FCSTD DOCUMENT  (FreeCAD 0.18R16093 (Git))
Label: Push2
License: All rights reserved
LicenseURL: http://en.wikipedia.org/wiki/All_rights_reserved
objects: App::DocumentObjectGroupPython×302, Part::Box×285, App::Part×154, Part::Extrusion×106, Part::Part2DObjectPython×97, Part::Cut×85, Part::Fillet×64, Part::Cylinder×35, Part::MultiFuse×32, Sketcher::SketchObject×22, PartDesign::Pad×11, App::DocumentObjectGroup×8, Image::ImagePlane×2
note: 748 computed .brp shape members not serialized (recipe doc carries the construction recipe); baked Part::Feature solids carry a one-line shape summary decoded from their .brp

FEATURE [Image::ImagePlane] ImagePlane  label="ImageTop"
  XSize = 378
  YSize = 304
FEATURE [Part::Box] Box  label="Cube"
  AttacherType = Attacher::AttachEngine3D
  Height = 23
  Length = 378
  Placement = pos=(-189,-152,-23) rot=(0,0,1;0rad)
  Width = 304
FEATURE [Sketcher::SketchObject] Sketch
  MapMode = 5
  sketch-geometry (1):
    g0: Circle CenterX=0 CenterY=0 CenterZ=0 NormalX=0 NormalY=0 NormalZ=1 AngleXU=0 Radius=6.32501
  constraints (1):
    c: Coincident(g0,g-1)
FEATURE [PartDesign::Pad] Pad
  Length = 15
  Length2 = 100
  Profile = -> Sketch
  Type = 0
FEATURE [Sketcher::SketchObject] Sketch001
  MapMode = 5
  sketch-geometry (1):
    g0: Circle CenterX=0 CenterY=0 CenterZ=0 NormalX=0 NormalY=0 NormalZ=1 AngleXU=0 Radius=6.32501
  constraints (1):
    c: Coincident(g0,g-1)
FEATURE [PartDesign::Pad] Pad001
  Length = 15
  Length2 = 100
  Profile = -> Sketch001
  Type = 0
FEATURE [Sketcher::SketchObject] Sketch002
  MapMode = 5
  sketch-geometry (1):
    g0: Circle CenterX=0 CenterY=0 CenterZ=0 NormalX=0 NormalY=0 NormalZ=1 AngleXU=0 Radius=6.32501
  constraints (1):
    c: Coincident(g0,g-1)
FEATURE [PartDesign::Pad] Pad002
  Length = 15
  Length2 = 100
  Profile = -> Sketch002
  Type = 0
FEATURE [Sketcher::SketchObject] Sketch003
  MapMode = 5
  sketch-geometry (1):
    g0: Circle CenterX=0 CenterY=0 CenterZ=0 NormalX=0 NormalY=0 NormalZ=1 AngleXU=0 Radius=6.32501
  constraints (1):
    c: Coincident(g0,g-1)
FEATURE [PartDesign::Pad] Pad003
  Length = 15
  Length2 = 100
  Profile = -> Sketch003
  Type = 0
FEATURE [Sketcher::SketchObject] Sketch004
  MapMode = 5
  sketch-geometry (1):
    g0: Circle CenterX=0 CenterY=0 CenterZ=0 NormalX=0 NormalY=0 NormalZ=1 AngleXU=0 Radius=6.32501
  constraints (1):
    c: Coincident(g0,g-1)
FEATURE [PartDesign::Pad] Pad004
  Length = 15
  Length2 = 100
  Profile = -> Sketch004
  Type = 0
FEATURE [Sketcher::SketchObject] Sketch005
  MapMode = 5
  sketch-geometry (1):
    g0: Circle CenterX=0 CenterY=0 CenterZ=0 NormalX=0 NormalY=0 NormalZ=1 AngleXU=0 Radius=6.32501
  constraints (1):
    c: Coincident(g0,g-1)
FEATURE [PartDesign::Pad] Pad005
  Length = 15
  Length2 = 100
  Profile = -> Sketch005
  Type = 0
FEATURE [Sketcher::SketchObject] Sketch006
  MapMode = 5
  sketch-geometry (1):
    g0: Circle CenterX=0 CenterY=0 CenterZ=0 NormalX=0 NormalY=0 NormalZ=1 AngleXU=0 Radius=6.32501
  constraints (1):
    c: Coincident(g0,g-1)
FEATURE [PartDesign::Pad] Pad006
  Length = 15
  Length2 = 100
  Profile = -> Sketch006
  Type = 0
FEATURE [Sketcher::SketchObject] Sketch007
  MapMode = 5
  sketch-geometry (1):
    g0: Circle CenterX=0 CenterY=0 CenterZ=0 NormalX=0 NormalY=0 NormalZ=1 AngleXU=0 Radius=6.32501
  constraints (1):
    c: Coincident(g0,g-1)
FEATURE [PartDesign::Pad] Pad007
  Length = 15
  Length2 = 100
  Profile = -> Sketch007
  Type = 0
FEATURE [Sketcher::SketchObject] Sketch008
  MapMode = 5
  sketch-geometry (1):
    g0: Circle CenterX=0 CenterY=0 CenterZ=0 NormalX=0 NormalY=0 NormalZ=1 AngleXU=0 Radius=6.32501
  constraints (1):
    c: Coincident(g0,g-1)
FEATURE [PartDesign::Pad] Pad008
  Length = 15
  Length2 = 100
  Profile = -> Sketch008
  Type = 0
FEATURE [Sketcher::SketchObject] Sketch009
  MapMode = 5
  sketch-geometry (1):
    g0: Circle CenterX=0 CenterY=0 CenterZ=0 NormalX=0 NormalY=0 NormalZ=1 AngleXU=0 Radius=6.32501
  constraints (1):
    c: Coincident(g0,g-1)
FEATURE [PartDesign::Pad] Pad009
  Length = 15
  Length2 = 100
  Profile = -> Sketch009
  Type = 0
FEATURE [Sketcher::SketchObject] Sketch010
  MapMode = 5
  sketch-geometry (1):
    g0: Circle CenterX=0 CenterY=0 CenterZ=0 NormalX=0 NormalY=0 NormalZ=1 AngleXU=0 Radius=6.32501
  constraints (1):
    c: Coincident(g0,g-1)
FEATURE [PartDesign::Pad] Pad010
  Length = 15
  Length2 = 100
  Profile = -> Sketch010
  Type = 0
FEATURE [Part::Box] Box001  label="Cube001"
  AttacherType = Attacher::AttachEngine3D
  Height = 1
  Length = 25
  Width = 11
FEATURE [Part::Box] Box003  label="Cube003"
  AttacherType = Attacher::AttachEngine3D
  Height = 1
  Length = 25
  Width = 11
FEATURE [Image::ImagePlane] ImagePlane002  label="ImageBack"
  Placement = pos=(0,152,-4) rot=(0,0.707107,0.707107;3.14159rad)
  XSize = 378
  YSize = 40.11
FEATURE [Part::Box] Box011  label="Cube011"
  AttacherType = Attacher::AttachEngine3D
  Height = 1
  Length = 19
  Width = 11
FEATURE [Part::Box] Box012  label="Cube012"
  AttacherType = Attacher::AttachEngine3D
  Height = 1
  Length = 19
  Width = 11
FEATURE [App::DocumentObjectGroupPython] FPSimRotaryEncoder  label="EncoderTempo"  # scripted group (container) (typed FeaturePython)
  Group = -> [Pad]
  IncrementsPerRev = 64
  MouseSensitivity = 1
  NumSnapInPositions = 0
  PushButton = false
  PushButtonDepth = 1
  RotationAxis = (0,0,1)
  RotationCenter = (0,0,15)
  TouchSensitive = false
FEATURE [App::Part] Part001  label="FrEncoderTempo"
  Group = -> [Sketch,Pad,FPSimRotaryEncoder]
  License = CC BY 3.0
  LicenseURL = http://creativecommons.org/licenses/by/3.0/
  Origin = -> Origin002
  Placement = pos=(-172.3,137,0) rot=(0,0,1;0rad)
FEATURE [App::DocumentObjectGroupPython] FPSimRotaryEncoder011  label="EncoderMetronome"  # scripted group (container) (typed FeaturePython)
  Group = -> [Pad001]
  IncrementsPerRev = 64
  MouseSensitivity = 1
  NumSnapInPositions = 0
  PushButton = false
  PushButtonDepth = 1
  RotationAxis = (0,0,1)
  RotationCenter = (0,0,15)
  TouchSensitive = false
FEATURE [App::Part] Part002  label="FrEncoderMetronome"
  Group = -> [Pad001,Sketch001,FPSimRotaryEncoder011]
  License = CC BY 3.0
  LicenseURL = http://creativecommons.org/licenses/by/3.0/
  Origin = -> Origin003
  Placement = pos=(-142.3,137,0) rot=(0,0,1;0rad)
FEATURE [App::DocumentObjectGroupPython] FPSimRotaryEncoder012  label="Encoder[0]"  # scripted group (container) (typed FeaturePython)
  Group = -> [Pad002]
  IncrementsPerRev = 64
  MouseSensitivity = 1
  NumSnapInPositions = 0
  PushButton = false
  PushButtonDepth = 1
  RotationAxis = (0,0,1)
  RotationCenter = (0,0,15)
  TouchSensitive = false
FEATURE [App::Part] Part003  label="FrEncoder[0]"
  Group = -> [Pad002,Sketch002,FPSimRotaryEncoder012]
  License = CC BY 3.0
  LicenseURL = http://creativecommons.org/licenses/by/3.0/
  Origin = -> Origin004
  Placement = pos=(-107,137,0) rot=(0,0,1;0rad)
FEATURE [App::DocumentObjectGroupPython] FPSimRotaryEncoder013  label="Encoder[1]"  # scripted group (container) (typed FeaturePython)
  Group = -> [Pad003]
  IncrementsPerRev = 64
  MouseSensitivity = 1
  NumSnapInPositions = 0
  PushButton = false
  PushButtonDepth = 1
  RotationAxis = (0,0,1)
  RotationCenter = (0,0,15)
  TouchSensitive = false
FEATURE [App::Part] Part004  label="FrEncoder[1]"
  Group = -> [Sketch003,Pad003,FPSimRotaryEncoder013]
  License = CC BY 3.0
  LicenseURL = http://creativecommons.org/licenses/by/3.0/
  Origin = -> Origin005
  Placement = pos=(-78,137,0) rot=(0,0,1;0rad)
FEATURE [App::DocumentObjectGroupPython] FPSimRotaryEncoder014  label="Encoder[2]"  # scripted group (container) (typed FeaturePython)
  Group = -> [Pad004]
  IncrementsPerRev = 64
  MouseSensitivity = 1
  NumSnapInPositions = 0
  PushButton = false
  PushButtonDepth = 1
  RotationAxis = (0,0,1)
  RotationCenter = (0,0,15)
  TouchSensitive = false
FEATURE [App::Part] Part005  label="FrEncoder[2]"
  Group = -> [Sketch004,Pad004,FPSimRotaryEncoder014]
  License = CC BY 3.0
  LicenseURL = http://creativecommons.org/licenses/by/3.0/
  Origin = -> Origin006
  Placement = pos=(-49,137,0) rot=(0,0,1;0rad)
FEATURE [App::DocumentObjectGroupPython] FPSimRotaryEncoder015  label="Encoder[3]"  # scripted group (container) (typed FeaturePython)
  Group = -> [Pad005]
  IncrementsPerRev = 64
  MouseSensitivity = 1
  NumSnapInPositions = 0
  PushButton = false
  PushButtonDepth = 1
  RotationAxis = (0,0,1)
  RotationCenter = (0,0,15)
  TouchSensitive = false
FEATURE [App::Part] Part006  label="FrEncoder[3]"
  Group = -> [Sketch005,Pad005,FPSimRotaryEncoder015]
  License = CC BY 3.0
  LicenseURL = http://creativecommons.org/licenses/by/3.0/
  Origin = -> Origin007
  Placement = pos=(-20,137,0) rot=(0,0,1;0rad)
FEATURE [App::DocumentObjectGroupPython] FPSimRotaryEncoder016  label="Encoder[4]"  # scripted group (container) (typed FeaturePython)
  Group = -> [Pad006]
  IncrementsPerRev = 64
  MouseSensitivity = 1
  NumSnapInPositions = 0
  PushButton = false
  PushButtonDepth = 1
  RotationAxis = (0,0,1)
  RotationCenter = (0,0,15)
  TouchSensitive = false
FEATURE [App::Part] Part007  label="FrEncoder[4]"
  Group = -> [Sketch006,Pad006,FPSimRotaryEncoder016]
  License = CC BY 3.0
  LicenseURL = http://creativecommons.org/licenses/by/3.0/
  Origin = -> Origin008
  Placement = pos=(8.8,137,0) rot=(0,0,1;0rad)
FEATURE [App::DocumentObjectGroupPython] FPSimRotaryEncoder017  label="Encoder[5]"  # scripted group (container) (typed FeaturePython)
  Group = -> [Pad007]
  IncrementsPerRev = 64
  MouseSensitivity = 1
  NumSnapInPositions = 0
  PushButton = false
  PushButtonDepth = 1
  RotationAxis = (0,0,1)
  RotationCenter = (0,0,15)
  TouchSensitive = false
FEATURE [App::Part] Part008  label="FrEncoder[5]"
  Group = -> [Sketch007,Pad007,FPSimRotaryEncoder017]
  License = CC BY 3.0
  LicenseURL = http://creativecommons.org/licenses/by/3.0/
  Origin = -> Origin009
  Placement = pos=(37.8,137,0) rot=(0,0,1;0rad)
FEATURE [App::DocumentObjectGroupPython] FPSimRotaryEncoder018  label="Encoder[6]"  # scripted group (container) (typed FeaturePython)
  Group = -> [Pad008]
  IncrementsPerRev = 64
  MouseSensitivity = 1
  NumSnapInPositions = 0
  PushButton = false
  PushButtonDepth = 1
  RotationAxis = (0,0,1)
  RotationCenter = (0,0,15)
  TouchSensitive = false
FEATURE [App::Part] Part009  label="FrEncoder[6]"
  Group = -> [Sketch008,Pad008,FPSimRotaryEncoder018]
  License = CC BY 3.0
  LicenseURL = http://creativecommons.org/licenses/by/3.0/
  Origin = -> Origin010
  Placement = pos=(66.8,137,0) rot=(0,0,1;0rad)
FEATURE [App::DocumentObjectGroupPython] FPSimRotaryEncoder019  label="Encoder[7]"  # scripted group (container) (typed FeaturePython)
  Group = -> [Pad009]
  IncrementsPerRev = 64
  MouseSensitivity = 1
  NumSnapInPositions = 0
  PushButton = false
  PushButtonDepth = 1
  RotationAxis = (0,0,1)
  RotationCenter = (0,0,15)
  TouchSensitive = false
FEATURE [App::Part] Part010  label="FrEncoder[7]"
  Group = -> [Sketch009,Pad009,FPSimRotaryEncoder019]
  License = CC BY 3.0
  LicenseURL = http://creativecommons.org/licenses/by/3.0/
  Origin = -> Origin011
  Placement = pos=(95.8,137,0) rot=(0,0,1;0rad)
FEATURE [App::DocumentObjectGroupPython] FPSimRotaryEncoder020  label="EncoderMain"  # scripted group (container) (typed FeaturePython)
  Group = -> [Pad010]
  IncrementsPerRev = 64
  MouseSensitivity = 1
  NumSnapInPositions = 0
  PushButton = false
  PushButtonDepth = 1
  RotationAxis = (0,0,1)
  RotationCenter = (0,0,15)
  TouchSensitive = false
FEATURE [App::Part] Part011  label="FrEncoderMain"
  Group = -> [Pad010,Sketch010,FPSimRotaryEncoder020]
  License = CC BY 3.0
  LicenseURL = http://creativecommons.org/licenses/by/3.0/
  Origin = -> Origin012
  Placement = pos=(163.9,137,0) rot=(0,0,1;0rad)
FEATURE [App::DocumentObjectGroup] Group  label="Encoders"
  Group = -> [Part001,Part002,Part003,Part004,Part005,Part006,Part007,Part008,Part009,Part010,Part011]
FEATURE [Part::Box] Box013  label="Cube013"
  AttacherType = Attacher::AttachEngine3D
  Height = 1
  Length = 18.5
  Width = 18.5
FEATURE [Part::Box] Box015  label="Cube015"
  AttacherType = Attacher::AttachEngine3D
  Height = 1
  Length = 18.5
  Width = 18.5
FEATURE [Part::Box] Box016  label="Cube016"
  AttacherType = Attacher::AttachEngine3D
  Height = 1
  Length = 18.5
  Width = 18.5
FEATURE [Part::Box] Box018  label="Cube018"
  AttacherType = Attacher::AttachEngine3D
  Height = 1
  Length = 18.5
  Width = 18.5
FEATURE [Part::Box] Box021  label="Cube021"
  AttacherType = Attacher::AttachEngine3D
  Height = 0.001
  Length = 232
  Width = 40
FEATURE [App::DocumentObjectGroupPython] FPSimDisplay  label="Display"  # scripted group (container) (typed FeaturePython)
  Group = -> [Box021]
  ResolutionX = 960
  ResolutionY = 160
FEATURE [App::Part] Part032  label="FrDisplay"
  Group = -> [Box021,FPSimDisplay]
  License = CC BY 3.0
  LicenseURL = http://creativecommons.org/licenses/by/3.0/
  Origin = -> Origin032
  Placement = pos=(-121,61.5,0) rot=(0,0,1;0rad)
FEATURE [Part::Box] Box022  label="Cube022"
  AttacherType = Attacher::AttachEngine3D
  Height = 1
  Length = 17
  Width = 10
FEATURE [Part::Box] Box025  label="Cube025"
  AttacherType = Attacher::AttachEngine3D
  Height = 1
  Length = 18.5
  Width = 18.5
FEATURE [Part::Box] Box028  label="Cube028"
  AttacherType = Attacher::AttachEngine3D
  Height = 1
  Length = 18.5
  Width = 18.5
FEATURE [Part::Box] Box030  label="Cube030"
  AttacherType = Attacher::AttachEngine3D
  Height = 1
  Length = 18.5
  Width = 17.5
FEATURE [Part::Box] Box031  label="Cube031"
  AttacherType = Attacher::AttachEngine3D
  Height = 1
  Length = 18.5
  Width = 17.5
FEATURE [Part::Box] Box033  label="Cube033"
  AttacherType = Attacher::AttachEngine3D
  Height = 1
  Length = 18.5
  Width = 18.5
FEATURE [Part::Box] Box034  label="Cube034"
  AttacherType = Attacher::AttachEngine3D
  Height = 1.01
  Length = 21.5
  Placement = pos=(0,0,-1) rot=(0,0,1;0rad)
  Width = 172
FEATURE [Part::Box] Box035  label="Cube035"
  AttacherType = Attacher::AttachEngine3D
  Height = 1
  Length = 21.5
  Placement = pos=(-152,-140.5,-0.5) rot=(0,0,1;0rad)
  Width = 172
FEATURE [Part::Cut] Cut  label="TheBox"
  Base = -> Box
  Placement = pos=(0,0,-0.2) rot=(0,0,1;0rad)
  Tool = -> Box035
FEATURE [Part::Cylinder] Cylinder
  Angle = 360
  AttacherType = Attacher::AttachEngine3D
  Height = 0.1
  Placement = pos=(3,2,0) rot=(0,0,1;0rad)
  Radius = 2
FEATURE [App::DocumentObjectGroupPython] FPSimTouchSurface  label="TouchStrip"  # scripted group (container) (typed FeaturePython)
  Group = -> [Box034]
  PressureResolution = 0
  ResolutionX = 16384
  ResolutionY = 0
FEATURE [Part::Cylinder] Cylinder001 .. Cylinder030  x30 (patterned run collapsed; names and placements below)
  Angle = 360
  AttacherType = Attacher::AttachEngine3D
  Height = 0.1
  Radius = 2
  placements: 30 in arithmetic series — first pos=(3,7.6,0) rot=(0,0,1;0rad), step (0,5.6,0), last pos=(3,170,0) rot=(0,0,1;0rad)
FEATURE [App::DocumentObjectGroupPython] FPSimLED  label="TouchSurfaceLed[0]"  # scripted group (container) (typed FeaturePython)
  Group = -> [Cylinder]
FEATURE [App::DocumentObjectGroupPython] FPSimLED001  label="TouchSurfaceLed[1]"  # scripted group (container) (typed FeaturePython)
  Group = -> [Cylinder001]
FEATURE [App::DocumentObjectGroupPython] FPSimLED002  label="TouchSurfaceLed[2]"  # scripted group (container) (typed FeaturePython)
  Group = -> [Cylinder002]
FEATURE [App::DocumentObjectGroupPython] FPSimLED003  label="TouchSurfaceLed[3]"  # scripted group (container) (typed FeaturePython)
  Group = -> [Cylinder003]
FEATURE [App::DocumentObjectGroupPython] FPSimLED004  label="TouchSurfaceLed[4]"  # scripted group (container) (typed FeaturePython)
  Group = -> [Cylinder004]
FEATURE [App::DocumentObjectGroupPython] FPSimLED005  label="TouchSurfaceLed[5]"  # scripted group (container) (typed FeaturePython)
  Group = -> [Cylinder005]
FEATURE [App::DocumentObjectGroupPython] FPSimLED006  label="TouchSurfaceLed[6]"  # scripted group (container) (typed FeaturePython)
  Group = -> [Cylinder006]
FEATURE [App::DocumentObjectGroupPython] FPSimLED007  label="TouchSurfaceLed[7]"  # scripted group (container) (typed FeaturePython)
  Group = -> [Cylinder007]
FEATURE [App::DocumentObjectGroupPython] FPSimLED008  label="TouchSurfaceLed[8]"  # scripted group (container) (typed FeaturePython)
  Group = -> [Cylinder008]
FEATURE [App::DocumentObjectGroupPython] FPSimLED009  label="TouchSurfaceLed[9]"  # scripted group (container) (typed FeaturePython)
  Group = -> [Cylinder009]
FEATURE [App::DocumentObjectGroupPython] FPSimLED010  label="TouchSurfaceLed[10]"  # scripted group (container) (typed FeaturePython)
  Group = -> [Cylinder010]
FEATURE [App::DocumentObjectGroupPython] FPSimLED011  label="TouchSurfaceLed[11]"  # scripted group (container) (typed FeaturePython)
  Group = -> [Cylinder011]
FEATURE [App::DocumentObjectGroupPython] FPSimLED012  label="TouchSurfaceLed[12]"  # scripted group (container) (typed FeaturePython)
  Group = -> [Cylinder012]
FEATURE [App::DocumentObjectGroupPython] FPSimLED013  label="TouchSurfaceLed[13]"  # scripted group (container) (typed FeaturePython)
  Group = -> [Cylinder013]
FEATURE [App::DocumentObjectGroupPython] FPSimLED014  label="TouchSurfaceLed[14]"  # scripted group (container) (typed FeaturePython)
  Group = -> [Cylinder014]
FEATURE [App::DocumentObjectGroupPython] FPSimLED015  label="TouchSurfaceLed[15]"  # scripted group (container) (typed FeaturePython)
  Group = -> [Cylinder015]
FEATURE [App::DocumentObjectGroupPython] FPSimLED016  label="TouchSurfaceLed[16]"  # scripted group (container) (typed FeaturePython)
  Group = -> [Cylinder016]
FEATURE [App::DocumentObjectGroupPython] FPSimLED017  label="TouchSurfaceLed[17]"  # scripted group (container) (typed FeaturePython)
  Group = -> [Cylinder017]
FEATURE [App::DocumentObjectGroupPython] FPSimLED018  label="TouchSurfaceLed[18]"  # scripted group (container) (typed FeaturePython)
  Group = -> [Cylinder018]
FEATURE [App::DocumentObjectGroupPython] FPSimLED019  label="TouchSurfaceLed[19]"  # scripted group (container) (typed FeaturePython)
  Group = -> [Cylinder019]
FEATURE [App::DocumentObjectGroupPython] FPSimLED020  label="TouchSurfaceLed[20]"  # scripted group (container) (typed FeaturePython)
  Group = -> [Cylinder020]
FEATURE [App::DocumentObjectGroupPython] FPSimLED021  label="TouchSurfaceLed[21]"  # scripted group (container) (typed FeaturePython)
  Group = -> [Cylinder021]
FEATURE [App::DocumentObjectGroupPython] FPSimLED022  label="TouchSurfaceLed[22]"  # scripted group (container) (typed FeaturePython)
  Group = -> [Cylinder022]
FEATURE [App::DocumentObjectGroupPython] FPSimLED023  label="TouchSurfaceLed[23]"  # scripted group (container) (typed FeaturePython)
  Group = -> [Cylinder023]
FEATURE [App::DocumentObjectGroupPython] FPSimLED024  label="TouchSurfaceLed[24]"  # scripted group (container) (typed FeaturePython)
  Group = -> [Cylinder024]
FEATURE [App::DocumentObjectGroupPython] FPSimLED025  label="TouchSurfaceLed[25]"  # scripted group (container) (typed FeaturePython)
  Group = -> [Cylinder025]
FEATURE [App::DocumentObjectGroupPython] FPSimLED026  label="TouchSurfaceLed[26]"  # scripted group (container) (typed FeaturePython)
  Group = -> [Cylinder026]
FEATURE [App::DocumentObjectGroupPython] FPSimLED027  label="TouchSurfaceLed[27]"  # scripted group (container) (typed FeaturePython)
  Group = -> [Cylinder027]
FEATURE [App::DocumentObjectGroupPython] FPSimLED028  label="TouchSurfaceLed[28]"  # scripted group (container) (typed FeaturePython)
  Group = -> [Cylinder028]
FEATURE [App::DocumentObjectGroupPython] FPSimLED029  label="TouchSurfaceLed[29]"  # scripted group (container) (typed FeaturePython)
  Group = -> [Cylinder029]
FEATURE [App::DocumentObjectGroupPython] FPSimLED030  label="TouchSurfaceLed[30]"  # scripted group (container) (typed FeaturePython)
  Group = -> [Cylinder030]
FEATURE [App::Part] Part045  label="FrTouchSurface"
  Group = -> [Box034,FPSimTouchSurface,Cylinder,FPSimLED,Cylinder001,FPSimLED001,Cylinder002,FPSimLED002,Cylinder003,FPSimLED003,Cylinder004,FPSimLED004,Cylinder005,FPSimLED005,Cylinder006,FPSimLED006,Cylinder007,FPSimLED007,Cylinder008,FPSimLED008,Cylinder009,FPSimLED009,Cylinder010,FPSimLED010,Cylinder011,FPSimLED011,Cylinder012,FPSimLED012,Cylinder013,FPSimLED013,Cylinder014,FPSimLED014,Cylinder015,+31 more]
  License = CC BY 3.0
  LicenseURL = http://creativecommons.org/licenses/by/3.0/
  Origin = -> Origin045
  Placement = pos=(-152,-140.5,-0.5) rot=(0,0,1;0rad)
FEATURE [Part::Box] Box044  label="Cube044"
  AttacherType = Attacher::AttachEngine3D
  Height = 1
  Length = 17
  Width = 10
FEATURE [Part::Box] Box045  label="Cube045"
  AttacherType = Attacher::AttachEngine3D
  Height = 1
  Length = 18.5
  Width = 18.5
FEATURE [Part::Box] Box046  label="Cube046"
  AttacherType = Attacher::AttachEngine3D
  Height = 2
  Length = 1
  Placement = pos=(0,0,0) rot=(0,0,1;0.785398rad)
  Width = 5
FEATURE [Part::Box] Box047  label="Cube047"
  AttacherType = Attacher::AttachEngine3D
  Height = 2
  Length = 1
  Placement = pos=(0,0,0) rot=(0,0,1;2.35619rad)
  Width = 4
FEATURE [Part::MultiFuse] Fusion  label="LilArrowHole"
  Placement = pos=(16,5,0) rot=(0,0,1;0rad)
  Shapes = -> [Box046,Box047]
FEATURE [Part::Box] Box048  label="Cube048"
  AttacherType = Attacher::AttachEngine3D
  Height = 1
  Length = 1
  Placement = pos=(0,0,0) rot=(0,0,1;2.35619rad)
  Width = 4
FEATURE [Part::Box] Box049  label="Cube049"
  AttacherType = Attacher::AttachEngine3D
  Height = 1
  Length = 1
  Placement = pos=(0,0,0) rot=(0,0,1;0.785398rad)
  Width = 5
FEATURE [Part::MultiFuse] Fusion001  label="LilArrow"
  Placement = pos=(16,5,0) rot=(0,0,1;0rad)
  Shapes = -> [Box048,Box049]
FEATURE [Part::Cut] Cut001
  Base = -> Box045
  Tool = -> Fusion
FEATURE [Part::Box] Box055  label="Cube055"
  AttacherType = Attacher::AttachEngine3D
  Height = 1
  Length = 18.5
  Width = 18.5
FEATURE [Part::Box] Box056  label="Cube056"
  AttacherType = Attacher::AttachEngine3D
  Height = 1
  Length = 1
  Placement = pos=(0,0,0) rot=(0,0,1;0.785398rad)
  Width = 5
FEATURE [Part::Box] Box057  label="Cube057"
  AttacherType = Attacher::AttachEngine3D
  Height = 2
  Length = 1
  Placement = pos=(0,0,0) rot=(0,0,1;0.785398rad)
  Width = 5
FEATURE [Part::Box] Box058  label="Cube058"
  AttacherType = Attacher::AttachEngine3D
  Height = 2
  Length = 1
  Placement = pos=(0,0,0) rot=(0,0,1;2.35619rad)
  Width = 4
FEATURE [Part::MultiFuse] Fusion004  label="LilArrowHole002"
  Placement = pos=(16,5,0) rot=(0,0,1;0rad)
  Shapes = -> [Box057,Box058]
FEATURE [Part::Cut] Cut003
  Base = -> Box055
  Tool = -> Fusion004
FEATURE [Part::Box] Box059  label="Cube059"
  AttacherType = Attacher::AttachEngine3D
  Height = 1
  Length = 1
  Placement = pos=(0,0,0) rot=(0,0,1;2.35619rad)
  Width = 4
FEATURE [Part::MultiFuse] Fusion005  label="LilArrow002"
  Placement = pos=(16,5,0) rot=(0,0,1;0rad)
  Shapes = -> [Box059,Box056]
FEATURE [Part::Box] Box060  label="Cube060"
  AttacherType = Attacher::AttachEngine3D
  Height = 1
  Length = 18.5
  Width = 18.5
FEATURE [Part::Box] Box061  label="Cube061"
  AttacherType = Attacher::AttachEngine3D
  Height = 1
  Length = 1
  Placement = pos=(0,0,0) rot=(0,0,1;0.785398rad)
  Width = 5
FEATURE [Part::Box] Box062  label="Cube062"
  AttacherType = Attacher::AttachEngine3D
  Height = 2
  Length = 1
  Placement = pos=(0,0,0) rot=(0,0,1;0.785398rad)
  Width = 5
FEATURE [Part::Box] Box063  label="Cube063"
  AttacherType = Attacher::AttachEngine3D
  Height = 2
  Length = 1
  Placement = pos=(0,0,0) rot=(0,0,1;2.35619rad)
  Width = 4
FEATURE [Part::MultiFuse] Fusion006  label="LilArrowHole003"
  Placement = pos=(16,5,0) rot=(0,0,1;0rad)
  Shapes = -> [Box062,Box063]
FEATURE [Part::Cut] Cut004
  Base = -> Box060
  Tool = -> Fusion006
FEATURE [Part::Box] Box064  label="Cube064"
  AttacherType = Attacher::AttachEngine3D
  Height = 1
  Length = 1
  Placement = pos=(0,0,0) rot=(0,0,1;2.35619rad)
  Width = 4
FEATURE [Part::MultiFuse] Fusion007  label="LilArrow003"
  Placement = pos=(16,5,0) rot=(0,0,1;0rad)
  Shapes = -> [Box064,Box061]
FEATURE [Part::Box] Box065  label="Cube065"
  AttacherType = Attacher::AttachEngine3D
  Height = 1
  Length = 18.5
  Width = 18.5
FEATURE [Part::Box] Box066  label="Cube066"
  AttacherType = Attacher::AttachEngine3D
  Height = 1
  Length = 1
  Placement = pos=(0,0,0) rot=(0,0,1;0.785398rad)
  Width = 5
FEATURE [Part::Box] Box067  label="Cube067"
  AttacherType = Attacher::AttachEngine3D
  Height = 2
  Length = 1
  Placement = pos=(0,0,0) rot=(0,0,1;0.785398rad)
  Width = 5
FEATURE [Part::Box] Box068  label="Cube068"
  AttacherType = Attacher::AttachEngine3D
  Height = 2
  Length = 1
  Placement = pos=(0,0,0) rot=(0,0,1;2.35619rad)
  Width = 4
FEATURE [Part::MultiFuse] Fusion008  label="LilArrowHole004"
  Placement = pos=(16,5,0) rot=(0,0,1;0rad)
  Shapes = -> [Box067,Box068]
FEATURE [Part::Cut] Cut005
  Base = -> Box065
  Tool = -> Fusion008
FEATURE [Part::Box] Box069  label="Cube069"
  AttacherType = Attacher::AttachEngine3D
  Height = 1
  Length = 1
  Placement = pos=(0,0,0) rot=(0,0,1;2.35619rad)
  Width = 4
FEATURE [Part::MultiFuse] Fusion009  label="LilArrow004"
  Placement = pos=(16,5,0) rot=(0,0,1;0rad)
  Shapes = -> [Box069,Box066]
FEATURE [Part::Box] Box070  label="Cube070"
  AttacherType = Attacher::AttachEngine3D
  Height = 1
  Length = 18.5
  Width = 18.5
FEATURE [Part::Box] Box071  label="Cube071"
  AttacherType = Attacher::AttachEngine3D
  Height = 1
  Length = 1
  Placement = pos=(0,0,0) rot=(0,0,1;0.785398rad)
  Width = 5
FEATURE [Part::Box] Box072  label="Cube072"
  AttacherType = Attacher::AttachEngine3D
  Height = 2
  Length = 1
  Placement = pos=(0,0,0) rot=(0,0,1;0.785398rad)
  Width = 5
FEATURE [Part::Box] Box073  label="Cube073"
  AttacherType = Attacher::AttachEngine3D
  Height = 2
  Length = 1
  Placement = pos=(0,0,0) rot=(0,0,1;2.35619rad)
  Width = 4
FEATURE [Part::MultiFuse] Fusion010  label="LilArrowHole005"
  Placement = pos=(16,5,0) rot=(0,0,1;0rad)
  Shapes = -> [Box072,Box073]
FEATURE [Part::Cut] Cut006
  Base = -> Box070
  Tool = -> Fusion010
FEATURE [Part::Box] Box074  label="Cube074"
  AttacherType = Attacher::AttachEngine3D
  Height = 1
  Length = 1
  Placement = pos=(0,0,0) rot=(0,0,1;2.35619rad)
  Width = 4
FEATURE [Part::MultiFuse] Fusion011  label="LilArrow005"
  Placement = pos=(16,5,0) rot=(0,0,1;0rad)
  Shapes = -> [Box074,Box071]
FEATURE [Part::Box] Box075  label="Cube075"
  AttacherType = Attacher::AttachEngine3D
  Height = 1
  Length = 18.5
  Width = 18.5
FEATURE [Part::Box] Box076  label="Cube076"
  AttacherType = Attacher::AttachEngine3D
  Height = 1
  Length = 1
  Placement = pos=(0,0,0) rot=(0,0,1;0.785398rad)
  Width = 5
FEATURE [Part::Box] Box077  label="Cube077"
  AttacherType = Attacher::AttachEngine3D
  Height = 2
  Length = 1
  Placement = pos=(0,0,0) rot=(0,0,1;0.785398rad)
  Width = 5
FEATURE [Part::Box] Box078  label="Cube078"
  AttacherType = Attacher::AttachEngine3D
  Height = 2
  Length = 1
  Placement = pos=(0,0,0) rot=(0,0,1;2.35619rad)
  Width = 4
FEATURE [Part::MultiFuse] Fusion012  label="LilArrowHole006"
  Placement = pos=(16,5,0) rot=(0,0,1;0rad)
  Shapes = -> [Box077,Box078]
FEATURE [Part::Cut] Cut007
  Base = -> Box075
  Tool = -> Fusion012
FEATURE [Part::Box] Box079  label="Cube079"
  AttacherType = Attacher::AttachEngine3D
  Height = 1
  Length = 1
  Placement = pos=(0,0,0) rot=(0,0,1;2.35619rad)
  Width = 4
FEATURE [Part::MultiFuse] Fusion013  label="LilArrow006"
  Placement = pos=(16,5,0) rot=(0,0,1;0rad)
  Shapes = -> [Box079,Box076]
FEATURE [Part::Box] Box080  label="Cube080"
  AttacherType = Attacher::AttachEngine3D
  Height = 1
  Length = 18.5
  Width = 18.5
FEATURE [Part::Box] Box081  label="Cube081"
  AttacherType = Attacher::AttachEngine3D
  Height = 1
  Length = 1
  Placement = pos=(0,0,0) rot=(0,0,1;0.785398rad)
  Width = 5
FEATURE [Part::Box] Box082  label="Cube082"
  AttacherType = Attacher::AttachEngine3D
  Height = 2
  Length = 1
  Placement = pos=(0,0,0) rot=(0,0,1;0.785398rad)
  Width = 5
FEATURE [Part::Box] Box083  label="Cube083"
  AttacherType = Attacher::AttachEngine3D
  Height = 2
  Length = 1
  Placement = pos=(0,0,0) rot=(0,0,1;2.35619rad)
  Width = 4
FEATURE [Part::MultiFuse] Fusion014  label="LilArrowHole007"
  Placement = pos=(16,5,0) rot=(0,0,1;0rad)
  Shapes = -> [Box082,Box083]
FEATURE [Part::Cut] Cut008
  Base = -> Box080
  Tool = -> Fusion014
FEATURE [Part::Box] Box084  label="Cube084"
  AttacherType = Attacher::AttachEngine3D
  Height = 1
  Length = 1
  Placement = pos=(0,0,0) rot=(0,0,1;2.35619rad)
  Width = 4
FEATURE [Part::MultiFuse] Fusion015  label="LilArrow007"
  Placement = pos=(16,5,0) rot=(0,0,1;0rad)
  Shapes = -> [Box084,Box081]
FEATURE [Sketcher::SketchObject] Sketch011
  sketch-geometry (3):
    g0: LineSegment StartX=0 StartY=0 StartZ=0 EndX=18.5 EndY=-18.5 EndZ=0
    g1: LineSegment StartX=-18.5 StartY=-18.5 StartZ=0 EndX=0 EndY=0 EndZ=0
    g2: LineSegment StartX=-18.5 StartY=-18.5 StartZ=0 EndX=18.5 EndY=-18.5 EndZ=0
  constraints (7):
    c: Coincident(g0,g-1)
    c: Coincident(g1,g0)
    c: Coincident(g2,g0)
    c: Coincident(g2,g1)
    c: Symmetric(g0,g1,g-2)
    c: Perpendicular(g1,g0)
    c: DistanceX(g1,g0) = 37
FEATURE [Part::Extrusion] Extrude
  Base = -> Sketch011
  Dir = (0,0,1)
  DirMode = 2
  FaceMakerClass = Part::FaceMakerBullseye
  LengthFwd = 1
  LengthRev = 0
  Solid = true
  Symmetric = false
FEATURE [Part::Box] Box085  label="Cube085"
  AttacherType = Attacher::AttachEngine3D
  Height = 2
  Length = 7.5
  Width = 1
FEATURE [Part::Box] Box086  label="Cube086"
  AttacherType = Attacher::AttachEngine3D
  Height = 2
  Length = 7.5
  Placement = pos=(1,0,0) rot=(0,0,1;1.5708rad)
  Width = 1
FEATURE [Part::MultiFuse] Fusion016  label="BigArrowHole"
  Placement = pos=(0,-15,0) rot=(0,0,1;0.785398rad)
  Shapes = -> [Box086,Box085]
FEATURE [Part::Box] Box087  label="Cube087"
  AttacherType = Attacher::AttachEngine3D
  Height = 1
  Length = 7.5
  Placement = pos=(1,0,0) rot=(0,0,1;1.5708rad)
  Width = 1
FEATURE [Part::Box] Box088  label="Cube088"
  AttacherType = Attacher::AttachEngine3D
  Height = 1
  Length = 7.5
  Width = 1
FEATURE [Part::MultiFuse] Fusion017  label="BigArrowLed"
  Placement = pos=(0,-15,0) rot=(0,0,1;0.785398rad)
  Shapes = -> [Box087,Box088]
FEATURE [Part::Cut] Cut009
  Base = -> Extrude
  Tool = -> Fusion016
FEATURE [App::DocumentObjectGroupPython] FPSimLED039  label="LedDownArrow"  # scripted group (container) (typed FeaturePython)
  Group = -> [Fusion017]
FEATURE [App::DocumentObjectGroupPython] FPSimButton049  label="BtnDownArrow"  # scripted group (container) (typed FeaturePython)
  Group = -> [Cut009,FPSimLED039]
  PressureResolutionAng = (0,0,0)
  PressureResolutionLin = (0,0,0)
  RotationAngle = 0
  RotationAxis = (0,0,0)
  RotationCenter = (0,0,0)
  SwitchMode = false
  Translation = (0,0,-1)
FEATURE [App::Part] Part063  label="FrDownArrow"
  Group = -> [FPSimLED039,Box087,Box086,Fusion016,Fusion017,Box088,Sketch011,Cut009,Box085,Extrude,FPSimButton049]
  License = CC BY 3.0
  LicenseURL = http://creativecommons.org/licenses/by/3.0/
  Origin = -> Origin063
  Placement = pos=(0,-0.25,0) rot=(0,0,1;0rad)
FEATURE [Part::Box] Box089  label="Cube089"
  AttacherType = Attacher::AttachEngine3D
  Height = 1
  Length = 7.5
  Placement = pos=(1,0,0) rot=(0,0,1;1.5708rad)
  Width = 1
FEATURE [Part::Box] Box090  label="Cube090"
  AttacherType = Attacher::AttachEngine3D
  Height = 2
  Length = 7.5
  Placement = pos=(1,0,0) rot=(0,0,1;1.5708rad)
  Width = 1
FEATURE [Part::Box] Box091  label="Cube091"
  AttacherType = Attacher::AttachEngine3D
  Height = 1
  Length = 7.5
  Width = 1
FEATURE [Part::MultiFuse] Fusion019  label="BigArrowLed001"
  Placement = pos=(0,-15,0) rot=(0,0,1;0.785398rad)
  Shapes = -> [Box089,Box091]
FEATURE [App::DocumentObjectGroupPython] FPSimLED040  label="LedUpArrow"  # scripted group (container) (typed FeaturePython)
  Group = -> [Fusion019]
FEATURE [Sketcher::SketchObject] Sketch012
  sketch-geometry (3):
    g0: LineSegment StartX=0 StartY=0 StartZ=0 EndX=18.5 EndY=-18.5 EndZ=0
    g1: LineSegment StartX=-18.5 StartY=-18.5 StartZ=0 EndX=0 EndY=0 EndZ=0
    g2: LineSegment StartX=-18.5 StartY=-18.5 StartZ=0 EndX=18.5 EndY=-18.5 EndZ=0
  constraints (7):
    c: Coincident(g0,g-1)
    c: Coincident(g1,g0)
    c: Coincident(g2,g0)
    c: Coincident(g2,g1)
    c: Symmetric(g0,g1,g-2)
    c: Perpendicular(g1,g0)
    c: DistanceX(g1,g0) = 37
FEATURE [Part::Box] Box092  label="Cube092"
  AttacherType = Attacher::AttachEngine3D
  Height = 2
  Length = 7.5
  Width = 1
FEATURE [Part::MultiFuse] Fusion018  label="BigArrowHole001"
  Placement = pos=(0,-15,0) rot=(0,0,1;0.785398rad)
  Shapes = -> [Box090,Box092]
FEATURE [Part::Extrusion] Extrude001
  Base = -> Sketch012
  Dir = (0,0,1)
  DirMode = 2
  FaceMakerClass = Part::FaceMakerBullseye
  LengthFwd = 1
  LengthRev = 0
  Solid = true
  Symmetric = false
FEATURE [Part::Cut] Cut010
  Base = -> Extrude001
  Tool = -> Fusion018
FEATURE [App::DocumentObjectGroupPython] FPSimButton050  label="BtnUpArrow"  # scripted group (container) (typed FeaturePython)
  Group = -> [Cut010,FPSimLED040]
  PressureResolutionAng = (0,0,0)
  PressureResolutionLin = (0,0,0)
  RotationAngle = 0
  RotationAxis = (0,0,0)
  RotationCenter = (0,0,0)
  SwitchMode = false
  Translation = (0,0,-1)
FEATURE [App::Part] Part064  label="FrUpArrow"
  Group = -> [FPSimLED040,Box089,Box090,Fusion018,Fusion019,Box091,Sketch012,Cut010,Box092,Extrude001,FPSimButton050]
  License = CC BY 3.0
  LicenseURL = http://creativecommons.org/licenses/by/3.0/
  Origin = -> Origin064
  Placement = pos=(0,0.25,0) rot=(0,0,1;3.14159rad)
FEATURE [Part::Box] Box093  label="Cube093"
  AttacherType = Attacher::AttachEngine3D
  Height = 1
  Length = 7.5
  Placement = pos=(1,0,0) rot=(0,0,1;1.5708rad)
  Width = 1
FEATURE [Part::Box] Box094  label="Cube094"
  AttacherType = Attacher::AttachEngine3D
  Height = 2
  Length = 7.5
  Placement = pos=(1,0,0) rot=(0,0,1;1.5708rad)
  Width = 1
FEATURE [Part::Box] Box095  label="Cube095"
  AttacherType = Attacher::AttachEngine3D
  Height = 1
  Length = 7.5
  Width = 1
FEATURE [Part::MultiFuse] Fusion021  label="BigArrowLed002"
  Placement = pos=(0,-15,0) rot=(0,0,1;0.785398rad)
  Shapes = -> [Box093,Box095]
FEATURE [App::DocumentObjectGroupPython] FPSimLED041  label="LedLeftArrow"  # scripted group (container) (typed FeaturePython)
  Group = -> [Fusion021]
FEATURE [Sketcher::SketchObject] Sketch013
  sketch-geometry (3):
    g0: LineSegment StartX=0 StartY=0 StartZ=0 EndX=18.5 EndY=-18.5 EndZ=0
    g1: LineSegment StartX=-18.5 StartY=-18.5 StartZ=0 EndX=0 EndY=0 EndZ=0
    g2: LineSegment StartX=-18.5 StartY=-18.5 StartZ=0 EndX=18.5 EndY=-18.5 EndZ=0
  constraints (7):
    c: Coincident(g0,g-1)
    c: Coincident(g1,g0)
    c: Coincident(g2,g0)
    c: Coincident(g2,g1)
    c: Symmetric(g0,g1,g-2)
    c: Perpendicular(g1,g0)
    c: DistanceX(g1,g0) = 37
FEATURE [Part::Box] Box096  label="Cube096"
  AttacherType = Attacher::AttachEngine3D
  Height = 2
  Length = 7.5
  Width = 1
FEATURE [Part::MultiFuse] Fusion020  label="BigArrowHole002"
  Placement = pos=(0,-15,0) rot=(0,0,1;0.785398rad)
  Shapes = -> [Box094,Box096]
FEATURE [Part::Extrusion] Extrude002
  Base = -> Sketch013
  Dir = (0,0,1)
  DirMode = 2
  FaceMakerClass = Part::FaceMakerBullseye
  LengthFwd = 1
  LengthRev = 0
  Solid = true
  Symmetric = false
FEATURE [Part::Cut] Cut011
  Base = -> Extrude002
  Tool = -> Fusion020
FEATURE [App::DocumentObjectGroupPython] FPSimButton051  label="BtnLeftArrow"  # scripted group (container) (typed FeaturePython)
  Group = -> [Cut011,FPSimLED041]
  PressureResolutionAng = (0,0,0)
  PressureResolutionLin = (0,0,0)
  RotationAngle = 0
  RotationAxis = (0,0,0)
  RotationCenter = (0,0,0)
  SwitchMode = false
  Translation = (0,0,-1)
FEATURE [App::Part] Part065  label="FrLeftArrow"
  Group = -> [FPSimLED041,Box093,Box094,Fusion020,Fusion021,Box095,Sketch013,Cut011,Box096,Extrude002,FPSimButton051]
  License = CC BY 3.0
  LicenseURL = http://creativecommons.org/licenses/by/3.0/
  Origin = -> Origin065
  Placement = pos=(-0.25,0,0) rot=(0,0,1;4.71239rad)
FEATURE [Part::Box] Box097  label="Cube097"
  AttacherType = Attacher::AttachEngine3D
  Height = 1
  Length = 7.5
  Placement = pos=(1,0,0) rot=(0,0,1;1.5708rad)
  Width = 1
FEATURE [Part::Box] Box098  label="Cube098"
  AttacherType = Attacher::AttachEngine3D
  Height = 2
  Length = 7.5
  Placement = pos=(1,0,0) rot=(0,0,1;1.5708rad)
  Width = 1
FEATURE [Part::Box] Box099  label="Cube099"
  AttacherType = Attacher::AttachEngine3D
  Height = 1
  Length = 7.5
  Width = 1
FEATURE [Part::MultiFuse] Fusion023  label="BigArrowLed003"
  Placement = pos=(0,-15,0) rot=(0,0,1;0.785398rad)
  Shapes = -> [Box097,Box099]
FEATURE [App::DocumentObjectGroupPython] FPSimLED042  label="LedRightArrow"  # scripted group (container) (typed FeaturePython)
  Group = -> [Fusion023]
FEATURE [Sketcher::SketchObject] Sketch014
  sketch-geometry (3):
    g0: LineSegment StartX=0 StartY=0 StartZ=0 EndX=18.5 EndY=-18.5 EndZ=0
    g1: LineSegment StartX=-18.5 StartY=-18.5 StartZ=0 EndX=0 EndY=0 EndZ=0
    g2: LineSegment StartX=-18.5 StartY=-18.5 StartZ=0 EndX=18.5 EndY=-18.5 EndZ=0
  constraints (7):
    c: Coincident(g0,g-1)
    c: Coincident(g1,g0)
    c: Coincident(g2,g0)
    c: Coincident(g2,g1)
    c: Symmetric(g0,g1,g-2)
    c: Perpendicular(g1,g0)
    c: DistanceX(g1,g0) = 37
FEATURE [Part::Box] Box100  label="Cube100"
  AttacherType = Attacher::AttachEngine3D
  Height = 2
  Length = 7.5
  Width = 1
FEATURE [Part::MultiFuse] Fusion022  label="BigArrowHole003"
  Placement = pos=(0,-15,0) rot=(0,0,1;0.785398rad)
  Shapes = -> [Box098,Box100]
FEATURE [Part::Extrusion] Extrude003
  Base = -> Sketch014
  Dir = (0,0,1)
  DirMode = 2
  FaceMakerClass = Part::FaceMakerBullseye
  LengthFwd = 1
  LengthRev = 0
  Solid = true
  Symmetric = false
FEATURE [Part::Cut] Cut012
  Base = -> Extrude003
  Tool = -> Fusion022
FEATURE [App::DocumentObjectGroupPython] FPSimButton052  label="BtnRightArrow"  # scripted group (container) (typed FeaturePython)
  Group = -> [Cut012,FPSimLED042]
  PressureResolutionAng = (0,0,0)
  PressureResolutionLin = (0,0,0)
  RotationAngle = 0
  RotationAxis = (0,0,0)
  RotationCenter = (0,0,0)
  SwitchMode = false
  Translation = (0,0,-1)
FEATURE [App::Part] Part066  label="FrRightArrow"
  Group = -> [FPSimLED042,Box097,Box098,Fusion022,Fusion023,Box099,Sketch014,Cut012,Box100,Extrude003,FPSimButton052]
  License = CC BY 3.0
  LicenseURL = http://creativecommons.org/licenses/by/3.0/
  Origin = -> Origin066
  Placement = pos=(0.25,0,0) rot=(0,0,1;1.5708rad)
FEATURE [App::Part] Part067  label="FrNavigArrows"
  Group = -> [Part063,Part064,Part065,Part066]
  License = CC BY 3.0
  LicenseURL = http://creativecommons.org/licenses/by/3.0/
  Origin = -> Origin067
  Placement = pos=(164,31.5,0) rot=(0,0,1;0rad)
FEATURE [Part::Box] Box102  label="Cube102"
  AttacherType = Attacher::AttachEngine3D
  Height = 2
  Length = 3.5
  Width = 1
FEATURE [Part::Box] Box103  label="Cube103"
  AttacherType = Attacher::AttachEngine3D
  Height = 1
  Length = 3.5
  Placement = pos=(1,0,0) rot=(0,0,1;1.5708rad)
  Width = 1
FEATURE [Part::Box] Box104  label="Cube104"
  AttacherType = Attacher::AttachEngine3D
  Height = 2
  Length = 3.5
  Placement = pos=(1,0,0) rot=(0,0,1;1.5708rad)
  Width = 1
FEATURE [Part::Box] Box105  label="Cube105"
  AttacherType = Attacher::AttachEngine3D
  Height = 2
  Length = 3.5
  Width = 1
FEATURE [Part::Box] Box106  label="Cube106"
  AttacherType = Attacher::AttachEngine3D
  Height = 1
  Length = 3.5
  Width = 1
FEATURE [Part::MultiFuse] Fusion025  label="SmallArrowLed004"
  Placement = pos=(0,-8,0) rot=(0,0,1;0.785398rad)
  Shapes = -> [Box103,Box106]
FEATURE [Sketcher::SketchObject] Sketch015
  sketch-geometry (3):
    g0: LineSegment StartX=0 StartY=0 StartZ=0 EndX=18.5 EndY=-18.5 EndZ=0
    g1: LineSegment StartX=-18.5 StartY=-18.5 StartZ=0 EndX=0 EndY=0 EndZ=0
    g2: LineSegment StartX=-18.5 StartY=-18.5 StartZ=0 EndX=18.5 EndY=-18.5 EndZ=0
  constraints (7):
    c: Coincident(g0,g-1)
    c: Coincident(g1,g0)
    c: Coincident(g2,g0)
    c: Coincident(g2,g1)
    c: Symmetric(g0,g1,g-2)
    c: Perpendicular(g1,g0)
    c: DistanceX(g1,g0) = 37
FEATURE [Sketcher::SketchObject] Sketch016
  sketch-geometry (3):
    g0: LineSegment StartX=0 StartY=0 StartZ=0 EndX=18.5 EndY=-18.5 EndZ=0
    g1: LineSegment StartX=-18.5 StartY=-18.5 StartZ=0 EndX=0 EndY=0 EndZ=0
    g2: LineSegment StartX=-18.5 StartY=-18.5 StartZ=0 EndX=18.5 EndY=-18.5 EndZ=0
  constraints (7):
    c: Coincident(g0,g-1)
    c: Coincident(g1,g0)
    c: Coincident(g2,g0)
    c: Coincident(g2,g1)
    c: Symmetric(g0,g1,g-2)
    c: Perpendicular(g1,g0)
    c: DistanceX(g1,g0) = 37
FEATURE [Part::Extrusion] Extrude004
  Base = -> Sketch016
  Dir = (0,0,1)
  DirMode = 2
  FaceMakerClass = Part::FaceMakerBullseye
  LengthFwd = 1
  LengthRev = 0
  Solid = true
  Symmetric = false
FEATURE [Sketcher::SketchObject] Sketch017
  sketch-geometry (3):
    g0: LineSegment StartX=0 StartY=0 StartZ=0 EndX=18.5 EndY=-18.5 EndZ=0
    g1: LineSegment StartX=-18.5 StartY=-18.5 StartZ=0 EndX=0 EndY=0 EndZ=0
    g2: LineSegment StartX=-18.5 StartY=-18.5 StartZ=0 EndX=18.5 EndY=-18.5 EndZ=0
  constraints (7):
    c: Coincident(g0,g-1)
    c: Coincident(g1,g0)
    c: Coincident(g2,g0)
    c: Coincident(g2,g1)
    c: Symmetric(g0,g1,g-2)
    c: Perpendicular(g1,g0)
    c: DistanceX(g1,g0) = 37
FEATURE [Part::Extrusion] Extrude005
  Base = -> Sketch017
  Dir = (0,0,1)
  DirMode = 2
  FaceMakerClass = Part::FaceMakerBullseye
  LengthFwd = 1
  LengthRev = 0
  Solid = true
  Symmetric = false
FEATURE [Part::Box] Box108  label="Cube108"
  AttacherType = Attacher::AttachEngine3D
  Height = 2
  Length = 3.5
  Width = 1
FEATURE [Part::MultiFuse] Fusion024  label="BigArrowHole004"
  Placement = pos=(0,-8,0) rot=(0,0,1;0.785398rad)
  Shapes = -> [Box104,Box108]
FEATURE [Part::Box] Box111  label="Cube111"
  AttacherType = Attacher::AttachEngine3D
  Height = 2
  Length = 3.5
  Placement = pos=(1,0,0) rot=(0,0,1;1.5708rad)
  Width = 1
FEATURE [Part::Extrusion] Extrude006
  Base = -> Sketch015
  Dir = (0,0,1)
  DirMode = 2
  FaceMakerClass = Part::FaceMakerBullseye
  LengthFwd = 1
  LengthRev = 0
  Solid = true
  Symmetric = false
FEATURE [Part::Cut] Cut013
  Base = -> Extrude006
  Tool = -> Fusion024
FEATURE [Sketcher::SketchObject] Sketch018
  sketch-geometry (3):
    g0: LineSegment StartX=0 StartY=0 StartZ=0 EndX=18.5 EndY=-18.5 EndZ=0
    g1: LineSegment StartX=-18.5 StartY=-18.5 StartZ=0 EndX=0 EndY=0 EndZ=0
    g2: LineSegment StartX=-18.5 StartY=-18.5 StartZ=0 EndX=18.5 EndY=-18.5 EndZ=0
  constraints (7):
    c: Coincident(g0,g-1)
    c: Coincident(g1,g0)
    c: Coincident(g2,g0)
    c: Coincident(g2,g1)
    c: Symmetric(g0,g1,g-2)
    c: Perpendicular(g1,g0)
    c: DistanceX(g1,g0) = 37
FEATURE [Part::Box] Box113  label="Cube113"
  AttacherType = Attacher::AttachEngine3D
  Height = 2
  Length = 3.5
  Width = 1
FEATURE [Part::Extrusion] Extrude007
  Base = -> Sketch018
  Dir = (0,0,1)
  DirMode = 2
  FaceMakerClass = Part::FaceMakerBullseye
  LengthFwd = 1
  LengthRev = 0
  Solid = true
  Symmetric = false
FEATURE [Part::Box] Box114  label="Cube114"
  AttacherType = Attacher::AttachEngine3D
  Height = 2
  Length = 3.5
  Placement = pos=(1,0,0) rot=(0,0,1;1.5708rad)
  Width = 1
FEATURE [Part::MultiFuse] Fusion027  label="BigArrowHole005"
  Placement = pos=(0,-8,0) rot=(0,0,1;0.785398rad)
  Shapes = -> [Box114,Box105]
FEATURE [Part::Cut] Cut014
  Base = -> Extrude005
  Tool = -> Fusion027
FEATURE [Part::MultiFuse] Fusion030  label="BigArrowHole006"
  Placement = pos=(0,-8,0) rot=(0,0,1;0.785398rad)
  Shapes = -> [Box111,Box113]
FEATURE [Part::Cut] Cut016
  Base = -> Extrude007
  Tool = -> Fusion030
FEATURE [Part::Box] Box115  label="Cube115"
  AttacherType = Attacher::AttachEngine3D
  Height = 2
  Length = 3.5
  Placement = pos=(1,0,0) rot=(0,0,1;1.5708rad)
  Width = 1
FEATURE [Part::MultiFuse] Fusion031  label="BigArrowHole007"
  Placement = pos=(0,-8,0) rot=(0,0,1;0.785398rad)
  Shapes = -> [Box115,Box102]
FEATURE [Part::Box] Box117  label="LongLedHole"
  AttacherType = Attacher::AttachEngine3D
  Height = 2
  Length = 22
  Placement = pos=(1.5,1,0) rot=(0,0,1;0rad)
  Width = 1.5
FEATURE [Part::Box] Box118  label="LongLed"
  AttacherType = Attacher::AttachEngine3D
  Height = 1
  Length = 22
  Placement = pos=(1.5,1,0) rot=(0,0,1;0rad)
  Width = 1.5
FEATURE [Part::Cut] Cut017
  Base = -> Box003
  Tool = -> Box117
FEATURE [Part::Box] Box119  label="Cube117"
  AttacherType = Attacher::AttachEngine3D
  Height = 1
  Length = 25
  Width = 11
FEATURE [Part::Box] Box120  label="LongLedHole001"
  AttacherType = Attacher::AttachEngine3D
  Height = 2
  Length = 22
  Placement = pos=(1.5,1,0) rot=(0,0,1;0rad)
  Width = 1.5
FEATURE [Part::Cut] Cut018
  Base = -> Box119
  Tool = -> Box120
FEATURE [Part::Box] Box121  label="LongLed001"
  AttacherType = Attacher::AttachEngine3D
  Height = 1
  Length = 22
  Placement = pos=(1.5,1,0) rot=(0,0,1;0rad)
  Width = 1.5
FEATURE [Part::Box] Box122  label="Cube118"
  AttacherType = Attacher::AttachEngine3D
  Height = 1
  Length = 25
  Width = 11
FEATURE [Part::Box] Box123  label="LongLedHole002"
  AttacherType = Attacher::AttachEngine3D
  Height = 2
  Length = 22
  Placement = pos=(1.5,1,0) rot=(0,0,1;0rad)
  Width = 1.5
FEATURE [Part::Cut] Cut019
  Base = -> Box122
  Tool = -> Box123
FEATURE [Part::Box] Box124  label="LongLed002"
  AttacherType = Attacher::AttachEngine3D
  Height = 1
  Length = 22
  Placement = pos=(1.5,1,0) rot=(0,0,1;0rad)
  Width = 1.5
FEATURE [Part::Box] Box125  label="Cube119"
  AttacherType = Attacher::AttachEngine3D
  Height = 1
  Length = 25
  Width = 11
FEATURE [Part::Box] Box126  label="LongLedHole003"
  AttacherType = Attacher::AttachEngine3D
  Height = 2
  Length = 22
  Placement = pos=(1.5,1,0) rot=(0,0,1;0rad)
  Width = 1.5
FEATURE [Part::Cut] Cut020
  Base = -> Box125
  Tool = -> Box126
FEATURE [Part::Box] Box127  label="LongLed003"
  AttacherType = Attacher::AttachEngine3D
  Height = 1
  Length = 22
  Placement = pos=(1.5,1,0) rot=(0,0,1;0rad)
  Width = 1.5
FEATURE [Part::Box] Box128  label="Cube120"
  AttacherType = Attacher::AttachEngine3D
  Height = 1
  Length = 25
  Width = 11
FEATURE [Part::Box] Box129  label="LongLedHole004"
  AttacherType = Attacher::AttachEngine3D
  Height = 2
  Length = 22
  Placement = pos=(1.5,1,0) rot=(0,0,1;0rad)
  Width = 1.5
FEATURE [Part::Cut] Cut021
  Base = -> Box128
  Tool = -> Box129
FEATURE [Part::Box] Box130  label="LongLed004"
  AttacherType = Attacher::AttachEngine3D
  Height = 1
  Length = 22
  Placement = pos=(1.5,1,0) rot=(0,0,1;0rad)
  Width = 1.5
FEATURE [Part::Box] Box131  label="Cube121"
  AttacherType = Attacher::AttachEngine3D
  Height = 1
  Length = 25
  Width = 11
FEATURE [Part::Box] Box132  label="LongLedHole005"
  AttacherType = Attacher::AttachEngine3D
  Height = 2
  Length = 22
  Placement = pos=(1.5,1,0) rot=(0,0,1;0rad)
  Width = 1.5
FEATURE [Part::Cut] Cut022
  Base = -> Box131
  Tool = -> Box132
FEATURE [Part::Box] Box133  label="LongLed005"
  AttacherType = Attacher::AttachEngine3D
  Height = 1
  Length = 22
  Placement = pos=(1.5,1,0) rot=(0,0,1;0rad)
  Width = 1.5
FEATURE [Part::Box] Box134  label="Cube122"
  AttacherType = Attacher::AttachEngine3D
  Height = 1
  Length = 25
  Width = 11
FEATURE [Part::Box] Box135  label="LongLedHole006"
  AttacherType = Attacher::AttachEngine3D
  Height = 2
  Length = 22
  Placement = pos=(1.5,1,0) rot=(0,0,1;0rad)
  Width = 1.5
FEATURE [Part::Cut] Cut023
  Base = -> Box134
  Tool = -> Box135
FEATURE [Part::Box] Box136  label="LongLed006"
  AttacherType = Attacher::AttachEngine3D
  Height = 1
  Length = 22
  Placement = pos=(1.5,1,0) rot=(0,0,1;0rad)
  Width = 1.5
FEATURE [Part::Box] Box137  label="Cube123"
  AttacherType = Attacher::AttachEngine3D
  Height = 1
  Length = 25
  Width = 11
FEATURE [Part::Box] Box138  label="LongLedHole007"
  AttacherType = Attacher::AttachEngine3D
  Height = 2
  Length = 22
  Placement = pos=(1.5,1,0) rot=(0,0,1;0rad)
  Width = 1.5
FEATURE [Part::Cut] Cut024
  Base = -> Box137
  Tool = -> Box138
FEATURE [Part::Box] Box139  label="LongLed007"
  AttacherType = Attacher::AttachEngine3D
  Height = 1
  Length = 22
  Placement = pos=(1.5,1,0) rot=(0,0,1;0rad)
  Width = 1.5
FEATURE [Part::Box] Box140  label="Cube124"
  AttacherType = Attacher::AttachEngine3D
  Height = 1
  Length = 25
  Width = 11
FEATURE [Part::Box] Box141  label="LongLedHole008"
  AttacherType = Attacher::AttachEngine3D
  Height = 2
  Length = 22
  Placement = pos=(1.5,8.5,0) rot=(0,0,1;0rad)
  Width = 1.5
FEATURE [Part::Cut] Cut025
  Base = -> Box140
  Tool = -> Box141
FEATURE [Part::Box] Box142  label="LongLed008"
  AttacherType = Attacher::AttachEngine3D
  Height = 1
  Length = 22
  Placement = pos=(1.5,8.5,0) rot=(0,0,1;0rad)
  Width = 1.5
FEATURE [Part::Box] Box143  label="Cube125"
  AttacherType = Attacher::AttachEngine3D
  Height = 1
  Length = 25
  Width = 11
FEATURE [Part::Box] Box144  label="LongLed009"
  AttacherType = Attacher::AttachEngine3D
  Height = 1
  Length = 22
  Placement = pos=(1.5,8.5,0) rot=(0,0,1;0rad)
  Width = 1.5
FEATURE [Part::Box] Box145  label="LongLedHole009"
  AttacherType = Attacher::AttachEngine3D
  Height = 2
  Length = 22
  Placement = pos=(1.5,8.5,0) rot=(0,0,1;0rad)
  Width = 1.5
FEATURE [Part::Cut] Cut026
  Base = -> Box143
  Tool = -> Box145
FEATURE [Part::Box] Box146  label="Cube126"
  AttacherType = Attacher::AttachEngine3D
  Height = 1
  Length = 25
  Width = 11
FEATURE [Part::Box] Box147  label="LongLed010"
  AttacherType = Attacher::AttachEngine3D
  Height = 1
  Length = 22
  Placement = pos=(1.5,8.5,0) rot=(0,0,1;0rad)
  Width = 1.5
FEATURE [Part::Box] Box148  label="LongLedHole010"
  AttacherType = Attacher::AttachEngine3D
  Height = 2
  Length = 22
  Placement = pos=(1.5,8.5,0) rot=(0,0,1;0rad)
  Width = 1.5
FEATURE [Part::Cut] Cut027
  Base = -> Box146
  Tool = -> Box148
FEATURE [Part::Box] Box149  label="Cube127"
  AttacherType = Attacher::AttachEngine3D
  Height = 1
  Length = 25
  Width = 11
FEATURE [Part::Box] Box150  label="LongLed011"
  AttacherType = Attacher::AttachEngine3D
  Height = 1
  Length = 22
  Placement = pos=(1.5,8.5,0) rot=(0,0,1;0rad)
  Width = 1.5
FEATURE [Part::Box] Box151  label="LongLedHole011"
  AttacherType = Attacher::AttachEngine3D
  Height = 2
  Length = 22
  Placement = pos=(1.5,8.5,0) rot=(0,0,1;0rad)
  Width = 1.5
FEATURE [Part::Cut] Cut028
  Base = -> Box149
  Tool = -> Box151
FEATURE [Part::Box] Box152  label="Cube128"
  AttacherType = Attacher::AttachEngine3D
  Height = 1
  Length = 25
  Width = 11
FEATURE [Part::Box] Box153  label="LongLed012"
  AttacherType = Attacher::AttachEngine3D
  Height = 1
  Length = 22
  Placement = pos=(1.5,8.5,0) rot=(0,0,1;0rad)
  Width = 1.5
FEATURE [Part::Box] Box154  label="LongLedHole012"
  AttacherType = Attacher::AttachEngine3D
  Height = 2
  Length = 22
  Placement = pos=(1.5,8.5,0) rot=(0,0,1;0rad)
  Width = 1.5
FEATURE [Part::Cut] Cut029
  Base = -> Box152
  Tool = -> Box154
FEATURE [Part::Box] Box155  label="Cube129"
  AttacherType = Attacher::AttachEngine3D
  Height = 1
  Length = 25
  Width = 11
FEATURE [Part::Box] Box156  label="LongLed013"
  AttacherType = Attacher::AttachEngine3D
  Height = 1
  Length = 22
  Placement = pos=(1.5,8.5,0) rot=(0,0,1;0rad)
  Width = 1.5
FEATURE [Part::Box] Box157  label="LongLedHole013"
  AttacherType = Attacher::AttachEngine3D
  Height = 2
  Length = 22
  Placement = pos=(1.5,8.5,0) rot=(0,0,1;0rad)
  Width = 1.5
FEATURE [Part::Cut] Cut030
  Base = -> Box155
  Tool = -> Box157
FEATURE [Part::Box] Box158  label="Cube130"
  AttacherType = Attacher::AttachEngine3D
  Height = 1
  Length = 25
  Width = 11
FEATURE [Part::Box] Box159  label="LongLed014"
  AttacherType = Attacher::AttachEngine3D
  Height = 1
  Length = 22
  Placement = pos=(1.5,8.5,0) rot=(0,0,1;0rad)
  Width = 1.5
FEATURE [Part::Box] Box160  label="LongLedHole014"
  AttacherType = Attacher::AttachEngine3D
  Height = 2
  Length = 22
  Placement = pos=(1.5,8.5,0) rot=(0,0,1;0rad)
  Width = 1.5
FEATURE [Part::Cut] Cut031
  Base = -> Box158
  Tool = -> Box160
FEATURE [Part::Box] Box161  label="Cube131"
  AttacherType = Attacher::AttachEngine3D
  Height = 1
  Length = 25
  Width = 11
FEATURE [Part::Box] Box162  label="LongLed015"
  AttacherType = Attacher::AttachEngine3D
  Height = 1
  Length = 22
  Placement = pos=(1.5,8.5,0) rot=(0,0,1;0rad)
  Width = 1.5
FEATURE [Part::Box] Box163  label="LongLedHole015"
  AttacherType = Attacher::AttachEngine3D
  Height = 2
  Length = 22
  Placement = pos=(1.5,8.5,0) rot=(0,0,1;0rad)
  Width = 1.5
FEATURE [Part::Cut] Cut032
  Base = -> Box161
  Tool = -> Box163
FEATURE [Part::Box] Box164  label="Cube132"
  AttacherType = Attacher::AttachEngine3D
  Height = 1
  Length = 19
  Width = 11
FEATURE [Part::Box] Box166  label="Cube134"
  AttacherType = Attacher::AttachEngine3D
  Height = 1
  Length = 19
  Width = 18.5
FEATURE [Part::Box] Box168  label="Cube136"
  AttacherType = Attacher::AttachEngine3D
  Height = 1
  Length = 19
  Width = 11
FEATURE [Part::Box] Box170  label="Cube138"
  AttacherType = Attacher::AttachEngine3D
  Height = 1
  Length = 19
  Width = 18.5
FEATURE [Part::Box] Box172  label="Cube140"
  AttacherType = Attacher::AttachEngine3D
  Height = 1
  Length = 3.5
  Width = 1
FEATURE [Part::Box] Box173  label="Cube141"
  AttacherType = Attacher::AttachEngine3D
  Height = 1
  Length = 3.5
  Placement = pos=(1,0,0) rot=(0,0,1;1.5708rad)
  Width = 1
FEATURE [Part::MultiFuse] Fusion032  label="SmallArrowLed008"
  Placement = pos=(0,-8,0) rot=(0,0,1;0.785398rad)
  Shapes = -> [Box173,Box172]
FEATURE [Part::Box] Box174  label="Cube142"
  AttacherType = Attacher::AttachEngine3D
  Height = 1
  Length = 3.5
  Placement = pos=(1,0,0) rot=(0,0,1;1.5708rad)
  Width = 1
FEATURE [Part::Box] Box175  label="Cube143"
  AttacherType = Attacher::AttachEngine3D
  Height = 1
  Length = 3.5
  Width = 1
FEATURE [Part::MultiFuse] Fusion033  label="SmallArrowLed009"
  Placement = pos=(0,-8,0) rot=(0,0,1;0.785398rad)
  Shapes = -> [Box174,Box175]
FEATURE [Part::Box] Box176  label="Cube144"
  AttacherType = Attacher::AttachEngine3D
  Height = 1
  Length = 3.5
  Placement = pos=(1,0,0) rot=(0,0,1;1.5708rad)
  Width = 1
FEATURE [Part::Box] Box177  label="Cube145"
  AttacherType = Attacher::AttachEngine3D
  Height = 1
  Length = 3.5
  Width = 1
FEATURE [Part::MultiFuse] Fusion034  label="SmallArrowLed010"
  Placement = pos=(0,-8,0) rot=(0,0,1;0.785398rad)
  Shapes = -> [Box176,Box177]
FEATURE [Sketcher::SketchObject] Sketch019
  sketch-geometry (3):
    g0: LineSegment StartX=0 StartY=0 StartZ=0 EndX=18.5 EndY=-18.5 EndZ=0
    g1: LineSegment StartX=-18.5 StartY=-18.5 StartZ=0 EndX=0 EndY=0 EndZ=0
    g2: LineSegment StartX=-18.5 StartY=-18.5 StartZ=0 EndX=18.5 EndY=-18.5 EndZ=0
  constraints (7):
    c: Coincident(g0,g-1)
    c: Coincident(g1,g0)
    c: Coincident(g2,g0)
    c: Coincident(g2,g1)
    c: Symmetric(g0,g1,g-2)
    c: Perpendicular(g1,g0)
    c: DistanceX(g1,g0) = 37
FEATURE [Part::Cut] Cut015
  Base = -> Extrude004
  Tool = -> Fusion031
FEATURE [Part::Box] Box178  label="Cube146"
  AttacherType = Attacher::AttachEngine3D
  Height = 1
  Length = 25
  Width = 18.5
FEATURE [Part::Fillet] Fillet
  Base = -> Box178
  Edges = 8 edges r=0.2: [Edge1,Edge2,Edge3,Edge5,Edge6,Edge7,Edge10,Edge12]
FEATURE [Part::Box] Box179  label="Cube147"
  AttacherType = Attacher::AttachEngine3D
  Height = 1
  Length = 25
  Width = 18.5
FEATURE [Part::Box] Box180  label="Cube148"
  AttacherType = Attacher::AttachEngine3D
  Height = 1
  Length = 25
  Width = 18.5
FEATURE [Part::Box] Box181  label="Cube149"
  AttacherType = Attacher::AttachEngine3D
  Height = 1
  Length = 25
  Width = 18.5
FEATURE [Part::Box] Box182  label="Cube150"
  AttacherType = Attacher::AttachEngine3D
  Height = 1
  Length = 25
  Width = 18.5
FEATURE [Part::Box] Box183  label="Cube151"
  AttacherType = Attacher::AttachEngine3D
  Height = 1
  Length = 25
  Width = 18.5
FEATURE [Part::Box] Box184  label="Cube152"
  AttacherType = Attacher::AttachEngine3D
  Height = 1
  Length = 25
  Width = 18.5
FEATURE [Part::Box] Box185  label="Cube153"
  AttacherType = Attacher::AttachEngine3D
  Height = 1
  Length = 25
  Width = 18.5
FEATURE [Part::Box] Box186  label="Cube154"
  AttacherType = Attacher::AttachEngine3D
  Height = 1
  Length = 25
  Width = 18.5
FEATURE [Part::Box] Box187  label="Cube155"
  AttacherType = Attacher::AttachEngine3D
  Height = 1
  Length = 25
  Width = 18.5
FEATURE [Part::Box] Box188  label="Cube156"
  AttacherType = Attacher::AttachEngine3D
  Height = 1
  Length = 25
  Width = 18.5
FEATURE [Part::Box] Box189  label="Cube157"
  AttacherType = Attacher::AttachEngine3D
  Height = 1
  Length = 25
  Width = 18.5
FEATURE [Part::Box] Box190  label="Cube158"
  AttacherType = Attacher::AttachEngine3D
  Height = 1
  Length = 25
  Width = 18.5
FEATURE [Part::Box] Box191  label="Cube159"
  AttacherType = Attacher::AttachEngine3D
  Height = 1
  Length = 25
  Width = 18.5
FEATURE [Part::Box] Box192  label="Cube160"
  AttacherType = Attacher::AttachEngine3D
  Height = 1
  Length = 25
  Width = 18.5
FEATURE [Part::Box] Box193  label="Cube161"
  AttacherType = Attacher::AttachEngine3D
  Height = 1
  Length = 25
  Width = 18.5
FEATURE [Part::Box] Box194  label="Cube162"
  AttacherType = Attacher::AttachEngine3D
  Height = 1
  Length = 25
  Width = 18.5
FEATURE [Part::Box] Box195  label="Cube163"
  AttacherType = Attacher::AttachEngine3D
  Height = 1
  Length = 25
  Width = 18.5
FEATURE [Part::Box] Box196  label="Cube164"
  AttacherType = Attacher::AttachEngine3D
  Height = 1
  Length = 25
  Width = 18.5
FEATURE [Part::Box] Box197  label="Cube165"
  AttacherType = Attacher::AttachEngine3D
  Height = 1
  Length = 25
  Width = 18.5
FEATURE [Part::Box] Box198  label="Cube166"
  AttacherType = Attacher::AttachEngine3D
  Height = 1
  Length = 25
  Width = 18.5
FEATURE [Part::Box] Box199  label="Cube167"
  AttacherType = Attacher::AttachEngine3D
  Height = 1
  Length = 25
  Width = 18.5
FEATURE [Part::Box] Box200  label="Cube168"
  AttacherType = Attacher::AttachEngine3D
  Height = 1
  Length = 25
  Width = 18.5
FEATURE [Part::Box] Box201  label="Cube169"
  AttacherType = Attacher::AttachEngine3D
  Height = 1
  Length = 25
  Width = 18.5
FEATURE [Part::Box] Box202  label="Cube170"
  AttacherType = Attacher::AttachEngine3D
  Height = 1
  Length = 25
  Width = 18.5
FEATURE [Part::Box] Box203  label="Cube171"
  AttacherType = Attacher::AttachEngine3D
  Height = 1
  Length = 25
  Width = 18.5
FEATURE [Part::Box] Box204  label="Cube172"
  AttacherType = Attacher::AttachEngine3D
  Height = 1
  Length = 25
  Width = 18.5
FEATURE [Part::Box] Box205  label="Cube173"
  AttacherType = Attacher::AttachEngine3D
  Height = 1
  Length = 25
  Width = 18.5
FEATURE [Part::Box] Box206  label="Cube174"
  AttacherType = Attacher::AttachEngine3D
  Height = 1
  Length = 25
  Width = 18.5
FEATURE [Part::Box] Box207  label="Cube175"
  AttacherType = Attacher::AttachEngine3D
  Height = 1
  Length = 25
  Width = 18.5
FEATURE [Part::Box] Box208  label="Cube176"
  AttacherType = Attacher::AttachEngine3D
  Height = 1
  Length = 25
  Width = 18.5
FEATURE [Part::Box] Box209  label="Cube177"
  AttacherType = Attacher::AttachEngine3D
  Height = 1
  Length = 25
  Width = 18.5
FEATURE [Part::Box] Box210  label="Cube178"
  AttacherType = Attacher::AttachEngine3D
  Height = 1
  Length = 25
  Width = 18.5
FEATURE [Part::Box] Box211  label="Cube179"
  AttacherType = Attacher::AttachEngine3D
  Height = 1
  Length = 25
  Width = 18.5
FEATURE [Part::Box] Box212  label="Cube180"
  AttacherType = Attacher::AttachEngine3D
  Height = 1
  Length = 25
  Width = 18.5
FEATURE [Part::Box] Box213  label="Cube181"
  AttacherType = Attacher::AttachEngine3D
  Height = 1
  Length = 25
  Width = 18.5
FEATURE [Part::Box] Box214  label="Cube182"
  AttacherType = Attacher::AttachEngine3D
  Height = 1
  Length = 25
  Width = 18.5
FEATURE [Part::Box] Box215  label="Cube183"
  AttacherType = Attacher::AttachEngine3D
  Height = 1
  Length = 25
  Width = 18.5
FEATURE [Part::Box] Box216  label="Cube184"
  AttacherType = Attacher::AttachEngine3D
  Height = 1
  Length = 25
  Width = 18.5
FEATURE [Part::Box] Box217  label="Cube185"
  AttacherType = Attacher::AttachEngine3D
  Height = 1
  Length = 25
  Width = 18.5
FEATURE [Part::Box] Box218  label="Cube186"
  AttacherType = Attacher::AttachEngine3D
  Height = 1
  Length = 25
  Width = 18.5
FEATURE [Part::Box] Box219  label="Cube187"
  AttacherType = Attacher::AttachEngine3D
  Height = 1
  Length = 25
  Width = 18.5
FEATURE [Part::Box] Box220  label="Cube188"
  AttacherType = Attacher::AttachEngine3D
  Height = 1
  Length = 25
  Width = 18.5
FEATURE [Part::Box] Box221  label="Cube189"
  AttacherType = Attacher::AttachEngine3D
  Height = 1
  Length = 25
  Width = 18.5
FEATURE [Part::Box] Box222  label="Cube190"
  AttacherType = Attacher::AttachEngine3D
  Height = 1
  Length = 25
  Width = 18.5
FEATURE [Part::Box] Box223  label="Cube191"
  AttacherType = Attacher::AttachEngine3D
  Height = 1
  Length = 25
  Width = 18.5
FEATURE [Part::Box] Box224  label="Cube192"
  AttacherType = Attacher::AttachEngine3D
  Height = 1
  Length = 25
  Width = 18.5
FEATURE [Part::Box] Box225  label="Cube193"
  AttacherType = Attacher::AttachEngine3D
  Height = 1
  Length = 25
  Width = 18.5
FEATURE [Part::Box] Box226  label="Cube194"
  AttacherType = Attacher::AttachEngine3D
  Height = 1
  Length = 25
  Width = 18.5
FEATURE [Part::Box] Box227  label="Cube195"
  AttacherType = Attacher::AttachEngine3D
  Height = 1
  Length = 25
  Width = 18.5
FEATURE [Part::Box] Box228  label="Cube196"
  AttacherType = Attacher::AttachEngine3D
  Height = 1
  Length = 25
  Width = 18.5
FEATURE [Part::Box] Box229  label="Cube197"
  AttacherType = Attacher::AttachEngine3D
  Height = 1
  Length = 25
  Width = 18.5
FEATURE [Part::Box] Box230  label="Cube198"
  AttacherType = Attacher::AttachEngine3D
  Height = 1
  Length = 25
  Width = 18.5
FEATURE [Part::Box] Box231  label="Cube199"
  AttacherType = Attacher::AttachEngine3D
  Height = 1
  Length = 25
  Width = 18.5
FEATURE [Part::Box] Box232  label="Cube200"
  AttacherType = Attacher::AttachEngine3D
  Height = 1
  Length = 25
  Width = 18.5
FEATURE [Part::Box] Box233  label="Cube201"
  AttacherType = Attacher::AttachEngine3D
  Height = 1
  Length = 25
  Width = 18.5
FEATURE [Part::Box] Box234  label="Cube202"
  AttacherType = Attacher::AttachEngine3D
  Height = 1
  Length = 25
  Width = 18.5
FEATURE [Part::Box] Box235  label="Cube203"
  AttacherType = Attacher::AttachEngine3D
  Height = 1
  Length = 25
  Width = 18.5
FEATURE [Part::Box] Box236  label="Cube204"
  AttacherType = Attacher::AttachEngine3D
  Height = 1
  Length = 25
  Width = 18.5
FEATURE [Part::Box] Box237  label="Cube205"
  AttacherType = Attacher::AttachEngine3D
  Height = 1
  Length = 25
  Width = 18.5
FEATURE [Part::Box] Box238  label="Cube206"
  AttacherType = Attacher::AttachEngine3D
  Height = 1
  Length = 25
  Width = 18.5
FEATURE [Part::Box] Box239  label="Cube207"
  AttacherType = Attacher::AttachEngine3D
  Height = 1
  Length = 25
  Width = 18.5
FEATURE [Part::Box] Box240  label="Cube208"
  AttacherType = Attacher::AttachEngine3D
  Height = 1
  Length = 25
  Width = 18.5
FEATURE [Part::Box] Box241  label="Cube209"
  AttacherType = Attacher::AttachEngine3D
  Height = 1
  Length = 25
  Width = 18.5
FEATURE [Part::Part2DObjectPython] ShapeString  # Draft 2D object (typed FeaturePython)
  FontFile = <path>
  Placement = pos=(1,6,0) rot=(0,0,1;0rad)
  Size = 3
  String = Tap Tempo
  Tracking = 0
FEATURE [Part::Extrusion] Extrude008  label="TxtHole"
  Base = -> ShapeString
  Dir = (0,0,1)
  DirMode = 2
  FaceMakerClass = Part::FaceMakerBullseye
  LengthFwd = 2
  LengthRev = 1
  Solid = true
  Symmetric = false
FEATURE [Part::Part2DObjectPython] ShapeString001  # Draft 2D object (typed FeaturePython)
  FontFile = <path>
  Placement = pos=(1,6,0) rot=(0,0,1;0rad)
  Size = 3
  String = Tap Tempo
  Tracking = 0
FEATURE [Part::Extrusion] Extrude009  label="Txt"
  Base = -> ShapeString001
  Dir = (0,0,1)
  DirMode = 2
  FaceMakerClass = Part::FaceMakerBullseye
  LengthFwd = 1
  LengthRev = 0
  Solid = true
  Symmetric = false
FEATURE [Part::Cut] Cut033
  Base = -> Box001
  Tool = -> Extrude008
FEATURE [App::DocumentObjectGroupPython] FPSimLED111  label="LedTapTempo"  # scripted group (container) (typed FeaturePython)
  Group = -> [Extrude009]
FEATURE [App::DocumentObjectGroupPython] FPSimButton  label="BtnTapTempo"  # scripted group (container) (typed FeaturePython)
  Group = -> [ShapeString,Cut033,FPSimLED111]
  RotationAngle = 0
  RotationAxis = (0,0,0)
  RotationCenter = (0,0,0)
  SwitchMode = false
  Translation = (0,0,-0.8)
FEATURE [App::Part] Part012  label="FrBtnTapTempo"
  Group = -> [Box001,FPSimButton,ShapeString,Extrude008,Cut033,Extrude009,ShapeString001,FPSimLED111]
  License = CC BY 3.0
  LicenseURL = http://creativecommons.org/licenses/by/3.0/
  Origin = -> Origin
  Placement = pos=(-181.9,112.2,0) rot=(0,0,1;0rad)
FEATURE [Part::Part2DObjectPython] ShapeString002  # Draft 2D object (typed FeaturePython)
  FontFile = <path>
  Placement = pos=(1,6,0) rot=(0,0,1;0rad)
  Size = 3
  String = Metronome
  Tracking = 0
FEATURE [Part::Extrusion] Extrude010  label="TxtHole001"
  Base = -> ShapeString002
  Dir = (0,0,1)
  DirMode = 2
  FaceMakerClass = Part::FaceMakerBullseye
  LengthFwd = 2
  LengthRev = 1
  Solid = true
  Symmetric = false
FEATURE [Part::Box] Box242  label="Cube210"
  AttacherType = Attacher::AttachEngine3D
  Height = 1
  Length = 25
  Width = 11
FEATURE [Part::Cut] Cut034
  Base = -> Box242
  Tool = -> Extrude010
FEATURE [Part::Part2DObjectPython] ShapeString003  # Draft 2D object (typed FeaturePython)
  FontFile = <path>
  Placement = pos=(1,6,0) rot=(0,0,1;0rad)
  Size = 3
  String = Metronome
  Tracking = 0
FEATURE [Part::Extrusion] Extrude011  label="Txt001"
  Base = -> ShapeString003
  Dir = (0,0,1)
  DirMode = 2
  FaceMakerClass = Part::FaceMakerBullseye
  LengthFwd = 1
  LengthRev = 0
  Solid = true
  Symmetric = false
FEATURE [App::DocumentObjectGroupPython] FPSimLED112  label="LedMetronome"  # scripted group (container) (typed FeaturePython)
  Group = -> [Extrude011]
FEATURE [App::DocumentObjectGroupPython] FPSimButton001  label="BtnMetronome"  # scripted group (container) (typed FeaturePython)
  Group = -> [FPSimLED112,Cut034]
  RotationAngle = 0
  RotationAxis = (0,0,0)
  RotationCenter = (0,0,0)
  SwitchMode = false
  Translation = (0,0,-0.8)
FEATURE [App::Part] Part013  label="FrBtnMetronome"
  Group = -> [FPSimButton001,Extrude011,ShapeString003,FPSimLED112,Box242,ShapeString002,Extrude010,Cut034]
  License = CC BY 3.0
  LicenseURL = http://creativecommons.org/licenses/by/3.0/
  Origin = -> Origin013
  Placement = pos=(-155.9,112.2,0) rot=(0,0,1;0rad)
FEATURE [Part::Part2DObjectPython] ShapeString004  # Draft 2D object (typed FeaturePython)
  FontFile = <path>
  Placement = pos=(1,13,0) rot=(0,0,1;0rad)
  Size = 3
  String = Delete
  Tracking = 0
FEATURE [Part::Extrusion] Extrude012  label="Txt002"
  Base = -> ShapeString004
  Dir = (0,0,1)
  DirMode = 2
  FaceMakerClass = Part::FaceMakerBullseye
  LengthFwd = 1
  LengthRev = 0
  Solid = true
  Symmetric = false
FEATURE [App::DocumentObjectGroupPython] FPSimLED113  label="LedDelete"  # scripted group (container) (typed FeaturePython)
  Group = -> [Extrude012]
FEATURE [Part::Part2DObjectPython] ShapeString005  # Draft 2D object (typed FeaturePython)
  FontFile = <path>
  Placement = pos=(1,13,0) rot=(0,0,1;0rad)
  Size = 3
  String = Delete
  Tracking = 0
FEATURE [Part::Extrusion] Extrude013  label="Txt003"
  Base = -> ShapeString005
  Dir = (0,0,1)
  DirMode = 2
  FaceMakerClass = Part::FaceMakerBullseye
  LengthFwd = 2
  LengthRev = 1
  Solid = true
  Symmetric = false
FEATURE [Part::Cut] Cut035
  Base = -> Box013
  Tool = -> Extrude013
FEATURE [App::DocumentObjectGroupPython] FPSimButton012  label="BtnDelete"  # scripted group (container) (typed FeaturePython)
  Group = -> [FPSimLED113,Cut035]
  PressureResolutionAng = (0,0,0)
  PressureResolutionLin = (0,0,0)
  RotationAngle = 0
  RotationAxis = (0,0,0)
  RotationCenter = (0,0,0)
  SwitchMode = false
  Translation = (0,0,-1)
FEATURE [App::Part] Part024  label="FrBtnDelete"
  Group = -> [Box013,FPSimButton012,Extrude012,ShapeString004,FPSimLED113,ShapeString005,Extrude013,Cut035]
  License = CC BY 3.0
  LicenseURL = http://creativecommons.org/licenses/by/3.0/
  Origin = -> Origin024
  Placement = pos=(-182,82,0) rot=(0,0,1;0rad)
FEATURE [Part::Part2DObjectPython] ShapeString006  # Draft 2D object (typed FeaturePython)
  FontFile = <path>
  Placement = pos=(1,13,0) rot=(0,0,1;0rad)
  Size = 3
  String = Undo
  Tracking = 0
FEATURE [Part::Box] Box243  label="Cube211"
  AttacherType = Attacher::AttachEngine3D
  Height = 1
  Length = 18.5
  Width = 18.5
FEATURE [Part::Extrusion] Extrude015  label="Txt005"
  Base = -> ShapeString006
  Dir = (0,0,1)
  DirMode = 2
  FaceMakerClass = Part::FaceMakerBullseye
  LengthFwd = 2
  LengthRev = 1
  Solid = true
  Symmetric = false
FEATURE [Part::Part2DObjectPython] ShapeString007  # Draft 2D object (typed FeaturePython)
  FontFile = <path>
  Placement = pos=(1,13,0) rot=(0,0,1;0rad)
  Size = 3
  String = Undo
  Tracking = 0
FEATURE [Part::Extrusion] Extrude014  label="Txt004"
  Base = -> ShapeString007
  Dir = (0,0,1)
  DirMode = 2
  FaceMakerClass = Part::FaceMakerBullseye
  LengthFwd = 1
  LengthRev = 0
  Solid = true
  Symmetric = false
FEATURE [App::DocumentObjectGroupPython] FPSimLED114  label="LedUndo"  # scripted group (container) (typed FeaturePython)
  Group = -> [Extrude014]
FEATURE [Part::Cut] Cut036
  Base = -> Box243
  Tool = -> Extrude015
FEATURE [App::DocumentObjectGroupPython] FPSimButton013  label="BtnUndo"  # scripted group (container) (typed FeaturePython)
  Group = -> [Cut036,FPSimLED114]
  PressureResolutionAng = (0,0,0)
  PressureResolutionLin = (0,0,0)
  RotationAngle = 0
  RotationAxis = (0,0,0)
  RotationCenter = (0,0,0)
  SwitchMode = false
  Translation = (0,0,-1)
FEATURE [App::Part] Part025  label="FrBtnUndo"
  Group = -> [FPSimButton013,ShapeString006,Box243,Extrude015,Cut036,ShapeString007,Extrude014,FPSimLED114]
  License = CC BY 3.0
  LicenseURL = http://creativecommons.org/licenses/by/3.0/
  Origin = -> Origin025
  Placement = pos=(-182,63,0) rot=(0,0,1;0rad)
FEATURE [Part::Part2DObjectPython] ShapeString008  # Draft 2D object (typed FeaturePython)
  FontFile = <path>
  Placement = pos=(1,6,0) rot=(0,0,1;0rad)
  Size = 3
  String = Mute
  Tracking = 0
FEATURE [Part::Extrusion] Extrude016  label="Txt006"
  Base = -> ShapeString008
  Dir = (0,0,1)
  DirMode = 2
  FaceMakerClass = Part::FaceMakerBullseye
  LengthFwd = 1
  LengthRev = 0
  Solid = true
  Symmetric = false
FEATURE [App::DocumentObjectGroupPython] FPSimLED115  label="LedMute"  # scripted group (container) (typed FeaturePython)
  Group = -> [Extrude016]
FEATURE [Part::Part2DObjectPython] ShapeString009  # Draft 2D object (typed FeaturePython)
  FontFile = <path>
  Placement = pos=(1,6,0) rot=(0,0,1;0rad)
  Size = 3
  String = Mute
  Tracking = 0
FEATURE [Part::Extrusion] Extrude017  label="Txt007"
  Base = -> ShapeString009
  Dir = (0,0,1)
  DirMode = 2
  FaceMakerClass = Part::FaceMakerBullseye
  LengthFwd = 2
  LengthRev = 1
  Solid = true
  Symmetric = false
FEATURE [Part::Cut] Cut037
  Base = -> Box022
  Tool = -> Extrude017
FEATURE [App::DocumentObjectGroupPython] FPSimButton020  label="BtnMute"  # scripted group (container) (typed FeaturePython)
  Group = -> [FPSimLED115,Cut037]
  PressureResolutionAng = (0,0,0)
  PressureResolutionLin = (0,0,0)
  RotationAngle = 0
  RotationAxis = (0,0,0)
  RotationCenter = (0,0,0)
  SwitchMode = false
  Translation = (0,0,-1)
FEATURE [App::Part] Part033  label="FrBtnMute"
  Group = -> [Box022,FPSimButton020,Extrude016,ShapeString008,FPSimLED115,ShapeString009,Extrude017,Cut037]
  License = CC BY 3.0
  LicenseURL = http://creativecommons.org/licenses/by/3.0/
  Origin = -> Origin033
  Placement = pos=(-182,40,0) rot=(0,0,1;0rad)
FEATURE [Part::Box] Box244  label="Cube212"
  AttacherType = Attacher::AttachEngine3D
  Height = 1
  Length = 17
  Width = 10
FEATURE [Part::Part2DObjectPython] ShapeString010  # Draft 2D object (typed FeaturePython)
  FontFile = <path>
  Placement = pos=(1,6,0) rot=(0,0,1;0rad)
  Size = 3
  String = Solo
  Tracking = 0
FEATURE [Part::Extrusion] Extrude019  label="Txt009"
  Base = -> ShapeString010
  Dir = (0,0,1)
  DirMode = 2
  FaceMakerClass = Part::FaceMakerBullseye
  LengthFwd = 1
  LengthRev = 0
  Solid = true
  Symmetric = false
FEATURE [App::DocumentObjectGroupPython] FPSimLED116  label="LedSolo"  # scripted group (container) (typed FeaturePython)
  Group = -> [Extrude019]
FEATURE [Part::Part2DObjectPython] ShapeString011  # Draft 2D object (typed FeaturePython)
  FontFile = <path>
  Placement = pos=(1,6,0) rot=(0,0,1;0rad)
  Size = 3
  String = Solo
  Tracking = 0
FEATURE [Part::Extrusion] Extrude018  label="Txt008"
  Base = -> ShapeString011
  Dir = (0,0,1)
  DirMode = 2
  FaceMakerClass = Part::FaceMakerBullseye
  LengthFwd = 2
  LengthRev = 1
  Solid = true
  Symmetric = false
FEATURE [Part::Cut] Cut038
  Base = -> Box244
  Tool = -> Extrude018
FEATURE [App::DocumentObjectGroupPython] FPSimButton021  label="BtnSolo"  # scripted group (container) (typed FeaturePython)
  Group = -> [FPSimLED116,Cut038]
  PressureResolutionAng = (0,0,0)
  PressureResolutionLin = (0,0,0)
  RotationAngle = 0
  RotationAxis = (0,0,0)
  RotationCenter = (0,0,0)
  SwitchMode = false
  Translation = (0,0,-1)
FEATURE [App::Part] Part034  label="FrBtnSolo"
  Group = -> [FPSimButton021,ShapeString010,Extrude019,FPSimLED116,Extrude018,Box244,ShapeString011,Cut038]
  License = CC BY 3.0
  LicenseURL = http://creativecommons.org/licenses/by/3.0/
  Origin = -> Origin034
  Placement = pos=(-165,40,0) rot=(0,0,1;0rad)
FEATURE [Part::Box] Box245  label="Cube213"
  AttacherType = Attacher::AttachEngine3D
  Height = 1
  Length = 17
  Width = 10
FEATURE [Part::Part2DObjectPython] ShapeString012  # Draft 2D object (typed FeaturePython)
  FontFile = <path>
  Placement = pos=(1,6,0) rot=(0,0,1;0rad)
  Size = 3
  String = Stop
  Tracking = 0
FEATURE [Part::Part2DObjectPython] ShapeString013  # Draft 2D object (typed FeaturePython)
  FontFile = <path>
  Placement = pos=(1,6,0) rot=(0,0,1;0rad)
  Size = 3
  String = Stop
  Tracking = 0
FEATURE [Part::Extrusion] Extrude020  label="Txt010"
  Base = -> ShapeString013
  Dir = (0,0,1)
  DirMode = 2
  FaceMakerClass = Part::FaceMakerBullseye
  LengthFwd = 2
  LengthRev = 1
  Solid = true
  Symmetric = false
FEATURE [Part::Cut] Cut039
  Base = -> Box245
  Tool = -> Extrude020
FEATURE [Part::Extrusion] Extrude021  label="Txt011"
  Base = -> ShapeString012
  Dir = (0,0,1)
  DirMode = 2
  FaceMakerClass = Part::FaceMakerBullseye
  LengthFwd = 1
  LengthRev = 0
  Solid = true
  Symmetric = false
FEATURE [Part::Part2DObjectPython] ShapeString014  # Draft 2D object (typed FeaturePython)
  FontFile = <path>
  Placement = pos=(1,3,0) rot=(0,0,1;0rad)
  Size = 3
  String = Clip
  Tracking = 0
FEATURE [Part::Extrusion] Extrude022  label="Txt012"
  Base = -> ShapeString014
  Dir = (0,0,1)
  DirMode = 2
  FaceMakerClass = Part::FaceMakerBullseye
  LengthFwd = 1
  LengthRev = 0
  Solid = true
  Symmetric = false
FEATURE [App::DocumentObjectGroupPython] FPSimLED117  label="LedStopClip"  # scripted group (container) (typed FeaturePython)
  Group = -> [Extrude021,Extrude022]
FEATURE [Part::Part2DObjectPython] ShapeString015  # Draft 2D object (typed FeaturePython)
  FontFile = <path>
  Placement = pos=(1,3,0) rot=(0,0,1;0rad)
  Size = 3
  String = Clip
  Tracking = 0
FEATURE [Part::Extrusion] Extrude023  label="Txt013"
  Base = -> ShapeString015
  Dir = (0,0,1)
  DirMode = 2
  FaceMakerClass = Part::FaceMakerBullseye
  LengthFwd = 2
  LengthRev = 1
  Solid = true
  Symmetric = false
FEATURE [Part::Cut] Cut040
  Base = -> Cut039
  Tool = -> Extrude023
FEATURE [App::DocumentObjectGroupPython] FPSimButton022  label="BtnStopClip"  # scripted group (container) (typed FeaturePython)
  Group = -> [FPSimLED117,Cut040]
  PressureResolutionAng = (0,0,0)
  PressureResolutionLin = (0,0,0)
  RotationAngle = 0
  RotationAxis = (0,0,0)
  RotationCenter = (0,0,0)
  SwitchMode = false
  Translation = (0,0,-1)
FEATURE [App::Part] Part035  label="FrBtnStopClip"
  Group = -> [FPSimButton022,Box245,ShapeString013,Extrude020,Cut039,ShapeString012,Extrude021,FPSimLED117,ShapeString014,Extrude022,ShapeString015,Extrude023,Cut040]
  License = CC BY 3.0
  LicenseURL = http://creativecommons.org/licenses/by/3.0/
  Origin = -> Origin035
  Placement = pos=(-148,40,0) rot=(0,0,1;0rad)
FEATURE [Part::Part2DObjectPython] ShapeString016  # Draft 2D object (typed FeaturePython)
  FontFile = <path>
  Placement = pos=(1,13,0) rot=(0,0,1;0rad)
  Size = 3
  String = Convert
  Tracking = 0
FEATURE [Part::Extrusion] Extrude024  label="Txt014"
  Base = -> ShapeString016
  Dir = (0,0,1)
  DirMode = 2
  FaceMakerClass = Part::FaceMakerBullseye
  LengthFwd = 1
  LengthRev = 0
  Solid = true
  Symmetric = false
FEATURE [App::DocumentObjectGroupPython] FPSimLED118  label="LedConvert"  # scripted group (container) (typed FeaturePython)
  Group = -> [Extrude024]
FEATURE [Part::Part2DObjectPython] ShapeString017  # Draft 2D object (typed FeaturePython)
  FontFile = <path>
  Placement = pos=(1,13,0) rot=(0,0,1;0rad)
  Size = 3
  String = Convert
  Tracking = 0
FEATURE [Part::Extrusion] Extrude025  label="Txt015"
  Base = -> ShapeString017
  Dir = (0,0,1)
  DirMode = 2
  FaceMakerClass = Part::FaceMakerBullseye
  LengthFwd = 2
  LengthRev = 1
  Solid = true
  Symmetric = false
FEATURE [Part::Cut] Cut041
  Base = -> Box025
  Tool = -> Extrude025
FEATURE [App::DocumentObjectGroupPython] FPSimButton023  label="BtnConvert"  # scripted group (container) (typed FeaturePython)
  Group = -> [FPSimLED118,Cut041]
  PressureResolutionAng = (0,0,0)
  PressureResolutionLin = (0,0,0)
  RotationAngle = 0
  RotationAxis = (0,0,0)
  RotationCenter = (0,0,0)
  SwitchMode = false
  Translation = (0,0,-1)
FEATURE [App::Part] Part036  label="FrBtnConvert"
  Group = -> [Box025,FPSimButton023,Extrude024,ShapeString016,FPSimLED118,ShapeString017,Extrude025,Cut041]
  License = CC BY 3.0
  LicenseURL = http://creativecommons.org/licenses/by/3.0/
  Origin = -> Origin036
  Placement = pos=(-182,13,0) rot=(0,0,1;0rad)
FEATURE [Part::Box] Box246  label="Cube214"
  AttacherType = Attacher::AttachEngine3D
  Height = 1
  Length = 18.5
  Width = 18.5
FEATURE [Part::Part2DObjectPython] ShapeString018  # Draft 2D object (typed FeaturePython)
  FontFile = <path>
  Placement = pos=(1,13,0) rot=(0,0,1;0rad)
  Size = 3
  String = Double
  Tracking = 0
FEATURE [Part::Extrusion] Extrude026  label="Txt016"
  Base = -> ShapeString018
  Dir = (0,0,1)
  DirMode = 2
  FaceMakerClass = Part::FaceMakerBullseye
  LengthFwd = 1
  LengthRev = 0
  Solid = true
  Symmetric = false
FEATURE [Part::Part2DObjectPython] ShapeString019  # Draft 2D object (typed FeaturePython)
  FontFile = <path>
  Placement = pos=(1,13,0) rot=(0,0,1;0rad)
  Size = 3
  String = Double
  Tracking = 0
FEATURE [Part::Extrusion] Extrude027  label="Txt017"
  Base = -> ShapeString019
  Dir = (0,0,1)
  DirMode = 2
  FaceMakerClass = Part::FaceMakerBullseye
  LengthFwd = 2
  LengthRev = 1
  Solid = true
  Symmetric = false
FEATURE [Part::Cut] Cut042
  Base = -> Box246
  Tool = -> Extrude027
FEATURE [Part::Part2DObjectPython] ShapeString020  # Draft 2D object (typed FeaturePython)
  FontFile = <path>
  Placement = pos=(1,10,0) rot=(0,0,1;0rad)
  Size = 3
  String = Loop
  Tracking = 0
FEATURE [Part::Extrusion] Extrude028  label="Txt018"
  Base = -> ShapeString020
  Dir = (0,0,1)
  DirMode = 2
  FaceMakerClass = Part::FaceMakerBullseye
  LengthFwd = 1
  LengthRev = 0
  Solid = true
  Symmetric = false
FEATURE [App::DocumentObjectGroupPython] FPSimLED119  label="LedDoubleLoop"  # scripted group (container) (typed FeaturePython)
  Group = -> [Extrude026,Extrude028]
FEATURE [Part::Part2DObjectPython] ShapeString021  # Draft 2D object (typed FeaturePython)
  FontFile = <path>
  Placement = pos=(1,10,0) rot=(0,0,1;0rad)
  Size = 3
  String = Loop
  Tracking = 0
FEATURE [Part::Extrusion] Extrude029  label="Txt019"
  Base = -> ShapeString021
  Dir = (0,0,1)
  DirMode = 2
  FaceMakerClass = Part::FaceMakerBullseye
  LengthFwd = 2
  LengthRev = 1
  Solid = true
  Symmetric = false
FEATURE [Part::Cut] Cut043
  Base = -> Cut042
  Tool = -> Extrude029
FEATURE [App::DocumentObjectGroupPython] FPSimButton024  label="BtnDoubleLoop"  # scripted group (container) (typed FeaturePython)
  Group = -> [FPSimLED119,Cut043]
  PressureResolutionAng = (0,0,0)
  PressureResolutionLin = (0,0,0)
  RotationAngle = 0
  RotationAxis = (0,0,0)
  RotationCenter = (0,0,0)
  SwitchMode = false
  Translation = (0,0,-1)
FEATURE [App::Part] Part037  label="FrBtnDoubleLoop"
  Group = -> [FPSimButton024,Extrude027,Box246,ShapeString019,Cut042,ShapeString018,Extrude026,FPSimLED119,ShapeString020,Extrude028,ShapeString021,Extrude029,Cut043]
  License = CC BY 3.0
  LicenseURL = http://creativecommons.org/licenses/by/3.0/
  Origin = -> Origin037
  Placement = pos=(-182,-5.5,0) rot=(0,0,1;0rad)
FEATURE [Part::Box] Box247  label="Cube215"
  AttacherType = Attacher::AttachEngine3D
  Height = 1
  Length = 18.5
  Width = 18.5
FEATURE [Part::Part2DObjectPython] ShapeString022  # Draft 2D object (typed FeaturePython)
  FontFile = <path>
  Placement = pos=(1,13,0) rot=(0,0,1;0rad)
  Size = 3
  String = Quantize
  Tracking = 0
FEATURE [Part::Extrusion] Extrude030  label="Txt020"
  Base = -> ShapeString022
  Dir = (0,0,1)
  DirMode = 2
  FaceMakerClass = Part::FaceMakerBullseye
  LengthFwd = 1
  LengthRev = 0
  Solid = true
  Symmetric = false
FEATURE [App::DocumentObjectGroupPython] FPSimLED120  label="LedQuantize"  # scripted group (container) (typed FeaturePython)
  Group = -> [Extrude030]
FEATURE [Part::Part2DObjectPython] ShapeString023  # Draft 2D object (typed FeaturePython)
  FontFile = <path>
  Placement = pos=(1,13,0) rot=(0,0,1;0rad)
  Size = 3
  String = Quantize
  Tracking = 0
FEATURE [Part::Extrusion] Extrude031  label="Txt021"
  Base = -> ShapeString023
  Dir = (0,0,1)
  DirMode = 2
  FaceMakerClass = Part::FaceMakerBullseye
  LengthFwd = 2
  LengthRev = 1
  Solid = true
  Symmetric = false
FEATURE [Part::Cut] Cut044
  Base = -> Box247
  Tool = -> Extrude031
FEATURE [App::DocumentObjectGroupPython] FPSimButton025  label="BtnQuantize"  # scripted group (container) (typed FeaturePython)
  Group = -> [FPSimLED120,Cut044]
  PressureResolutionAng = (0,0,0)
  PressureResolutionLin = (0,0,0)
  RotationAngle = 0
  RotationAxis = (0,0,0)
  RotationCenter = (0,0,0)
  SwitchMode = false
  Translation = (0,0,-1)
FEATURE [App::Part] Part038  label="FrBtnQuantize"
  Group = -> [FPSimButton025,ShapeString022,Extrude030,FPSimLED120,Extrude031,Box247,ShapeString023,Cut044]
  License = CC BY 3.0
  LicenseURL = http://creativecommons.org/licenses/by/3.0/
  Origin = -> Origin038
  Placement = pos=(-182,-24,0) rot=(0,0,1;0rad)
FEATURE [Part::Part2DObjectPython] ShapeString024  # Draft 2D object (typed FeaturePython)
  FontFile = <path>
  Placement = pos=(1,13,0) rot=(0,0,1;0rad)
  Size = 3
  String = Duplicate
  Tracking = 0
FEATURE [Part::Extrusion] Extrude032  label="Txt022"
  Base = -> ShapeString024
  Dir = (0,0,1)
  DirMode = 2
  FaceMakerClass = Part::FaceMakerBullseye
  LengthFwd = 1
  LengthRev = 0
  Solid = true
  Symmetric = false
FEATURE [App::DocumentObjectGroupPython] FPSimLED121  label="LedDuplicate"  # scripted group (container) (typed FeaturePython)
  Group = -> [Extrude032]
FEATURE [Part::Part2DObjectPython] ShapeString025  # Draft 2D object (typed FeaturePython)
  FontFile = <path>
  Placement = pos=(1,13,0) rot=(0,0,1;0rad)
  Size = 3
  String = Duplicate
  Tracking = 0
FEATURE [Part::Extrusion] Extrude033  label="Txt023"
  Base = -> ShapeString025
  Dir = (0,0,1)
  DirMode = 2
  FaceMakerClass = Part::FaceMakerBullseye
  LengthFwd = 2
  LengthRev = 1
  Solid = true
  Symmetric = false
FEATURE [Part::Cut] Cut045
  Base = -> Box028
  Tool = -> Extrude033
FEATURE [App::DocumentObjectGroupPython] FPSimButton026  label="BtnDuplicate"  # scripted group (container) (typed FeaturePython)
  Group = -> [FPSimLED121,Cut045]
  PressureResolutionAng = (0,0,0)
  PressureResolutionLin = (0,0,0)
  RotationAngle = 0
  RotationAxis = (0,0,0)
  RotationCenter = (0,0,0)
  SwitchMode = false
  Translation = (0,0,-1)
FEATURE [App::Part] Part039  label="FrBtnDuplicate"
  Group = -> [Box028,FPSimButton026,ShapeString024,Extrude032,FPSimLED121,ShapeString025,Extrude033,Cut045]
  License = CC BY 3.0
  LicenseURL = http://creativecommons.org/licenses/by/3.0/
  Origin = -> Origin039
  Placement = pos=(-182,-45,0) rot=(0,0,1;0rad)
FEATURE [Part::Box] Box248  label="Cube216"
  AttacherType = Attacher::AttachEngine3D
  Height = 1
  Length = 18.5
  Width = 18.5
FEATURE [Part::Part2DObjectPython] ShapeString026  # Draft 2D object (typed FeaturePython)
  FontFile = <path>
  Placement = pos=(1,13,0) rot=(0,0,1;0rad)
  Size = 3
  String = New
  Tracking = 0
FEATURE [Part::Extrusion] Extrude035  label="Txt025"
  Base = -> ShapeString026
  Dir = (0,0,1)
  DirMode = 2
  FaceMakerClass = Part::FaceMakerBullseye
  LengthFwd = 1
  LengthRev = 0
  Solid = true
  Symmetric = false
FEATURE [App::DocumentObjectGroupPython] FPSimLED122  label="LedNew"  # scripted group (container) (typed FeaturePython)
  Group = -> [Extrude035]
FEATURE [Part::Part2DObjectPython] ShapeString027  # Draft 2D object (typed FeaturePython)
  FontFile = <path>
  Placement = pos=(1,13,0) rot=(0,0,1;0rad)
  Size = 3
  String = New
  Tracking = 0
FEATURE [Part::Extrusion] Extrude034  label="Txt024"
  Base = -> ShapeString027
  Dir = (0,0,1)
  DirMode = 2
  FaceMakerClass = Part::FaceMakerBullseye
  LengthFwd = 2
  LengthRev = 1
  Solid = true
  Symmetric = false
FEATURE [Part::Cut] Cut046
  Base = -> Box248
  Tool = -> Extrude034
FEATURE [App::DocumentObjectGroupPython] FPSimButton027  label="BtnNew"  # scripted group (container) (typed FeaturePython)
  Group = -> [Cut046,FPSimLED122]
  PressureResolutionAng = (0,0,0)
  PressureResolutionLin = (0,0,0)
  RotationAngle = 0
  RotationAxis = (0,0,0)
  RotationCenter = (0,0,0)
  SwitchMode = false
  Translation = (0,0,-1)
FEATURE [App::Part] Part040  label="FrBtnNew"
  Group = -> [FPSimButton027,ShapeString027,Extrude034,Box248,Cut046,ShapeString026,Extrude035,FPSimLED122]
  License = CC BY 3.0
  LicenseURL = http://creativecommons.org/licenses/by/3.0/
  Origin = -> Origin040
  Placement = pos=(-182,-63.5,0) rot=(0,0,1;0rad)
FEATURE [Part::Part2DObjectPython] ShapeString028  # Draft 2D object (typed FeaturePython)
  FontFile = <path>
  Placement = pos=(1,13,0) rot=(0,0,1;0rad)
  Size = 3
  String = Fixed
  Tracking = 0
FEATURE [Part::Extrusion] Extrude036  label="Txt026"
  Base = -> ShapeString028
  Dir = (0,0,1)
  DirMode = 2
  FaceMakerClass = Part::FaceMakerBullseye
  LengthFwd = 2
  LengthRev = 1
  Solid = true
  Symmetric = false
FEATURE [Part::Part2DObjectPython] ShapeString029  # Draft 2D object (typed FeaturePython)
  FontFile = <path>
  Placement = pos=(1,10,0) rot=(0,0,1;0rad)
  Size = 3
  String = Length
  Tracking = 0
FEATURE [Part::Extrusion] Extrude037  label="Txt027"
  Base = -> ShapeString029
  Dir = (0,0,1)
  DirMode = 2
  FaceMakerClass = Part::FaceMakerBullseye
  LengthFwd = 2
  LengthRev = 1
  Solid = true
  Symmetric = false
FEATURE [Part::Part2DObjectPython] ShapeString030  # Draft 2D object (typed FeaturePython)
  FontFile = <path>
  Placement = pos=(1,10,0) rot=(0,0,1;0rad)
  Size = 3
  String = Length
  Tracking = 0
FEATURE [Part::Extrusion] Extrude038  label="Txt028"
  Base = -> ShapeString030
  Dir = (0,0,1)
  DirMode = 2
  FaceMakerClass = Part::FaceMakerBullseye
  LengthFwd = 1
  LengthRev = 0
  Solid = true
  Symmetric = false
FEATURE [Part::Part2DObjectPython] ShapeString031  # Draft 2D object (typed FeaturePython)
  FontFile = <path>
  Placement = pos=(1,13,0) rot=(0,0,1;0rad)
  Size = 3
  String = Fixed
  Tracking = 0
FEATURE [Part::Extrusion] Extrude039  label="Txt029"
  Base = -> ShapeString031
  Dir = (0,0,1)
  DirMode = 2
  FaceMakerClass = Part::FaceMakerBullseye
  LengthFwd = 1
  LengthRev = 0
  Solid = true
  Symmetric = false
FEATURE [App::DocumentObjectGroupPython] FPSimLED123  label="LedFixedLength"  # scripted group (container) (typed FeaturePython)
  Group = -> [Extrude038,Extrude039]
FEATURE [Part::Cut] Cut047
  Base = -> Box030
  Tool = -> Extrude036
FEATURE [Part::Cut] Cut048
  Base = -> Cut047
  Tool = -> Extrude037
FEATURE [App::DocumentObjectGroupPython] FPSimButton028  label="BtnFixedLength"  # scripted group (container) (typed FeaturePython)
  Group = -> [FPSimLED123,Cut048]
  PressureResolutionAng = (0,0,0)
  PressureResolutionLin = (0,0,0)
  RotationAngle = 0
  RotationAxis = (0,0,0)
  RotationCenter = (0,0,0)
  SwitchMode = false
  Translation = (0,0,-1)
FEATURE [App::Part] Part041  label="FrBtnFixedLength"
  Group = -> [Box030,FPSimButton028,Extrude036,ShapeString028,FPSimLED123,ShapeString029,Extrude037,ShapeString030,Extrude038,ShapeString031,Extrude039,Cut047,Cut048]
  License = CC BY 3.0
  LicenseURL = http://creativecommons.org/licenses/by/3.0/
  Origin = -> Origin041
  Placement = pos=(-182,-84.5,0) rot=(0,0,1;0rad)
FEATURE [Part::Part2DObjectPython] ShapeString032  # Draft 2D object (typed FeaturePython)
  FontFile = <path>
  Placement = pos=(1,13,0) rot=(0,0,1;0rad)
  Size = 3
  String = Automate
  Tracking = 0
FEATURE [Part::Extrusion] Extrude040  label="Txt030"
  Base = -> ShapeString032
  Dir = (0,0,1)
  DirMode = 2
  FaceMakerClass = Part::FaceMakerBullseye
  LengthFwd = 1
  LengthRev = 0
  Solid = true
  Symmetric = false
FEATURE [App::DocumentObjectGroupPython] FPSimLED124  label="LedAutomate"  # scripted group (container) (typed FeaturePython)
  Group = -> [Extrude040]
FEATURE [Part::Part2DObjectPython] ShapeString033  # Draft 2D object (typed FeaturePython)
  FontFile = <path>
  Placement = pos=(1,13,0) rot=(0,0,1;0rad)
  Size = 3
  String = Automate
  Tracking = 0
FEATURE [Part::Extrusion] Extrude041  label="Txt031"
  Base = -> ShapeString033
  Dir = (0,0,1)
  DirMode = 2
  FaceMakerClass = Part::FaceMakerBullseye
  LengthFwd = 1
  LengthRev = 0
  Solid = true
  Symmetric = false
FEATURE [Part::Cut] Cut049
  Base = -> Box031
  Tool = -> Extrude041
FEATURE [App::DocumentObjectGroupPython] FPSimButton029  label="BtnAutomate"  # scripted group (container) (typed FeaturePython)
  Group = -> [FPSimLED124,Cut049]
  PressureResolutionAng = (0,0,0)
  PressureResolutionLin = (0,0,0)
  RotationAngle = 0
  RotationAxis = (0,0,0)
  RotationCenter = (0,0,0)
  SwitchMode = false
  Translation = (0,0,-1)
FEATURE [App::Part] Part042  label="FrBtnAutomate"
  Group = -> [Box031,FPSimButton029,Extrude040,ShapeString032,FPSimLED124,ShapeString033,Extrude041,Cut049]
  License = CC BY 3.0
  LicenseURL = http://creativecommons.org/licenses/by/3.0/
  Origin = -> Origin042
  Placement = pos=(-182,-102,0) rot=(0,0,1;0rad)
FEATURE [Part::Box] Box249  label="Cube217"
  AttacherType = Attacher::AttachEngine3D
  Height = 1
  Length = 18.5
  Width = 17.5
FEATURE [Part::Cylinder] Cylinder031
  Angle = 360
  AttacherType = Attacher::AttachEngine3D
  Height = 10
  Placement = pos=(9.25,8.75,-1) rot=(0,0,1;0rad)
  Radius = 6
FEATURE [Part::Cylinder] Cylinder032
  Angle = 360
  AttacherType = Attacher::AttachEngine3D
  Height = 10
  Placement = pos=(9.25,8.75,-1) rot=(0,0,1;0rad)
  Radius = 5
FEATURE [Part::Cut] Cut050  label="CylHole"
  Base = -> Cylinder031
  Tool = -> Cylinder032
FEATURE [Part::Cylinder] Cylinder033
  Angle = 360
  AttacherType = Attacher::AttachEngine3D
  Height = 1
  Placement = pos=(9.25,8.75,0) rot=(0,0,1;0rad)
  Radius = 6
FEATURE [Part::Cylinder] Cylinder034
  Angle = 360
  AttacherType = Attacher::AttachEngine3D
  Height = 1
  Placement = pos=(9.25,8.75,0) rot=(0,0,1;0rad)
  Radius = 5
FEATURE [Part::Cut] Cut051  label="CylHole001"
  Base = -> Cylinder033
  Tool = -> Cylinder034
FEATURE [App::DocumentObjectGroupPython] FPSimLED125  label="LedRecord"  # scripted group (container) (typed FeaturePython)
  Group = -> [Cut051]
FEATURE [Part::Cut] Cut052
  Base = -> Box249
  Tool = -> Cut050
FEATURE [App::DocumentObjectGroupPython] FPSimButton030  label="BtnRecord"  # scripted group (container) (typed FeaturePython)
  Group = -> [FPSimLED125,Cut052]
  PressureResolutionAng = (0,0,0)
  PressureResolutionLin = (0,0,0)
  RotationAngle = 0
  RotationAxis = (0,0,0)
  RotationCenter = (0,0,0)
  SwitchMode = false
  Translation = (0,0,-1)
FEATURE [App::Part] Part043  label="FrBtnRecord"
  Group = -> [FPSimButton030,Box249,FPSimLED125,Cylinder031,Cylinder032,Cut050,Cylinder033,Cylinder034,Cut051,Cut052]
  License = CC BY 3.0
  LicenseURL = http://creativecommons.org/licenses/by/3.0/
  Origin = -> Origin043
  Placement = pos=(-182,-119.5,0) rot=(0,0,1;0rad)
FEATURE [Sketcher::SketchObject] Sketch020
  MapMode = 5
  Placement = pos=(0,0,1) rot=(0,0,1;0rad)
  sketch-geometry (6):
    g0: LineSegment StartX=0 StartY=0 StartZ=0 EndX=-10.3923 EndY=6 EndZ=0
    g1: LineSegment StartX=-10.3923 StartY=6 StartZ=0 EndX=-10.3923 EndY=-6 EndZ=0
    g2: LineSegment StartX=-10.3923 StartY=-6 StartZ=0 EndX=0 EndY=0 EndZ=0
    g3: LineSegment StartX=-9.3923 StartY=4.34249 StartZ=0 EndX=-9.3923 EndY=-4.34249 EndZ=0
    g4: LineSegment StartX=-9.3923 StartY=-4.34249 StartZ=0 EndX=-1.87089 EndY=0 EndZ=0
    g5: LineSegment StartX=-1.87089 StartY=0 StartZ=0 EndX=-9.3923 EndY=4.34249 EndZ=0
  constraints (14):
    c: Coincident(g0,g-1)
    c: Coincident(g1,g0)
    c: Coincident(g2,g1)
    c: Coincident(g2,g0)
    c: Symmetric(g1,g0,g-1)
    c: Coincident(g4,g3)
    c: PointOnObject(g4,g-1)
    c: Coincident(g5,g4)
    c: Coincident(g5,g3)
    c: Symmetric(g3,g3,g-1)
    c: DistanceX(g1,g3) = 1
    c: DistanceY(g1,g0) = 12
    c: Equal(g0,g1)
    c: Parallel(g5,g0)
FEATURE [Part::Extrusion] Extrude042  label="TriangleHole"
  Base = -> Sketch020
  Dir = (0,0,1)
  DirMode = 2
  FaceMakerClass = Part::FaceMakerBullseye
  LengthFwd = 2
  LengthRev = 1
  Placement = pos=(15,9,0) rot=(0,0,1;0rad)
  Solid = true
  Symmetric = false
FEATURE [Sketcher::SketchObject] Sketch021
  MapMode = 5
  sketch-geometry (6):
    g0: LineSegment StartX=0 StartY=0 StartZ=0 EndX=-10.3923 EndY=6 EndZ=0
    g1: LineSegment StartX=-10.3923 StartY=6 StartZ=0 EndX=-10.3923 EndY=-6 EndZ=0
    g2: LineSegment StartX=-10.3923 StartY=-6 StartZ=0 EndX=0 EndY=0 EndZ=0
    g3: LineSegment StartX=-9.3923 StartY=4.34249 StartZ=0 EndX=-9.3923 EndY=-4.34249 EndZ=0
    g4: LineSegment StartX=-9.3923 StartY=-4.34249 StartZ=0 EndX=-1.87089 EndY=0 EndZ=0
    g5: LineSegment StartX=-1.87089 StartY=0 StartZ=0 EndX=-9.3923 EndY=4.34249 EndZ=0
  constraints (14):
    c: Coincident(g0,g-1)
    c: Coincident(g1,g0)
    c: Coincident(g2,g1)
    c: Coincident(g2,g0)
    c: Symmetric(g1,g0,g-1)
    c: Coincident(g4,g3)
    c: PointOnObject(g4,g-1)
    c: Coincident(g5,g4)
    c: Coincident(g5,g3)
    c: Symmetric(g3,g3,g-1)
    c: DistanceX(g1,g3) = 1
    c: DistanceY(g1,g0) = 12
    c: Equal(g0,g1)
    c: Parallel(g5,g0)
FEATURE [Part::Extrusion] Extrude043  label="Triangle"
  Base = -> Sketch021
  Dir = (0,0,1)
  DirMode = 2
  FaceMakerClass = Part::FaceMakerBullseye
  LengthFwd = 1
  LengthRev = 0
  Placement = pos=(15,9,0) rot=(0,0,1;0rad)
  Solid = true
  Symmetric = false
FEATURE [Part::Cut] Cut053
  Base = -> Box033
  Tool = -> Extrude042
FEATURE [App::DocumentObjectGroupPython] FPSimLED126  label="LedPlay"  # scripted group (container) (typed FeaturePython)
  Group = -> [Extrude043]
FEATURE [App::DocumentObjectGroupPython] FPSimButton031  label="BtnPlay"  # scripted group (container) (typed FeaturePython)
  Group = -> [Sketch020,Cut053,FPSimLED126]
  PressureResolutionAng = (0,0,0)
  PressureResolutionLin = (0,0,0)
  RotationAngle = 0
  RotationAxis = (0,0,0)
  RotationCenter = (0,0,0)
  SwitchMode = false
  Translation = (0,0,-1)
FEATURE [App::Part] Part044  label="FrBtnPlay"
  Group = -> [Box033,FPSimButton031,Sketch020,Extrude042,Cut053,Sketch021,Extrude043,FPSimLED126]
  License = CC BY 3.0
  LicenseURL = http://creativecommons.org/licenses/by/3.0/
  Origin = -> Origin044
  Placement = pos=(-182,-140.5,0) rot=(0,0,1;0rad)
FEATURE [App::DocumentObjectGroup] Group005  label="Left"
  Group = -> [Part033,Part034,Part035,Part036,Part037,Part038,Part039,Part040,Part041,Part042,Part043,Part044,Part045]
FEATURE [App::DocumentObjectGroupPython] FPSimLED127  label="LedT[0]"  # scripted group (container) (typed FeaturePython)
  Group = -> [Box118]
FEATURE [App::DocumentObjectGroupPython] FPSimButton002  label="BtnT[0]"  # scripted group (container) (typed FeaturePython)
  Group = -> [Cut017,FPSimLED127]
  RotationAngle = 0
  RotationAxis = (0,0,0)
  RotationCenter = (0,0,0)
  SwitchMode = false
  Translation = (0,0,-0.8)
FEATURE [App::Part] Part014  label="FrBtnT[0]"
  Group = -> [Box003,FPSimButton002,Box117,Cut017,Box118,FPSimLED127]
  License = CC BY 3.0
  LicenseURL = http://creativecommons.org/licenses/by/3.0/
  Origin = -> Origin014
  Placement = pos=(-119.1,112.2,0) rot=(0,0,1;0rad)
FEATURE [App::DocumentObjectGroupPython] FPSimLED128  label="LedT[1]"  # scripted group (container) (typed FeaturePython)
  Group = -> [Box121]
FEATURE [App::DocumentObjectGroupPython] FPSimButton003  label="BtnT[1]"  # scripted group (container) (typed FeaturePython)
  Group = -> [Cut018,FPSimLED128]
  RotationAngle = 0
  RotationAxis = (0,0,0)
  RotationCenter = (0,0,0)
  SwitchMode = false
  Translation = (0,0,-0.8)
FEATURE [App::Part] Part015  label="FrBtnT[1]"
  Group = -> [FPSimButton003,Box120,Box119,Cut018,Box121,FPSimLED128]
  License = CC BY 3.0
  LicenseURL = http://creativecommons.org/licenses/by/3.0/
  Origin = -> Origin015
  Placement = pos=(-90.1,112.2,0) rot=(0,0,1;0rad)
FEATURE [App::DocumentObjectGroupPython] FPSimLED129  label="LedT[2]"  # scripted group (container) (typed FeaturePython)
  Group = -> [Box124]
FEATURE [App::DocumentObjectGroupPython] FPSimButton004  label="BtnT[2]"  # scripted group (container) (typed FeaturePython)
  Group = -> [Cut019,FPSimLED129]
  RotationAngle = 0
  RotationAxis = (0,0,0)
  RotationCenter = (0,0,0)
  SwitchMode = false
  Translation = (0,0,-0.8)
FEATURE [App::Part] Part016  label="FrBtnT[2]"
  Group = -> [FPSimButton004,Box123,Box122,Cut019,Box124,FPSimLED129]
  License = CC BY 3.0
  LicenseURL = http://creativecommons.org/licenses/by/3.0/
  Origin = -> Origin016
  Placement = pos=(-61.1,112.2,0) rot=(0,0,1;0rad)
FEATURE [App::DocumentObjectGroupPython] FPSimLED130  label="LedT[3]"  # scripted group (container) (typed FeaturePython)
  Group = -> [Box127]
FEATURE [App::DocumentObjectGroupPython] FPSimButton005  label="BtnT[3]"  # scripted group (container) (typed FeaturePython)
  Group = -> [Cut020,FPSimLED130]
  RotationAngle = 0
  RotationAxis = (0,0,0)
  RotationCenter = (0,0,0)
  SwitchMode = false
  Translation = (0,0,-0.8)
FEATURE [App::Part] Part017  label="FrBtnT[3]"
  Group = -> [FPSimButton005,Box125,Box126,Cut020,Box127,FPSimLED130]
  License = CC BY 3.0
  LicenseURL = http://creativecommons.org/licenses/by/3.0/
  Origin = -> Origin017
  Placement = pos=(-32.1,112.2,0) rot=(0,0,1;0rad)
FEATURE [App::DocumentObjectGroupPython] FPSimLED131  label="LedT[4]"  # scripted group (container) (typed FeaturePython)
  Group = -> [Box130]
FEATURE [App::DocumentObjectGroupPython] FPSimButton006  label="BtnT[4]"  # scripted group (container) (typed FeaturePython)
  Group = -> [Cut021,FPSimLED131]
  RotationAngle = 0
  RotationAxis = (0,0,0)
  RotationCenter = (0,0,0)
  SwitchMode = false
  Translation = (0,0,-0.8)
FEATURE [App::Part] Part018  label="FrBtnT[4]"
  Group = -> [FPSimButton006,Box128,Box129,Cut021,Box130,FPSimLED131]
  License = CC BY 3.0
  LicenseURL = http://creativecommons.org/licenses/by/3.0/
  Origin = -> Origin018
  Placement = pos=(-3.1,112.2,0) rot=(0,0,1;0rad)
FEATURE [App::DocumentObjectGroupPython] FPSimLED132  label="LedT[5]"  # scripted group (container) (typed FeaturePython)
  Group = -> [Box133]
FEATURE [App::DocumentObjectGroupPython] FPSimButton007  label="BtnT[5]"  # scripted group (container) (typed FeaturePython)
  Group = -> [Cut022,FPSimLED132]
  RotationAngle = 0
  RotationAxis = (0,0,0)
  RotationCenter = (0,0,0)
  SwitchMode = false
  Translation = (0,0,-0.8)
FEATURE [App::Part] Part019  label="FrBtnT[5]"
  Group = -> [FPSimButton007,Box131,Box132,Cut022,Box133,FPSimLED132]
  License = CC BY 3.0
  LicenseURL = http://creativecommons.org/licenses/by/3.0/
  Origin = -> Origin019
  Placement = pos=(25.9,112.2,0) rot=(0,0,1;0rad)
FEATURE [App::DocumentObjectGroupPython] FPSimLED133  label="LedT[6]"  # scripted group (container) (typed FeaturePython)
  Group = -> [Box136]
FEATURE [App::DocumentObjectGroupPython] FPSimButton008  label="BtnT[6]"  # scripted group (container) (typed FeaturePython)
  Group = -> [Cut023,FPSimLED133]
  RotationAngle = 0
  RotationAxis = (0,0,0)
  RotationCenter = (0,0,0)
  SwitchMode = false
  Translation = (0,0,-0.8)
FEATURE [App::Part] Part020  label="FrBtnT[6]"
  Group = -> [FPSimButton008,Box134,Box135,Cut023,Box136,FPSimLED133]
  License = CC BY 3.0
  LicenseURL = http://creativecommons.org/licenses/by/3.0/
  Origin = -> Origin020
  Placement = pos=(54.9,112.2,0) rot=(0,0,1;0rad)
FEATURE [App::DocumentObjectGroupPython] FPSimLED134  label="LedT[7]"  # scripted group (container) (typed FeaturePython)
  Group = -> [Box139]
FEATURE [App::DocumentObjectGroupPython] FPSimButton009  label="BtnT[7]"  # scripted group (container) (typed FeaturePython)
  Group = -> [Cut024,FPSimLED134]
  RotationAngle = 0
  RotationAxis = (0,0,0)
  RotationCenter = (0,0,0)
  SwitchMode = false
  Translation = (0,0,-0.8)
FEATURE [App::Part] Part021  label="FrBtnT[7]"
  Group = -> [FPSimButton009,Box137,Box138,Cut024,Box139,FPSimLED134]
  License = CC BY 3.0
  LicenseURL = http://creativecommons.org/licenses/by/3.0/
  Origin = -> Origin021
  Placement = pos=(83.9,112.2,0) rot=(0,0,1;0rad)
FEATURE [App::DocumentObjectGroupPython] FPSimLED135  label="LedB[0]"  # scripted group (container) (typed FeaturePython)
  Group = -> [Box142]
FEATURE [App::DocumentObjectGroupPython] FPSimButton033  label="BtnB[0]"  # scripted group (container) (typed FeaturePython)
  Group = -> [Cut025,FPSimLED135]
  RotationAngle = 0
  RotationAxis = (0,0,0)
  RotationCenter = (0,0,0)
  SwitchMode = false
  Translation = (0,0,-0.8)
FEATURE [App::Part] Part046  label="FrBtnB[0]"
  Group = -> [FPSimButton033,Box140,Box141,Cut025,Box142,FPSimLED135]
  License = CC BY 3.0
  LicenseURL = http://creativecommons.org/licenses/by/3.0/
  Origin = -> Origin046
  Placement = pos=(-119.1,39.2,0) rot=(0,0,1;0rad)
FEATURE [App::DocumentObjectGroupPython] FPSimLED136  label="LedB[1]"  # scripted group (container) (typed FeaturePython)
  Group = -> [Box144]
FEATURE [App::DocumentObjectGroupPython] FPSimButton034  label="BtnB[1]"  # scripted group (container) (typed FeaturePython)
  Group = -> [Cut026,FPSimLED136]
  RotationAngle = 0
  RotationAxis = (0,0,0)
  RotationCenter = (0,0,0)
  SwitchMode = false
  Translation = (0,0,-0.8)
FEATURE [App::Part] Part047  label="FrBtnB[1]"
  Group = -> [FPSimButton034,Box143,Box145,Cut026,Box144,FPSimLED136]
  License = CC BY 3.0
  LicenseURL = http://creativecommons.org/licenses/by/3.0/
  Origin = -> Origin047
  Placement = pos=(-90.1,39.2,0) rot=(0,0,1;0rad)
FEATURE [App::DocumentObjectGroupPython] FPSimLED137  label="LedB[2]"  # scripted group (container) (typed FeaturePython)
  Group = -> [Box147]
FEATURE [App::DocumentObjectGroupPython] FPSimButton032  label="BtnB[2]"  # scripted group (container) (typed FeaturePython)
  Group = -> [Cut027,FPSimLED137]
  RotationAngle = 0
  RotationAxis = (0,0,0)
  RotationCenter = (0,0,0)
  SwitchMode = false
  Translation = (0,0,-0.8)
FEATURE [App::Part] Part048  label="FrBtnB[2]"
  Group = -> [FPSimButton032,Box146,Box148,Cut027,Box147,FPSimLED137]
  License = CC BY 3.0
  LicenseURL = http://creativecommons.org/licenses/by/3.0/
  Origin = -> Origin048
  Placement = pos=(-61.1,39.2,0) rot=(0,0,1;0rad)
FEATURE [App::DocumentObjectGroupPython] FPSimLED138  label="LedB[3]"  # scripted group (container) (typed FeaturePython)
  Group = -> [Box150]
FEATURE [App::DocumentObjectGroupPython] FPSimButton035  label="BtnB[3]"  # scripted group (container) (typed FeaturePython)
  Group = -> [Cut028,FPSimLED138]
  RotationAngle = 0
  RotationAxis = (0,0,0)
  RotationCenter = (0,0,0)
  SwitchMode = false
  Translation = (0,0,-0.8)
FEATURE [App::Part] Part049  label="FrBtnB[3]"
  Group = -> [FPSimButton035,Box151,Box149,Cut028,Box150,FPSimLED138]
  License = CC BY 3.0
  LicenseURL = http://creativecommons.org/licenses/by/3.0/
  Origin = -> Origin049
  Placement = pos=(-32.1,39.2,0) rot=(0,0,1;0rad)
FEATURE [App::DocumentObjectGroupPython] FPSimLED139  label="LedB[4]"  # scripted group (container) (typed FeaturePython)
  Group = -> [Box153]
FEATURE [App::DocumentObjectGroupPython] FPSimButton036  label="BtnB[4]"  # scripted group (container) (typed FeaturePython)
  Group = -> [Cut029,FPSimLED139]
  RotationAngle = 0
  RotationAxis = (0,0,0)
  RotationCenter = (0,0,0)
  SwitchMode = false
  Translation = (0,0,-0.8)
FEATURE [App::Part] Part050  label="FrBtnB[4]"
  Group = -> [FPSimButton036,Box152,Box154,Cut029,Box153,FPSimLED139]
  License = CC BY 3.0
  LicenseURL = http://creativecommons.org/licenses/by/3.0/
  Origin = -> Origin050
  Placement = pos=(-3.1,39.2,0) rot=(0,0,1;0rad)
FEATURE [App::DocumentObjectGroupPython] FPSimLED140  label="LedB[5]"  # scripted group (container) (typed FeaturePython)
  Group = -> [Box156]
FEATURE [App::DocumentObjectGroupPython] FPSimButton037  label="BtnB[5]"  # scripted group (container) (typed FeaturePython)
  Group = -> [Cut030,FPSimLED140]
  RotationAngle = 0
  RotationAxis = (0,0,0)
  RotationCenter = (0,0,0)
  SwitchMode = false
  Translation = (0,0,-0.8)
FEATURE [App::Part] Part051  label="FrBtnB[5]"
  Group = -> [FPSimButton037,Box155,Box157,Cut030,Box156,FPSimLED140]
  License = CC BY 3.0
  LicenseURL = http://creativecommons.org/licenses/by/3.0/
  Origin = -> Origin051
  Placement = pos=(25.9,39.2,0) rot=(0,0,1;0rad)
FEATURE [App::DocumentObjectGroupPython] FPSimLED141  label="LedB[6]"  # scripted group (container) (typed FeaturePython)
  Group = -> [Box159]
FEATURE [App::DocumentObjectGroupPython] FPSimButton038  label="BtnB[6]"  # scripted group (container) (typed FeaturePython)
  Group = -> [Cut031,FPSimLED141]
  RotationAngle = 0
  RotationAxis = (0,0,0)
  RotationCenter = (0,0,0)
  SwitchMode = false
  Translation = (0,0,-0.8)
FEATURE [App::Part] Part052  label="FrBtnB[6]"
  Group = -> [FPSimButton038,Box160,Box158,Cut031,Box159,FPSimLED141]
  License = CC BY 3.0
  LicenseURL = http://creativecommons.org/licenses/by/3.0/
  Origin = -> Origin052
  Placement = pos=(54.9,39.2,0) rot=(0,0,1;0rad)
FEATURE [App::DocumentObjectGroupPython] FPSimLED142  label="LedB[7]"  # scripted group (container) (typed FeaturePython)
  Group = -> [Box162]
FEATURE [App::DocumentObjectGroupPython] FPSimButton039  label="BtnB[7]"  # scripted group (container) (typed FeaturePython)
  Group = -> [Cut032,FPSimLED142]
  RotationAngle = 0
  RotationAxis = (0,0,0)
  RotationCenter = (0,0,0)
  SwitchMode = false
  Translation = (0,0,-0.8)
FEATURE [App::Part] Part053  label="FrBtnB[7]"
  Group = -> [FPSimButton039,Box161,Box163,Cut032,Box162,FPSimLED142]
  License = CC BY 3.0
  LicenseURL = http://creativecommons.org/licenses/by/3.0/
  Origin = -> Origin053
  Placement = pos=(83.9,39.2,0) rot=(0,0,1;0rad)
FEATURE [Part::Part2DObjectPython] ShapeString034  # Draft 2D object (typed FeaturePython)
  FontFile = <path>
  Placement = pos=(1,6,0) rot=(0,0,1;0rad)
  Size = 3
  String = Setup
  Tracking = 0
FEATURE [Part::Extrusion] Extrude044  label="Txt032"
  Base = -> ShapeString034
  Dir = (0,0,1)
  DirMode = 2
  FaceMakerClass = Part::FaceMakerBullseye
  LengthFwd = 1
  LengthRev = 0
  Solid = true
  Symmetric = false
FEATURE [App::DocumentObjectGroupPython] FPSimLED143  label="LedSetup"  # scripted group (container) (typed FeaturePython)
  Group = -> [Extrude044]
FEATURE [Part::Part2DObjectPython] ShapeString035  # Draft 2D object (typed FeaturePython)
  FontFile = <path>
  Placement = pos=(1,6,0) rot=(0,0,1;0rad)
  Size = 3
  String = User
  Tracking = 0
FEATURE [Part::Extrusion] Extrude045  label="Txt033"
  Base = -> ShapeString035
  Dir = (0,0,1)
  DirMode = 2
  FaceMakerClass = Part::FaceMakerBullseye
  LengthFwd = 1
  LengthRev = 0
  Solid = true
  Symmetric = false
FEATURE [App::DocumentObjectGroupPython] FPSimLED144  label="LedUser"  # scripted group (container) (typed FeaturePython)
  Group = -> [Extrude045]
FEATURE [Part::Part2DObjectPython] ShapeString036  # Draft 2D object (typed FeaturePython)
  FontFile = <path>
  Placement = pos=(1,6,0) rot=(0,0,1;0rad)
  Size = 3
  String = Setup
  Tracking = 0
FEATURE [Part::Extrusion] Extrude046  label="Txt034"
  Base = -> ShapeString036
  Dir = (0,0,1)
  DirMode = 2
  FaceMakerClass = Part::FaceMakerBullseye
  LengthFwd = 2
  LengthRev = 1
  Solid = true
  Symmetric = false
FEATURE [Part::Part2DObjectPython] ShapeString037  # Draft 2D object (typed FeaturePython)
  FontFile = <path>
  Placement = pos=(1,6,0) rot=(0,0,1;0rad)
  Size = 3
  String = User
  Tracking = 0
FEATURE [Part::Extrusion] Extrude047  label="Txt035"
  Base = -> ShapeString037
  Dir = (0,0,1)
  DirMode = 2
  FaceMakerClass = Part::FaceMakerBullseye
  LengthFwd = 2
  LengthRev = 1
  Solid = true
  Symmetric = false
FEATURE [Part::Cut] Cut054
  Base = -> Box011
  Tool = -> Extrude046
FEATURE [App::DocumentObjectGroupPython] FPSimButton010  label="BtnSetup"  # scripted group (container) (typed FeaturePython)
  Group = -> [FPSimLED143,Cut054]
  RotationAngle = 0
  RotationAxis = (0,0,0)
  RotationCenter = (0,0,0)
  SwitchMode = false
  Translation = (0,0,-0.8)
FEATURE [App::Part] Part022  label="FrBtnSetup"
  Group = -> [Box011,FPSimButton010,Extrude044,ShapeString034,FPSimLED143,ShapeString036,Extrude046,Cut054]
  License = CC BY 3.0
  LicenseURL = http://creativecommons.org/licenses/by/3.0/
  Origin = -> Origin022
  Placement = pos=(144.9,112.2,0) rot=(0,0,1;0rad)
FEATURE [Part::Cut] Cut055
  Base = -> Box012
  Tool = -> Extrude047
FEATURE [App::DocumentObjectGroupPython] FPSimButton011  label="BtnUser"  # scripted group (container) (typed FeaturePython)
  Group = -> [FPSimLED144,Cut055]
  RotationAngle = 0
  RotationAxis = (0,0,0)
  RotationCenter = (0,0,0)
  SwitchMode = false
  Translation = (0,0,-0.8)
FEATURE [App::Part] Part023  label="FrBtnUser"
  Group = -> [Box012,FPSimButton011,Extrude045,ShapeString035,FPSimLED144,ShapeString037,Extrude047,Cut055]
  License = CC BY 3.0
  LicenseURL = http://creativecommons.org/licenses/by/3.0/
  Origin = -> Origin023
  Placement = pos=(163.9,112.2,0) rot=(0,0,1;0rad)
FEATURE [App::DocumentObjectGroup] Group001  label="Top"
  Group = -> [Group,Part012,Part013,Part014,Part015,Part016,Part017,Part018,Part019,Part020,Part021,Part022,Part023]
FEATURE [Part::Part2DObjectPython] ShapeString038  # Draft 2D object (typed FeaturePython)
  FontFile = <path>
  Placement = pos=(1,13,0) rot=(0,0,1;0rad)
  Size = 3
  String = Add
  Tracking = 0
FEATURE [Part::Extrusion] Extrude048  label="TxtAdd"
  Base = -> ShapeString038
  Dir = (0,0,1)
  DirMode = 2
  FaceMakerClass = Part::FaceMakerBullseye
  LengthFwd = 1
  LengthRev = 0
  Solid = true
  Symmetric = false
FEATURE [Part::Part2DObjectPython] ShapeString039  # Draft 2D object (typed FeaturePython)
  FontFile = <path>
  Placement = pos=(1,13,0) rot=(0,0,1;0rad)
  Size = 3
  String = Add
  Tracking = 0
FEATURE [Part::Extrusion] Extrude049  label="TxtAdd001"
  Base = -> ShapeString039
  Dir = (0,0,1)
  DirMode = 2
  FaceMakerClass = Part::FaceMakerBullseye
  LengthFwd = 1
  LengthRev = 0
  Solid = true
  Symmetric = false
FEATURE [Part::Part2DObjectPython] ShapeString040  # Draft 2D object (typed FeaturePython)
  FontFile = <path>
  Placement = pos=(1,10,0) rot=(0,0,1;0rad)
  Size = 3
  String = Device
  Tracking = 0
FEATURE [Part::Extrusion] Extrude050  label="TxtDevice"
  Base = -> ShapeString040
  Dir = (0,0,1)
  DirMode = 2
  FaceMakerClass = Part::FaceMakerBullseye
  LengthFwd = 1
  LengthRev = 0
  Solid = true
  Symmetric = false
FEATURE [App::DocumentObjectGroupPython] FPSimLED145  label="LedAddDevice"  # scripted group (container) (typed FeaturePython)
  Group = -> [Extrude048,Extrude050]
FEATURE [Part::Part2DObjectPython] ShapeString041  # Draft 2D object (typed FeaturePython)
  FontFile = <path>
  Placement = pos=(1,10,0) rot=(0,0,1;0rad)
  Size = 3
  String = Track
  Tracking = 0
FEATURE [Part::Extrusion] Extrude051  label="TxtTrack"
  Base = -> ShapeString041
  Dir = (0,0,1)
  DirMode = 2
  FaceMakerClass = Part::FaceMakerBullseye
  LengthFwd = 1
  LengthRev = 0
  Solid = true
  Symmetric = false
FEATURE [App::DocumentObjectGroupPython] FPSimLED146  label="LedAddTrack"  # scripted group (container) (typed FeaturePython)
  Group = -> [Extrude049,Extrude051]
FEATURE [Part::Part2DObjectPython] ShapeString042  # Draft 2D object (typed FeaturePython)
  FontFile = <path>
  Placement = pos=(1,13,0) rot=(0,0,1;0rad)
  Size = 3
  String = Add
  Tracking = 0
FEATURE [Part::Extrusion] Extrude052  label="TxtAdd002"
  Base = -> ShapeString042
  Dir = (0,0,1)
  DirMode = 2
  FaceMakerClass = Part::FaceMakerBullseye
  LengthFwd = 2
  LengthRev = 1
  Solid = true
  Symmetric = false
FEATURE [Part::Part2DObjectPython] ShapeString043  # Draft 2D object (typed FeaturePython)
  FontFile = <path>
  Placement = pos=(1,10,0) rot=(0,0,1;0rad)
  Size = 3
  String = Device
  Tracking = 0
FEATURE [Part::Extrusion] Extrude053  label="TxtDevice001"
  Base = -> ShapeString043
  Dir = (0,0,1)
  DirMode = 2
  FaceMakerClass = Part::FaceMakerBullseye
  LengthFwd = 2
  LengthRev = 1
  Solid = true
  Symmetric = false
FEATURE [Part::Cut] Cut056
  Base = -> Box016
  Tool = -> Extrude052
FEATURE [Part::Cut] Cut057
  Base = -> Cut056
  Tool = -> Extrude053
FEATURE [App::DocumentObjectGroupPython] FPSimButton015  label="BtnAddDevice"  # scripted group (container) (typed FeaturePython)
  Group = -> [FPSimLED145,Cut057]
  PressureResolutionAng = (0,0,0)
  PressureResolutionLin = (0,0,0)
  RotationAngle = 0
  RotationAxis = (0,0,0)
  RotationCenter = (0,0,0)
  SwitchMode = false
  Translation = (0,0,-1)
FEATURE [App::Part] Part026  label="FrBtnAddDevice"
  Group = -> [Box016,FPSimButton015,ShapeString038,Extrude048,FPSimLED145,ShapeString040,Extrude050,ShapeString042,Extrude052,ShapeString043,Extrude053,Cut056,Cut057]
  License = CC BY 3.0
  LicenseURL = http://creativecommons.org/licenses/by/3.0/
  Origin = -> Origin027
  Placement = pos=(120,82,0) rot=(0,0,1;0rad)
FEATURE [Part::Part2DObjectPython] ShapeString044  # Draft 2D object (typed FeaturePython)
  FontFile = <path>
  Placement = pos=(1,13,0) rot=(0,0,1;0rad)
  Size = 3
  String = Add
  Tracking = 0
FEATURE [Part::Part2DObjectPython] ShapeString045  # Draft 2D object (typed FeaturePython)
  FontFile = <path>
  Placement = pos=(1,10,0) rot=(0,0,1;0rad)
  Size = 3
  String = Track
  Tracking = 0
FEATURE [Part::Extrusion] Extrude054  label="TxtTrack001"
  Base = -> ShapeString045
  Dir = (0,0,1)
  DirMode = 2
  FaceMakerClass = Part::FaceMakerBullseye
  LengthFwd = 2
  LengthRev = 1
  Solid = true
  Symmetric = false
FEATURE [Part::Extrusion] Extrude055  label="TxtAdd003"
  Base = -> ShapeString044
  Dir = (0,0,1)
  DirMode = 2
  FaceMakerClass = Part::FaceMakerBullseye
  LengthFwd = 2
  LengthRev = 1
  Solid = true
  Symmetric = false
FEATURE [Part::Cut] Cut058
  Base = -> Box015
  Tool = -> Extrude054
FEATURE [Part::Cut] Cut059
  Base = -> Cut058
  Tool = -> Extrude055
FEATURE [App::DocumentObjectGroupPython] FPSimButton014  label="BtnAddTrack"  # scripted group (container) (typed FeaturePython)
  Group = -> [FPSimLED146,Cut059]
  PressureResolutionAng = (0,0,0)
  PressureResolutionLin = (0,0,0)
  RotationAngle = 0
  RotationAxis = (0,0,0)
  RotationCenter = (0,0,0)
  SwitchMode = false
  Translation = (0,0,-1)
FEATURE [App::Part] Part027  label="FrBtnAddTrack"
  Group = -> [Box015,FPSimButton014,ShapeString039,Extrude049,FPSimLED146,ShapeString041,Extrude051,ShapeString045,Extrude054,ShapeString044,Extrude055,Cut058,Cut059]
  License = CC BY 3.0
  LicenseURL = http://creativecommons.org/licenses/by/3.0/
  Origin = -> Origin026
  Placement = pos=(120,63,0) rot=(0,0,1;0rad)
FEATURE [Part::Part2DObjectPython] ShapeString046  # Draft 2D object (typed FeaturePython)
  FontFile = <path>
  Placement = pos=(1,13,0) rot=(0,0,1;0rad)
  Size = 3
  String = Device
  Tracking = 0
FEATURE [Part::Part2DObjectPython] ShapeString047  # Draft 2D object (typed FeaturePython)
  FontFile = <path>
  Placement = pos=(1,10,0) rot=(0,0,1;0rad)
  Size = 3
  String = Device
  Tracking = 0
FEATURE [Part::Extrusion] Extrude057  label="TxtAdd004"
  Base = -> ShapeString046
  Dir = (0,0,1)
  DirMode = 2
  FaceMakerClass = Part::FaceMakerBullseye
  LengthFwd = 1
  LengthRev = 0
  Solid = true
  Symmetric = false
FEATURE [App::DocumentObjectGroupPython] FPSimLED147  label="LedDevice"  # scripted group (container) (typed FeaturePython)
  Group = -> [Extrude057]
FEATURE [Part::Part2DObjectPython] ShapeString048  # Draft 2D object (typed FeaturePython)
  FontFile = <path>
  Placement = pos=(1,13,0) rot=(0,0,1;0rad)
  Size = 3
  String = Device
  Tracking = 0
FEATURE [Part::Extrusion] Extrude058  label="TxtAdd005"
  Base = -> ShapeString048
  Dir = (0,0,1)
  DirMode = 2
  FaceMakerClass = Part::FaceMakerBullseye
  LengthFwd = 2
  LengthRev = 1
  Solid = true
  Symmetric = false
FEATURE [Part::Cut] Cut060
  Base = -> Box018
  Tool = -> Extrude058
FEATURE [App::DocumentObjectGroupPython] FPSimButton017  label="BtnDevice"  # scripted group (container) (typed FeaturePython)
  Group = -> [FPSimLED147,Cut060]
  PressureResolutionAng = (0,0,0)
  PressureResolutionLin = (0,0,0)
  RotationAngle = 0
  RotationAxis = (0,0,0)
  RotationCenter = (0,0,0)
  SwitchMode = false
  Translation = (0,0,-1)
FEATURE [App::Part] Part028  label="FrBtnDevice"
  Group = -> [Box018,FPSimButton017,ShapeString047,ShapeString046,Extrude057,FPSimLED147,ShapeString048,Extrude058,Cut060]
  License = CC BY 3.0
  LicenseURL = http://creativecommons.org/licenses/by/3.0/
  Origin = -> Origin029
  Placement = pos=(145,82,0) rot=(0,0,1;0rad)
FEATURE [Part::Box] Box250  label="Cube218"
  AttacherType = Attacher::AttachEngine3D
  Height = 1
  Length = 18.5
  Width = 18.5
FEATURE [Part::Part2DObjectPython] ShapeString049  # Draft 2D object (typed FeaturePython)
  FontFile = <path>
  Placement = pos=(1,13,0) rot=(0,0,1;0rad)
  Size = 3
  String = Mix
  Tracking = 0
FEATURE [Part::Extrusion] Extrude059  label="TxtAdd006"
  Base = -> ShapeString049
  Dir = (0,0,1)
  DirMode = 2
  FaceMakerClass = Part::FaceMakerBullseye
  LengthFwd = 2
  LengthRev = 1
  Solid = true
  Symmetric = false
FEATURE [Part::Cut] Cut061
  Base = -> Box250
  Tool = -> Extrude059
FEATURE [Part::Part2DObjectPython] ShapeString050  # Draft 2D object (typed FeaturePython)
  FontFile = <path>
  Placement = pos=(1,13,0) rot=(0,0,1;0rad)
  Size = 3
  String = Mix
  Tracking = 0
FEATURE [Part::Extrusion] Extrude060  label="TxtAdd007"
  Base = -> ShapeString050
  Dir = (0,0,1)
  DirMode = 2
  FaceMakerClass = Part::FaceMakerBullseye
  LengthFwd = 1
  LengthRev = 0
  Solid = true
  Symmetric = false
FEATURE [App::DocumentObjectGroupPython] FPSimLED148  label="LedMix"  # scripted group (container) (typed FeaturePython)
  Group = -> [Extrude060]
FEATURE [App::DocumentObjectGroupPython] FPSimButton016  label="BtnMix"  # scripted group (container) (typed FeaturePython)
  Group = -> [Cut061,FPSimLED148]
  PressureResolutionAng = (0,0,0)
  PressureResolutionLin = (0,0,0)
  RotationAngle = 0
  RotationAxis = (0,0,0)
  RotationCenter = (0,0,0)
  SwitchMode = false
  Translation = (0,0,-1)
FEATURE [App::Part] Part029  label="FrBtnMix"
  Group = -> [FPSimButton016,Box250,ShapeString049,Extrude059,Cut061,Extrude060,ShapeString050,FPSimLED148]
  License = CC BY 3.0
  LicenseURL = http://creativecommons.org/licenses/by/3.0/
  Origin = -> Origin028
  Placement = pos=(164,82,0) rot=(0,0,1;0rad)
FEATURE [Part::Box] Box251  label="Cube219"
  AttacherType = Attacher::AttachEngine3D
  Height = 1
  Length = 18.5
  Width = 18.5
FEATURE [Part::Part2DObjectPython] ShapeString051  # Draft 2D object (typed FeaturePython)
  FontFile = <path>
  Placement = pos=(1,13,0) rot=(0,0,1;0rad)
  Size = 3
  String = Browse
  Tracking = 0
FEATURE [Part::Extrusion] Extrude062  label="TxtAdd009"
  Base = -> ShapeString051
  Dir = (0,0,1)
  DirMode = 2
  FaceMakerClass = Part::FaceMakerBullseye
  LengthFwd = 2
  LengthRev = 1
  Solid = true
  Symmetric = false
FEATURE [Part::Cut] Cut062
  Base = -> Box251
  Tool = -> Extrude062
FEATURE [Part::Part2DObjectPython] ShapeString052  # Draft 2D object (typed FeaturePython)
  FontFile = <path>
  Placement = pos=(1,13,0) rot=(0,0,1;0rad)
  Size = 3
  String = Browse
  Tracking = 0
FEATURE [Part::Extrusion] Extrude061  label="TxtAdd008"
  Base = -> ShapeString052
  Dir = (0,0,1)
  DirMode = 2
  FaceMakerClass = Part::FaceMakerBullseye
  LengthFwd = 1
  LengthRev = 0
  Solid = true
  Symmetric = false
FEATURE [App::DocumentObjectGroupPython] FPSimLED149  label="LedBrowse"  # scripted group (container) (typed FeaturePython)
  Group = -> [Extrude061]
FEATURE [App::DocumentObjectGroupPython] FPSimButton019  label="BtnBrowse"  # scripted group (container) (typed FeaturePython)
  Group = -> [Cut062,FPSimLED149]
  PressureResolutionAng = (0,0,0)
  PressureResolutionLin = (0,0,0)
  RotationAngle = 0
  RotationAxis = (0,0,0)
  RotationCenter = (0,0,0)
  SwitchMode = false
  Translation = (0,0,-1)
FEATURE [App::Part] Part030  label="FrBtnBrowse"
  Group = -> [FPSimButton019,Box251,Extrude062,ShapeString051,Cut062,ShapeString052,Extrude061,FPSimLED149]
  License = CC BY 3.0
  LicenseURL = http://creativecommons.org/licenses/by/3.0/
  Origin = -> Origin031
  Placement = pos=(145,63,0) rot=(0,0,1;0rad)
FEATURE [Part::Box] Box252  label="Cube220"
  AttacherType = Attacher::AttachEngine3D
  Height = 1
  Length = 18.5
  Width = 18.5
FEATURE [Part::Part2DObjectPython] ShapeString053  # Draft 2D object (typed FeaturePython)
  FontFile = <path>
  Placement = pos=(1,13,0) rot=(0,0,1;0rad)
  Size = 3
  String = Clip
  Tracking = 0
FEATURE [Part::Extrusion] Extrude064  label="TxtAdd011"
  Base = -> ShapeString053
  Dir = (0,0,1)
  DirMode = 2
  FaceMakerClass = Part::FaceMakerBullseye
  LengthFwd = 2
  LengthRev = 1
  Solid = true
  Symmetric = false
FEATURE [Part::Cut] Cut063
  Base = -> Box252
  Tool = -> Extrude064
FEATURE [Part::Part2DObjectPython] ShapeString054  # Draft 2D object (typed FeaturePython)
  FontFile = <path>
  Placement = pos=(1,13,0) rot=(0,0,1;0rad)
  Size = 3
  String = Clip
  Tracking = 0
FEATURE [Part::Extrusion] Extrude063  label="TxtAdd010"
  Base = -> ShapeString054
  Dir = (0,0,1)
  DirMode = 2
  FaceMakerClass = Part::FaceMakerBullseye
  LengthFwd = 1
  LengthRev = 0
  Solid = true
  Symmetric = false
FEATURE [App::DocumentObjectGroupPython] FPSimLED150  label="LedClip"  # scripted group (container) (typed FeaturePython)
  Group = -> [Extrude063]
FEATURE [App::DocumentObjectGroupPython] FPSimButton018  label="BtnClip"  # scripted group (container) (typed FeaturePython)
  Group = -> [Cut063,FPSimLED150]
  PressureResolutionAng = (0,0,0)
  PressureResolutionLin = (0,0,0)
  RotationAngle = 0
  RotationAxis = (0,0,0)
  RotationCenter = (0,0,0)
  SwitchMode = false
  Translation = (0,0,-1)
FEATURE [App::Part] Part031  label="FrBtnClip"
  Group = -> [FPSimButton018,Extrude064,Box252,ShapeString053,Cut063,ShapeString054,Extrude063,FPSimLED150]
  License = CC BY 3.0
  LicenseURL = http://creativecommons.org/licenses/by/3.0/
  Origin = -> Origin030
  Placement = pos=(164,63,0) rot=(0,0,1;0rad)
FEATURE [App::DocumentObjectGroup] Group002  label="Center"
  Group = -> [Part024,Part025,Part026,Part027,Part028,Part029,Part030,Part031,Part032]
FEATURE [Part::Part2DObjectPython] ShapeString055  # Draft 2D object (typed FeaturePython)
  FontFile = <path>
  Placement = pos=(1,6,0) rot=(0,0,1;0rad)
  Size = 3
  String = Master
  Tracking = 0
FEATURE [Part::Extrusion] Extrude065  label="Txt036"
  Base = -> ShapeString055
  Dir = (0,0,1)
  DirMode = 2
  FaceMakerClass = Part::FaceMakerBullseye
  LengthFwd = 1
  LengthRev = 0
  Solid = true
  Symmetric = false
FEATURE [App::DocumentObjectGroupPython] FPSimLED151  label="LedMaster"  # scripted group (container) (typed FeaturePython)
  Group = -> [Extrude065]
FEATURE [Part::Part2DObjectPython] ShapeString056  # Draft 2D object (typed FeaturePython)
  FontFile = <path>
  Placement = pos=(1,6,0) rot=(0,0,1;0rad)
  Size = 3
  String = Master
  Tracking = 0
FEATURE [Part::Extrusion] Extrude066  label="Txt037"
  Base = -> ShapeString056
  Dir = (0,0,1)
  DirMode = 2
  FaceMakerClass = Part::FaceMakerBullseye
  LengthFwd = 2
  LengthRev = 1
  Solid = true
  Symmetric = false
FEATURE [Part::Cut] Cut064
  Base = -> Box044
  Tool = -> Extrude066
FEATURE [App::DocumentObjectGroupPython] FPSimButton040  label="BtnMaster"  # scripted group (container) (typed FeaturePython)
  Group = -> [FPSimLED151,Cut064]
  PressureResolutionAng = (0,0,0)
  PressureResolutionLin = (0,0,0)
  RotationAngle = 0
  RotationAxis = (0,0,0)
  RotationCenter = (0,0,0)
  SwitchMode = false
  Translation = (0,0,-1)
FEATURE [App::Part] Part054  label="FrBtnMaster"
  Group = -> [Box044,FPSimButton040,Extrude065,ShapeString055,FPSimLED151,ShapeString056,Extrude066,Cut064]
  License = CC BY 3.0
  LicenseURL = http://creativecommons.org/licenses/by/3.0/
  Origin = -> Origin054
  Placement = pos=(121,40,0) rot=(0,0,1;0rad)
FEATURE [Part::Part2DObjectPython] ShapeString057  # Draft 2D object (typed FeaturePython)
  FontFile = <path>
  Placement = pos=(1,13,0) rot=(0,0,1;0rad)
  Size = 3
  String = Repeat
  Tracking = 0
FEATURE [Part::Extrusion] Extrude067  label="Txt038"
  Base = -> ShapeString057
  Dir = (0,0,1)
  DirMode = 2
  FaceMakerClass = Part::FaceMakerBullseye
  LengthFwd = 1
  LengthRev = 0
  Solid = true
  Symmetric = false
FEATURE [App::DocumentObjectGroupPython] FPSimLED152  label="LedRepeat"  # scripted group (container) (typed FeaturePython)
  Group = -> [Extrude067]
FEATURE [Part::Part2DObjectPython] ShapeString058  # Draft 2D object (typed FeaturePython)
  FontFile = <path>
  Placement = pos=(1,13,0) rot=(0,0,1;0rad)
  Size = 3
  String = Repeat
  Tracking = 0
FEATURE [Part::Extrusion] Extrude068  label="Txt039"
  Base = -> ShapeString058
  Dir = (0,0,1)
  DirMode = 2
  FaceMakerClass = Part::FaceMakerBullseye
  LengthFwd = 2
  LengthRev = 1
  Solid = true
  Symmetric = false
FEATURE [Part::Cut] Cut065
  Base = -> Box166
  Tool = -> Extrude068
FEATURE [App::DocumentObjectGroupPython] FPSimButton059  label="BtnRepeat"  # scripted group (container) (typed FeaturePython)
  Group = -> [FPSimLED152,Cut065]
  RotationAngle = 0
  RotationAxis = (0,0,0)
  RotationCenter = (0,0,0)
  SwitchMode = false
  Translation = (0,0,-0.8)
FEATURE [App::Part] Part075  label="FrBtnRepeat"
  Group = -> [Box166,FPSimButton059,Extrude067,ShapeString057,FPSimLED152,ShapeString058,Extrude068,Cut065]
  License = CC BY 3.0
  LicenseURL = http://creativecommons.org/licenses/by/3.0/
  Origin = -> Origin075
  Placement = pos=(144.9,-52.8,0) rot=(0,0,1;0rad)
FEATURE [Part::Box] Box253  label="Cube221"
  AttacherType = Attacher::AttachEngine3D
  Height = 1
  Length = 19
  Width = 18.5
FEATURE [Part::Part2DObjectPython] ShapeString059  # Draft 2D object (typed FeaturePython)
  FontFile = <path>
  Placement = pos=(1,13,0) rot=(0,0,1;0rad)
  Size = 3
  String = Accent
  Tracking = 0
FEATURE [Part::Extrusion] Extrude069  label="Txt040"
  Base = -> ShapeString059
  Dir = (0,0,1)
  DirMode = 2
  FaceMakerClass = Part::FaceMakerBullseye
  LengthFwd = 1
  LengthRev = 0
  Solid = true
  Symmetric = false
FEATURE [App::DocumentObjectGroupPython] FPSimLED153  label="LedAccent"  # scripted group (container) (typed FeaturePython)
  Group = -> [Extrude069]
FEATURE [Part::Part2DObjectPython] ShapeString060  # Draft 2D object (typed FeaturePython)
  FontFile = <path>
  Placement = pos=(1,13,0) rot=(0,0,1;0rad)
  Size = 3
  String = Accent
  Tracking = 0
FEATURE [Part::Extrusion] Extrude070  label="Txt041"
  Base = -> ShapeString060
  Dir = (0,0,1)
  DirMode = 2
  FaceMakerClass = Part::FaceMakerBullseye
  LengthFwd = 2
  LengthRev = 1
  Solid = true
  Symmetric = false
FEATURE [Part::Cut] Cut066
  Base = -> Box253
  Tool = -> Extrude070
FEATURE [App::DocumentObjectGroupPython] FPSimButton060  label="BtnAccent"  # scripted group (container) (typed FeaturePython)
  Group = -> [FPSimLED153,Cut066]
  RotationAngle = 0
  RotationAxis = (0,0,0)
  RotationCenter = (0,0,0)
  SwitchMode = false
  Translation = (0,0,-0.8)
FEATURE [App::Part] Part076  label="FrBtnAccent"
  Group = -> [FPSimButton060,Extrude069,ShapeString059,FPSimLED153,Box253,Extrude070,ShapeString060,Cut066]
  License = CC BY 3.0
  LicenseURL = http://creativecommons.org/licenses/by/3.0/
  Origin = -> Origin076
  Placement = pos=(163.9,-52.8,0) rot=(0,0,1;0rad)
FEATURE [Part::Part2DObjectPython] ShapeString061  # Draft 2D object (typed FeaturePython)
  FontFile = <path>
  Placement = pos=(1,6,0) rot=(0,0,1;0rad)
  Size = 3
  String = Scale
  Tracking = 0
FEATURE [Part::Extrusion] Extrude071  label="Txt042"
  Base = -> ShapeString061
  Dir = (0,0,1)
  DirMode = 2
  FaceMakerClass = Part::FaceMakerBullseye
  LengthFwd = 1
  LengthRev = 0
  Solid = true
  Symmetric = false
FEATURE [App::DocumentObjectGroupPython] FPSimLED154  label="LedScale"  # scripted group (container) (typed FeaturePython)
  Group = -> [Extrude071]
FEATURE [Part::Part2DObjectPython] ShapeString062  # Draft 2D object (typed FeaturePython)
  FontFile = <path>
  Placement = pos=(1,6,0) rot=(0,0,1;0rad)
  Size = 3
  String = Scale
  Tracking = 0
FEATURE [Part::Extrusion] Extrude072  label="Txt043"
  Base = -> ShapeString062
  Dir = (0,0,1)
  DirMode = 2
  FaceMakerClass = Part::FaceMakerBullseye
  LengthFwd = 2
  LengthRev = 1
  Solid = true
  Symmetric = false
FEATURE [Part::Cut] Cut067
  Base = -> Box168
  Tool = -> Extrude072
FEATURE [App::DocumentObjectGroupPython] FPSimButton061  label="BtnScale"  # scripted group (container) (typed FeaturePython)
  Group = -> [FPSimLED154,Cut067]
  RotationAngle = 0
  RotationAxis = (0,0,0)
  RotationCenter = (0,0,0)
  SwitchMode = false
  Translation = (0,0,-0.8)
FEATURE [App::Part] Part077  label="FrBtnScale"
  Group = -> [Box168,FPSimButton061,ShapeString061,Extrude071,FPSimLED154,ShapeString062,Extrude072,Cut067]
  License = CC BY 3.0
  LicenseURL = http://creativecommons.org/licenses/by/3.0/
  Origin = -> Origin077
  Placement = pos=(144.9,-66.8,0) rot=(0,0,1;0rad)
FEATURE [Part::Box] Box254  label="Cube222"
  AttacherType = Attacher::AttachEngine3D
  Height = 1
  Length = 19
  Width = 11
FEATURE [Part::Part2DObjectPython] ShapeString063  # Draft 2D object (typed FeaturePython)
  FontFile = <path>
  Placement = pos=(1,6,0) rot=(0,0,1;0rad)
  Size = 3
  String = Layout
  Tracking = 0
FEATURE [Part::Extrusion] Extrude073  label="Txt044"
  Base = -> ShapeString063
  Dir = (0,0,1)
  DirMode = 2
  FaceMakerClass = Part::FaceMakerBullseye
  LengthFwd = 1
  LengthRev = 0
  Solid = true
  Symmetric = false
FEATURE [Part::Part2DObjectPython] ShapeString064  # Draft 2D object (typed FeaturePython)
  FontFile = <path>
  Placement = pos=(1,6,0) rot=(0,0,1;0rad)
  Size = 3
  String = Layout
  Tracking = 0
FEATURE [Part::Extrusion] Extrude074  label="Txt045"
  Base = -> ShapeString064
  Dir = (0,0,1)
  DirMode = 2
  FaceMakerClass = Part::FaceMakerBullseye
  LengthFwd = 2
  LengthRev = 1
  Solid = true
  Symmetric = false
FEATURE [Part::Cut] Cut068
  Base = -> Box254
  Tool = -> Extrude074
FEATURE [App::DocumentObjectGroupPython] FPSimLED155  label="LedLayout"  # scripted group (container) (typed FeaturePython)
  Group = -> [Extrude073]
FEATURE [App::DocumentObjectGroupPython] FPSimButton062  label="BtnLayout"  # scripted group (container) (typed FeaturePython)
  Group = -> [Cut068,FPSimLED155]
  RotationAngle = 0
  RotationAxis = (0,0,0)
  RotationCenter = (0,0,0)
  SwitchMode = false
  Translation = (0,0,-0.8)
FEATURE [App::Part] Part078  label="FrBtnLayout"
  Group = -> [FPSimButton062,ShapeString064,Box254,Extrude074,Cut068,Extrude073,ShapeString063,FPSimLED155]
  License = CC BY 3.0
  LicenseURL = http://creativecommons.org/licenses/by/3.0/
  Origin = -> Origin078
  Placement = pos=(163.9,-66.8,0) rot=(0,0,1;0rad)
FEATURE [Part::Part2DObjectPython] ShapeString065  # Draft 2D object (typed FeaturePython)
  FontFile = <path>
  Placement = pos=(1,13,0) rot=(0,0,1;0rad)
  Size = 3
  String = Note
  Tracking = 0
FEATURE [Part::Extrusion] Extrude075  label="Txt046"
  Base = -> ShapeString065
  Dir = (0,0,1)
  DirMode = 2
  FaceMakerClass = Part::FaceMakerBullseye
  LengthFwd = 1
  LengthRev = 0
  Solid = true
  Symmetric = false
FEATURE [App::DocumentObjectGroupPython] FPSimLED156  label="LedNote"  # scripted group (container) (typed FeaturePython)
  Group = -> [Extrude075]
FEATURE [Part::Part2DObjectPython] ShapeString066  # Draft 2D object (typed FeaturePython)
  FontFile = <path>
  Placement = pos=(1,13,0) rot=(0,0,1;0rad)
  Size = 3
  String = Note
  Tracking = 0
FEATURE [Part::Extrusion] Extrude076  label="Txt047"
  Base = -> ShapeString066
  Dir = (0,0,1)
  DirMode = 2
  FaceMakerClass = Part::FaceMakerBullseye
  LengthFwd = 2
  LengthRev = 1
  Solid = true
  Symmetric = false
FEATURE [Part::Cut] Cut069
  Base = -> Box170
  Tool = -> Extrude076
FEATURE [App::DocumentObjectGroupPython] FPSimButton064  label="BtnNote"  # scripted group (container) (typed FeaturePython)
  Group = -> [FPSimLED156,Cut069]
  RotationAngle = 0
  RotationAxis = (0,0,0)
  RotationCenter = (0,0,0)
  SwitchMode = false
  Translation = (0,0,-0.8)
FEATURE [App::Part] Part079  label="FrBtnNote"
  Group = -> [Box170,FPSimButton064,Extrude075,ShapeString065,FPSimLED156,ShapeString066,Extrude076,Cut069]
  License = CC BY 3.0
  LicenseURL = http://creativecommons.org/licenses/by/3.0/
  Origin = -> Origin079
  Placement = pos=(144.9,-85.3,0) rot=(0,0,1;0rad)
FEATURE [Part::Box] Box255  label="Cube223"
  AttacherType = Attacher::AttachEngine3D
  Height = 1
  Length = 19
  Width = 18.5
FEATURE [Part::Part2DObjectPython] ShapeString067  # Draft 2D object (typed FeaturePython)
  FontFile = <path>
  Placement = pos=(1,13,0) rot=(0,0,1;0rad)
  Size = 3
  String = Session
  Tracking = 0
FEATURE [Part::Extrusion] Extrude078  label="Txt049"
  Base = -> ShapeString067
  Dir = (0,0,1)
  DirMode = 2
  FaceMakerClass = Part::FaceMakerBullseye
  LengthFwd = 2
  LengthRev = 1
  Solid = true
  Symmetric = false
FEATURE [Part::Part2DObjectPython] ShapeString068  # Draft 2D object (typed FeaturePython)
  FontFile = <path>
  Placement = pos=(1,13,0) rot=(0,0,1;0rad)
  Size = 3
  String = Session
  Tracking = 0
FEATURE [Part::Extrusion] Extrude077  label="Txt048"
  Base = -> ShapeString068
  Dir = (0,0,1)
  DirMode = 2
  FaceMakerClass = Part::FaceMakerBullseye
  LengthFwd = 1
  LengthRev = 0
  Solid = true
  Symmetric = false
FEATURE [App::DocumentObjectGroupPython] FPSimLED157  label="LedSession"  # scripted group (container) (typed FeaturePython)
  Group = -> [Extrude077]
FEATURE [Part::Cut] Cut070
  Base = -> Box255
  Tool = -> Extrude078
FEATURE [App::DocumentObjectGroupPython] FPSimButton063  label="BtnSession"  # scripted group (container) (typed FeaturePython)
  Group = -> [FPSimLED157,Cut070]
  RotationAngle = 0
  RotationAxis = (0,0,0)
  RotationCenter = (0,0,0)
  SwitchMode = false
  Translation = (0,0,-0.8)
FEATURE [App::Part] Part080  label="FrBtnSession"
  Group = -> [FPSimButton063,Extrude077,ShapeString068,FPSimLED157,Extrude078,ShapeString067,Box255,Cut070]
  License = CC BY 3.0
  LicenseURL = http://creativecommons.org/licenses/by/3.0/
  Origin = -> Origin080
  Placement = pos=(163.9,-85.3,0) rot=(0,0,1;0rad)
FEATURE [Part::Part2DObjectPython] ShapeString069  # Draft 2D object (typed FeaturePython)
  FontFile = <path>
  Placement = pos=(1,6,0) rot=(0,0,1;0rad)
  Size = 3
  String = Shift
  Tracking = 0
FEATURE [Part::Extrusion] Extrude079  label="Txt050"
  Base = -> ShapeString069
  Dir = (0,0,1)
  DirMode = 2
  FaceMakerClass = Part::FaceMakerBullseye
  LengthFwd = 1
  LengthRev = 0
  Solid = true
  Symmetric = false
FEATURE [App::DocumentObjectGroupPython] FPSimLED158  label="LedShift"  # scripted group (container) (typed FeaturePython)
  Group = -> [Extrude079]
FEATURE [Part::Part2DObjectPython] ShapeString070  # Draft 2D object (typed FeaturePython)
  FontFile = <path>
  Placement = pos=(1,6,0) rot=(0,0,1;0rad)
  Size = 3
  String = Shift
  Tracking = 0
FEATURE [Part::Extrusion] Extrude080  label="Txt051"
  Base = -> ShapeString070
  Dir = (0,0,1)
  DirMode = 2
  FaceMakerClass = Part::FaceMakerBullseye
  LengthFwd = 2
  LengthRev = 1
  Solid = true
  Symmetric = false
FEATURE [Part::Cut] Cut071
  Base = -> Box164
  Tool = -> Extrude080
FEATURE [App::DocumentObjectGroupPython] FPSimButton057  label="BtnShift"  # scripted group (container) (typed FeaturePython)
  Group = -> [FPSimLED158,Cut071]
  RotationAngle = 0
  RotationAxis = (0,0,0)
  RotationCenter = (0,0,0)
  SwitchMode = false
  Translation = (0,0,-0.8)
FEATURE [App::Part] Part073  label="FrBtnShift"
  Group = -> [Box164,FPSimButton057,Extrude079,ShapeString069,FPSimLED158,ShapeString070,Extrude080,Cut071]
  License = CC BY 3.0
  LicenseURL = http://creativecommons.org/licenses/by/3.0/
  Origin = -> Origin073
  Placement = pos=(144.9,-140.8,0) rot=(0,0,1;0rad)
FEATURE [Part::Box] Box256  label="Cube224"
  AttacherType = Attacher::AttachEngine3D
  Height = 1
  Length = 19
  Width = 11
FEATURE [Part::Part2DObjectPython] ShapeString071  # Draft 2D object (typed FeaturePython)
  FontFile = <path>
  Placement = pos=(1,6,0) rot=(0,0,1;0rad)
  Size = 3
  String = Select
  Tracking = 0
FEATURE [Part::Extrusion] Extrude081  label="Txt052"
  Base = -> ShapeString071
  Dir = (0,0,1)
  DirMode = 2
  FaceMakerClass = Part::FaceMakerBullseye
  LengthFwd = 2
  LengthRev = 1
  Solid = true
  Symmetric = false
FEATURE [Part::Cut] Cut072
  Base = -> Box256
  Tool = -> Extrude081
FEATURE [Part::Part2DObjectPython] ShapeString072  # Draft 2D object (typed FeaturePython)
  FontFile = <path>
  Placement = pos=(1,6,0) rot=(0,0,1;0rad)
  Size = 3
  String = Select
  Tracking = 0
FEATURE [Part::Extrusion] Extrude082  label="Txt053"
  Base = -> ShapeString072
  Dir = (0,0,1)
  DirMode = 2
  FaceMakerClass = Part::FaceMakerBullseye
  LengthFwd = 1
  LengthRev = 0
  Solid = true
  Symmetric = false
FEATURE [App::DocumentObjectGroupPython] FPSimLED159  label="LedSelect"  # scripted group (container) (typed FeaturePython)
  Group = -> [Extrude082]
FEATURE [App::DocumentObjectGroupPython] FPSimButton058  label="BtnSelect"  # scripted group (container) (typed FeaturePython)
  Group = -> [FPSimLED159,Cut072]
  RotationAngle = 0
  RotationAxis = (0,0,0)
  RotationCenter = (0,0,0)
  SwitchMode = false
  Translation = (0,0,-0.8)
FEATURE [App::Part] Part074  label="FrBtnSelect"
  Group = -> [FPSimButton058,Extrude082,ShapeString072,FPSimLED159,ShapeString071,Extrude081,Box256,Cut072]
  License = CC BY 3.0
  LicenseURL = http://creativecommons.org/licenses/by/3.0/
  Origin = -> Origin074
  Placement = pos=(163.9,-140.8,0) rot=(0,0,1;0rad)
FEATURE [Part::Part2DObjectPython] ShapeString073  # Draft 2D object (typed FeaturePython)
  FontFile = <path>
  Placement = pos=(6,-11,0) rot=(0,0,1;3.14159rad)
  Size = 3
  String = Octave
  Tracking = 0
FEATURE [Part::Extrusion] Extrude083  label="OctaveUp001"
  Base = -> ShapeString073
  Dir = (0,0,1)
  DirMode = 2
  FaceMakerClass = Part::FaceMakerBullseye
  LengthFwd = 1
  LengthRev = 0
  Solid = true
  Symmetric = false
FEATURE [App::DocumentObjectGroupPython] FPSimLED044  label="LedOctaveUp"  # scripted group (container) (typed FeaturePython)
  Group = -> [Fusion032,Extrude083]
FEATURE [Part::Part2DObjectPython] ShapeString074  # Draft 2D object (typed FeaturePython)
  FontFile = <path>
  Placement = pos=(6,-11,0) rot=(0,0,1;3.14159rad)
  Size = 3
  String = Octave
  Tracking = 0
FEATURE [Part::Extrusion] Extrude084  label="Octave001"
  Base = -> ShapeString074
  Dir = (0,0,1)
  DirMode = 2
  FaceMakerClass = Part::FaceMakerBullseye
  LengthFwd = 2
  LengthRev = 1
  Solid = true
  Symmetric = false
FEATURE [Part::Cut] Cut073
  Base = -> Cut015
  Tool = -> Extrude084
FEATURE [App::DocumentObjectGroupPython] FPSimButton053  label="BtnOctaveUp"  # scripted group (container) (typed FeaturePython)
  Group = -> [FPSimLED044,Cut073]
  PressureResolutionAng = (0,0,0)
  PressureResolutionLin = (0,0,0)
  RotationAngle = 0
  RotationAxis = (0,0,0)
  RotationCenter = (0,0,0)
  SwitchMode = false
  Translation = (0,0,-1)
FEATURE [App::Part] Part070  label="FrOctaveUp"
  Group = -> [FPSimLED044,Box115,Fusion031,Sketch016,Cut015,Box102,Extrude004,FPSimButton053,Box173,Box172,Fusion032,Sketch019,ShapeString073,Extrude083,ShapeString074,Extrude084,Cut073]
  License = CC BY 3.0
  LicenseURL = http://creativecommons.org/licenses/by/3.0/
  Origin = -> Origin070
  Placement = pos=(0,0.25,0) rot=(0,0,1;3.14159rad)
FEATURE [Part::Part2DObjectPython] ShapeString075  # Draft 2D object (typed FeaturePython)
  FontFile = <path>
  Placement = pos=(-6,-13,0) rot=(0,0,1;0rad)
  Size = 3
  String = Octave
  Tracking = 0
FEATURE [Part::Extrusion] Extrude085  label="OctaveDown002"
  Base = -> ShapeString075
  Dir = (0,0,1)
  DirMode = 2
  FaceMakerClass = Part::FaceMakerBullseye
  LengthFwd = 1
  LengthRev = 0
  Solid = true
  Symmetric = false
FEATURE [App::DocumentObjectGroupPython] FPSimLED043  label="LedOctaveDown"  # scripted group (container) (typed FeaturePython)
  Group = -> [Fusion025,Extrude085]
FEATURE [Part::Part2DObjectPython] ShapeString076  # Draft 2D object (typed FeaturePython)
  FontFile = <path>
  Placement = pos=(-6,-13,0) rot=(0,0,1;0rad)
  Size = 3
  String = Octave
  Tracking = 0
FEATURE [Part::Extrusion] Extrude086  label="OctaveDown003"
  Base = -> ShapeString076
  Dir = (0,0,1)
  DirMode = 2
  FaceMakerClass = Part::FaceMakerBullseye
  LengthFwd = 2
  LengthRev = 1
  Solid = true
  Symmetric = false
FEATURE [Part::Cut] Cut074
  Base = -> Cut013
  Tool = -> Extrude086
FEATURE [App::DocumentObjectGroupPython] FPSimButton054  label="BtnOctaveDown"  # scripted group (container) (typed FeaturePython)
  Group = -> [FPSimLED043,Cut074]
  PressureResolutionAng = (0,0,0)
  PressureResolutionLin = (0,0,0)
  RotationAngle = 0
  RotationAxis = (0,0,0)
  RotationCenter = (0,0,0)
  SwitchMode = false
  Translation = (0,0,-1)
FEATURE [App::Part] Part068  label="FrOctaveDown"
  Group = -> [FPSimLED043,Box103,Box104,Fusion024,Fusion025,Box106,Sketch015,Cut013,Box108,Extrude006,FPSimButton054,ShapeString075,Extrude085,ShapeString076,Extrude086,Cut074]
  License = CC BY 3.0
  LicenseURL = http://creativecommons.org/licenses/by/3.0/
  Origin = -> Origin069
  Placement = pos=(0,-0.25,0) rot=(0,0,1;0rad)
FEATURE [Part::Part2DObjectPython] ShapeString077  # Draft 2D object (typed FeaturePython)
  FontFile = <path>
  Placement = pos=(1,-17,0) rot=(0,0,1;1.5708rad)
  Size = 3
  String = Page
  Tracking = 0
FEATURE [Part::Extrusion] Extrude087  label="StrPage"
  Base = -> ShapeString077
  Dir = (0,0,1)
  DirMode = 2
  FaceMakerClass = Part::FaceMakerBullseye
  LengthFwd = 1
  LengthRev = 0
  Solid = true
  Symmetric = false
FEATURE [App::DocumentObjectGroupPython] FPSimLED046  label="LedPageLeft"  # scripted group (container) (typed FeaturePython)
  Group = -> [Fusion033,Extrude087]
FEATURE [Part::Part2DObjectPython] ShapeString078  # Draft 2D object (typed FeaturePython)
  FontFile = <path>
  Placement = pos=(1,-17,0) rot=(0,0,1;1.5708rad)
  Size = 3
  String = Page
  Tracking = 0
FEATURE [Part::Extrusion] Extrude088  label="StrPage001"
  Base = -> ShapeString078
  Dir = (0,0,1)
  DirMode = 2
  FaceMakerClass = Part::FaceMakerBullseye
  LengthFwd = 2
  LengthRev = 1
  Solid = true
  Symmetric = false
FEATURE [Part::Cut] Cut075
  Base = -> Cut014
  Tool = -> Extrude088
FEATURE [App::DocumentObjectGroupPython] FPSimButton056  label="BtnPageLeft"  # scripted group (container) (typed FeaturePython)
  Group = -> [FPSimLED046,Cut075]
  PressureResolutionAng = (0,0,0)
  PressureResolutionLin = (0,0,0)
  RotationAngle = 0
  RotationAxis = (0,0,0)
  RotationCenter = (0,0,0)
  SwitchMode = false
  Translation = (0,0,-1)
FEATURE [App::Part] Part071  label="FrPageLeft"
  Group = -> [FPSimLED046,Box114,Fusion027,Sketch017,Cut014,Box105,Extrude005,FPSimButton056,Box174,Box175,Fusion033,ShapeString077,Extrude087,ShapeString078,Extrude088,Cut075]
  License = CC BY 3.0
  LicenseURL = http://creativecommons.org/licenses/by/3.0/
  Origin = -> Origin072
  Placement = pos=(-0.25,0,0) rot=(0,0,1;4.71239rad)
FEATURE [Part::Part2DObjectPython] ShapeString079  # Draft 2D object (typed FeaturePython)
  FontFile = <path>
  Placement = pos=(-1,-9,0) rot=(0,0,-1;1.5708rad)
  Size = 3
  String = Page
  Tracking = 0
FEATURE [Part::Extrusion] Extrude089  label="StrPage002"
  Base = -> ShapeString079
  Dir = (0,0,1)
  DirMode = 2
  FaceMakerClass = Part::FaceMakerBullseye
  LengthFwd = 1
  LengthRev = 0
  Solid = true
  Symmetric = false
FEATURE [App::DocumentObjectGroupPython] FPSimLED045  label="LedPageRight"  # scripted group (container) (typed FeaturePython)
  Group = -> [Fusion034,Extrude089]
FEATURE [Part::Part2DObjectPython] ShapeString080  # Draft 2D object (typed FeaturePython)
  FontFile = <path>
  Placement = pos=(-1,-9,0) rot=(0,0,-1;1.5708rad)
  Size = 3
  String = Page
  Tracking = 0
FEATURE [Part::Extrusion] Extrude090  label="StrPage003"
  Base = -> ShapeString080
  Dir = (0,0,1)
  DirMode = 2
  FaceMakerClass = Part::FaceMakerBullseye
  LengthFwd = 2
  LengthRev = 1
  Solid = true
  Symmetric = false
FEATURE [Part::Cut] Cut076
  Base = -> Cut016
  Tool = -> Extrude090
FEATURE [App::DocumentObjectGroupPython] FPSimButton055  label="BtnPageRight"  # scripted group (container) (typed FeaturePython)
  Group = -> [FPSimLED045,Cut076]
  PressureResolutionAng = (0,0,0)
  PressureResolutionLin = (0,0,0)
  RotationAngle = 0
  RotationAxis = (0,0,0)
  RotationCenter = (0,0,0)
  SwitchMode = false
  Translation = (0,0,-1)
FEATURE [App::Part] Part072  label="FrPageRight"
  Group = -> [FPSimLED045,Box111,Fusion030,Sketch018,Cut016,Box113,Extrude007,FPSimButton055,Box176,Box177,Fusion034,ShapeString079,Extrude089,ShapeString080,Extrude090,Cut076]
  License = CC BY 3.0
  LicenseURL = http://creativecommons.org/licenses/by/3.0/
  Origin = -> Origin068
  Placement = pos=(0.25,0,0) rot=(0,0,1;1.5708rad)
FEATURE [App::Part] Part069  label="FrNavigArrows2"
  Group = -> [Part068,Part070,Part071,Part072]
  License = CC BY 3.0
  LicenseURL = http://creativecommons.org/licenses/by/3.0/
  Origin = -> Origin071
  Placement = pos=(164,-108,0) rot=(0,0,1;0rad)
FEATURE [Part::Part2DObjectPython] ShapeString081  # Draft 2D object (typed FeaturePython)
  FontFile = <path>
  Placement = pos=(1,13,0) rot=(0,0,1;0rad)
  Size = 3
  String = 1/32t
  Tracking = 0
FEATURE [Part::Extrusion] Extrude091  label="Txt054"
  Base = -> ShapeString081
  Dir = (0,0,1)
  DirMode = 2
  FaceMakerClass = Part::FaceMakerBullseye
  LengthFwd = 1
  LengthRev = 0
  Solid = true
  Symmetric = false
FEATURE [App::DocumentObjectGroupPython] FPSimLED031  label="LedSel[0]"  # scripted group (container) (typed FeaturePython)
  Group = -> [Fusion001,Extrude091]
FEATURE [Part::Part2DObjectPython] ShapeString082  # Draft 2D object (typed FeaturePython)
  FontFile = <path>
  Placement = pos=(1,13,0) rot=(0,0,1;0rad)
  Size = 3
  String = 1/32t
  Tracking = 0
FEATURE [Part::Extrusion] Extrude092  label="Txt055"
  Base = -> ShapeString082
  Dir = (0,0,1)
  DirMode = 2
  FaceMakerClass = Part::FaceMakerBullseye
  LengthFwd = 2
  LengthRev = 1
  Solid = true
  Symmetric = false
FEATURE [Part::Cut] Cut077
  Base = -> Cut001
  Tool = -> Extrude092
FEATURE [App::DocumentObjectGroupPython] FPSimButton041  label="BtnSel[0]"  # scripted group (container) (typed FeaturePython)
  Group = -> [FPSimLED031,Cut077]
  PressureResolutionAng = (0,0,0)
  PressureResolutionLin = (0,0,0)
  RotationAngle = 0
  RotationAxis = (0,0,0)
  RotationCenter = (0,0,0)
  SwitchMode = false
  Translation = (0,0,-1)
FEATURE [App::Part] Part055  label="FrBtnSel[0]"
  Group = -> [Box045,FPSimButton041,Box046,Box047,Fusion,Cut001,Box049,Fusion001,Box048,FPSimLED031,ShapeString081,Extrude091,ShapeString082,Extrude092,Cut077]
  License = CC BY 3.0
  LicenseURL = http://creativecommons.org/licenses/by/3.0/
  Origin = -> Origin055
  Placement = pos=(120,13,0) rot=(0,0,1;0rad)
FEATURE [Part::Box] Box257  label="Cube225"
  AttacherType = Attacher::AttachEngine3D
  Height = 1
  Length = 18.5
  Width = 18.5
FEATURE [Part::Box] Box258  label="Cube226"
  AttacherType = Attacher::AttachEngine3D
  Height = 2
  Length = 1
  Placement = pos=(0,0,0) rot=(0,0,1;0.785398rad)
  Width = 5
FEATURE [Part::Box] Box259  label="Cube227"
  AttacherType = Attacher::AttachEngine3D
  Height = 2
  Length = 1
  Placement = pos=(0,0,0) rot=(0,0,1;2.35619rad)
  Width = 4
FEATURE [Part::MultiFuse] Fusion036  label="LilArrowHole008"
  Placement = pos=(16,5,0) rot=(0,0,1;0rad)
  Shapes = -> [Box258,Box259]
FEATURE [Part::Cut] Cut078
  Base = -> Box257
  Tool = -> Fusion036
FEATURE [Part::Box] Box260  label="Cube228"
  AttacherType = Attacher::AttachEngine3D
  Height = 1
  Length = 1
  Placement = pos=(0,0,0) rot=(0,0,1;2.35619rad)
  Width = 4
FEATURE [Part::Box] Box261  label="Cube229"
  AttacherType = Attacher::AttachEngine3D
  Height = 1
  Length = 1
  Placement = pos=(0,0,0) rot=(0,0,1;0.785398rad)
  Width = 5
FEATURE [Part::MultiFuse] Fusion035  label="LilArrow008"
  Placement = pos=(16,5,0) rot=(0,0,1;0rad)
  Shapes = -> [Box260,Box261]
FEATURE [Part::Part2DObjectPython] ShapeString083  # Draft 2D object (typed FeaturePython)
  FontFile = <path>
  Placement = pos=(1,13,0) rot=(0,0,1;0rad)
  Size = 3
  String = 1/32
  Tracking = 0
FEATURE [Part::Extrusion] Extrude094  label="Txt057"
  Base = -> ShapeString083
  Dir = (0,0,1)
  DirMode = 2
  FaceMakerClass = Part::FaceMakerBullseye
  LengthFwd = 2
  LengthRev = 1
  Solid = true
  Symmetric = false
FEATURE [Part::Cut] Cut079
  Base = -> Cut078
  Tool = -> Extrude094
FEATURE [Part::Part2DObjectPython] ShapeString084  # Draft 2D object (typed FeaturePython)
  FontFile = <path>
  Placement = pos=(1,13,0) rot=(0,0,1;0rad)
  Size = 3
  String = 1/32
  Tracking = 0
FEATURE [Part::Extrusion] Extrude093  label="Txt056"
  Base = -> ShapeString084
  Dir = (0,0,1)
  DirMode = 2
  FaceMakerClass = Part::FaceMakerBullseye
  LengthFwd = 1
  LengthRev = 0
  Solid = true
  Symmetric = false
FEATURE [App::DocumentObjectGroupPython] FPSimLED160  label="LedSel[1]"  # scripted group (container) (typed FeaturePython)
  Group = -> [Fusion035,Extrude093]
FEATURE [App::DocumentObjectGroupPython] FPSimButton042  label="BtnSel[1]"  # scripted group (container) (typed FeaturePython)
  Group = -> [Cut079,FPSimLED160]
  PressureResolutionAng = (0,0,0)
  PressureResolutionLin = (0,0,0)
  RotationAngle = 0
  RotationAxis = (0,0,0)
  RotationCenter = (0,0,0)
  SwitchMode = false
  Translation = (0,0,-1)
FEATURE [App::Part] Part056  label="FrBtnSel[1]"
  Group = -> [FPSimButton042,Box259,Fusion036,ShapeString083,Box258,Box257,Extrude094,Cut078,Cut079,Fusion035,Extrude093,Box261,Box260,ShapeString084,FPSimLED160]
  License = CC BY 3.0
  LicenseURL = http://creativecommons.org/licenses/by/3.0/
  Origin = -> Origin056
  Placement = pos=(120,-9,0) rot=(0,0,1;0rad)
FEATURE [Part::Part2DObjectPython] ShapeString085  # Draft 2D object (typed FeaturePython)
  FontFile = <path>
  Placement = pos=(1,13,0) rot=(0,0,1;0rad)
  Size = 3
  String = 1/16t
  Tracking = 0
FEATURE [Part::Extrusion] Extrude095  label="Txt058"
  Base = -> ShapeString085
  Dir = (0,0,1)
  DirMode = 2
  FaceMakerClass = Part::FaceMakerBullseye
  LengthFwd = 1
  LengthRev = 0
  Solid = true
  Symmetric = false
FEATURE [App::DocumentObjectGroupPython] FPSimLED033  label="LedSel[2]"  # scripted group (container) (typed FeaturePython)
  Group = -> [Fusion005,Extrude095]
FEATURE [Part::Part2DObjectPython] ShapeString086  # Draft 2D object (typed FeaturePython)
  FontFile = <path>
  Placement = pos=(1,13,0) rot=(0,0,1;0rad)
  Size = 3
  String = 1/16t
  Tracking = 0
FEATURE [Part::Extrusion] Extrude096  label="Txt059"
  Base = -> ShapeString086
  Dir = (0,0,1)
  DirMode = 2
  FaceMakerClass = Part::FaceMakerBullseye
  LengthFwd = 2
  LengthRev = 1
  Solid = true
  Symmetric = false
FEATURE [Part::Cut] Cut080
  Base = -> Cut003
  Tool = -> Extrude096
FEATURE [App::DocumentObjectGroupPython] FPSimButton043  label="BtnSel[2]"  # scripted group (container) (typed FeaturePython)
  Group = -> [FPSimLED033,Cut080]
  PressureResolutionAng = (0,0,0)
  PressureResolutionLin = (0,0,0)
  RotationAngle = 0
  RotationAxis = (0,0,0)
  RotationCenter = (0,0,0)
  SwitchMode = false
  Translation = (0,0,-1)
FEATURE [App::Part] Part057  label="FrBtnSel[2]"
  Group = -> [Box055,FPSimButton043,Box057,Box058,Fusion004,Cut003,Box056,Fusion005,Box059,FPSimLED033,ShapeString085,Extrude095,ShapeString086,Extrude096,Cut080]
  License = CC BY 3.0
  LicenseURL = http://creativecommons.org/licenses/by/3.0/
  Origin = -> Origin057
  Placement = pos=(120,-31,0) rot=(0,0,1;0rad)
FEATURE [Part::Part2DObjectPython] ShapeString087  # Draft 2D object (typed FeaturePython)
  FontFile = <path>
  Placement = pos=(1,13,0) rot=(0,0,1;0rad)
  Size = 3
  String = 1/16
  Tracking = 0
FEATURE [Part::Extrusion] Extrude097  label="Txt060"
  Base = -> ShapeString087
  Dir = (0,0,1)
  DirMode = 2
  FaceMakerClass = Part::FaceMakerBullseye
  LengthFwd = 1
  LengthRev = 0
  Solid = true
  Symmetric = false
FEATURE [App::DocumentObjectGroupPython] FPSimLED034  label="LedSel[3]"  # scripted group (container) (typed FeaturePython)
  Group = -> [Fusion007,Extrude097]
FEATURE [Part::Part2DObjectPython] ShapeString088  # Draft 2D object (typed FeaturePython)
  FontFile = <path>
  Placement = pos=(1,13,0) rot=(0,0,1;0rad)
  Size = 3
  String = 1/16
  Tracking = 0
FEATURE [Part::Extrusion] Extrude098  label="Txt061"
  Base = -> ShapeString088
  Dir = (0,0,1)
  DirMode = 2
  FaceMakerClass = Part::FaceMakerBullseye
  LengthFwd = 2
  LengthRev = 1
  Solid = true
  Symmetric = false
FEATURE [Part::Cut] Cut081
  Base = -> Cut004
  Tool = -> Extrude098
FEATURE [App::DocumentObjectGroupPython] FPSimButton044  label="BtnSel[3]"  # scripted group (container) (typed FeaturePython)
  Group = -> [FPSimLED034,Cut081]
  PressureResolutionAng = (0,0,0)
  PressureResolutionLin = (0,0,0)
  RotationAngle = 0
  RotationAxis = (0,0,0)
  RotationCenter = (0,0,0)
  SwitchMode = false
  Translation = (0,0,-1)
FEATURE [App::Part] Part058  label="FrBtnSel[3]"
  Group = -> [Box060,FPSimButton044,Box062,Box063,Fusion006,Cut004,Box061,Fusion007,Box064,FPSimLED034,ShapeString087,Extrude097,ShapeString088,Extrude098,Cut081]
  License = CC BY 3.0
  LicenseURL = http://creativecommons.org/licenses/by/3.0/
  Origin = -> Origin058
  Placement = pos=(120,-53,0) rot=(0,0,1;0rad)
FEATURE [Part::Part2DObjectPython] ShapeString089  # Draft 2D object (typed FeaturePython)
  FontFile = <path>
  Placement = pos=(1,13,0) rot=(0,0,1;0rad)
  Size = 3
  String = 1/8t
  Tracking = 0
FEATURE [Part::Extrusion] Extrude099  label="Txt062"
  Base = -> ShapeString089
  Dir = (0,0,1)
  DirMode = 2
  FaceMakerClass = Part::FaceMakerBullseye
  LengthFwd = 1
  LengthRev = 0
  Solid = true
  Symmetric = false
FEATURE [App::DocumentObjectGroupPython] FPSimLED035  label="LedSel[4]"  # scripted group (container) (typed FeaturePython)
  Group = -> [Fusion009,Extrude099]
FEATURE [Part::Part2DObjectPython] ShapeString090  # Draft 2D object (typed FeaturePython)
  FontFile = <path>
  Placement = pos=(1,13,0) rot=(0,0,1;0rad)
  Size = 3
  String = 1/8t
  Tracking = 0
FEATURE [Part::Extrusion] Extrude100  label="Txt063"
  Base = -> ShapeString090
  Dir = (0,0,1)
  DirMode = 2
  FaceMakerClass = Part::FaceMakerBullseye
  LengthFwd = 2
  LengthRev = 1
  Solid = true
  Symmetric = false
FEATURE [Part::Cut] Cut082
  Base = -> Cut005
  Tool = -> Extrude100
FEATURE [App::DocumentObjectGroupPython] FPSimButton045  label="BtnSel[4]"  # scripted group (container) (typed FeaturePython)
  Group = -> [FPSimLED035,Cut082]
  PressureResolutionAng = (0,0,0)
  PressureResolutionLin = (0,0,0)
  RotationAngle = 0
  RotationAxis = (0,0,0)
  RotationCenter = (0,0,0)
  SwitchMode = false
  Translation = (0,0,-1)
FEATURE [App::Part] Part059  label="FrBtnSel[4]"
  Group = -> [Box065,FPSimButton045,Box067,Box068,Fusion008,Cut005,Box066,Fusion009,Box069,FPSimLED035,ShapeString089,Extrude099,ShapeString090,Extrude100,Cut082]
  License = CC BY 3.0
  LicenseURL = http://creativecommons.org/licenses/by/3.0/
  Origin = -> Origin059
  Placement = pos=(120,-75,0) rot=(0,0,1;0rad)
FEATURE [Part::Part2DObjectPython] ShapeString091  # Draft 2D object (typed FeaturePython)
  FontFile = <path>
  Placement = pos=(1,13,0) rot=(0,0,1;0rad)
  Size = 3
  String = 1/8
  Tracking = 0
FEATURE [Part::Extrusion] Extrude101  label="Txt064"
  Base = -> ShapeString091
  Dir = (0,0,1)
  DirMode = 2
  FaceMakerClass = Part::FaceMakerBullseye
  LengthFwd = 1
  LengthRev = 0
  Solid = true
  Symmetric = false
FEATURE [App::DocumentObjectGroupPython] FPSimLED036  label="LedSel[5]"  # scripted group (container) (typed FeaturePython)
  Group = -> [Fusion011,Extrude101]
FEATURE [Part::Part2DObjectPython] ShapeString092  # Draft 2D object (typed FeaturePython)
  FontFile = <path>
  Placement = pos=(1,13,0) rot=(0,0,1;0rad)
  Size = 3
  String = 1/8
  Tracking = 0
FEATURE [Part::Extrusion] Extrude102  label="Txt065"
  Base = -> ShapeString092
  Dir = (0,0,1)
  DirMode = 2
  FaceMakerClass = Part::FaceMakerBullseye
  LengthFwd = 2
  LengthRev = 1
  Solid = true
  Symmetric = false
FEATURE [Part::Cut] Cut083
  Base = -> Cut006
  Tool = -> Extrude102
FEATURE [App::DocumentObjectGroupPython] FPSimButton046  label="BtnSel[5]"  # scripted group (container) (typed FeaturePython)
  Group = -> [FPSimLED036,Cut083]
  PressureResolutionAng = (0,0,0)
  PressureResolutionLin = (0,0,0)
  RotationAngle = 0
  RotationAxis = (0,0,0)
  RotationCenter = (0,0,0)
  SwitchMode = false
  Translation = (0,0,-1)
FEATURE [App::Part] Part060  label="FrBtnSel[5]"
  Group = -> [Box070,FPSimButton046,Box072,Box073,Fusion010,Cut006,Box071,Fusion011,Box074,FPSimLED036,ShapeString091,Extrude101,ShapeString092,Extrude102,Cut083]
  License = CC BY 3.0
  LicenseURL = http://creativecommons.org/licenses/by/3.0/
  Origin = -> Origin060
  Placement = pos=(120,-97,0) rot=(0,0,1;0rad)
FEATURE [Part::Part2DObjectPython] ShapeString093  # Draft 2D object (typed FeaturePython)
  FontFile = <path>
  Placement = pos=(1,13,0) rot=(0,0,1;0rad)
  Size = 3
  String = 1/4t
  Tracking = 0
FEATURE [Part::Extrusion] Extrude103  label="Txt066"
  Base = -> ShapeString093
  Dir = (0,0,1)
  DirMode = 2
  FaceMakerClass = Part::FaceMakerBullseye
  LengthFwd = 1
  LengthRev = 0
  Solid = true
  Symmetric = false
FEATURE [App::DocumentObjectGroupPython] FPSimLED037  label="LedSel[6]"  # scripted group (container) (typed FeaturePython)
  Group = -> [Fusion013,Extrude103]
FEATURE [Part::Part2DObjectPython] ShapeString094  # Draft 2D object (typed FeaturePython)
  FontFile = <path>
  Placement = pos=(1,13,0) rot=(0,0,1;0rad)
  Size = 3
  String = 1/4t
  Tracking = 0
FEATURE [Part::Extrusion] Extrude104  label="Txt067"
  Base = -> ShapeString094
  Dir = (0,0,1)
  DirMode = 2
  FaceMakerClass = Part::FaceMakerBullseye
  LengthFwd = 2
  LengthRev = 1
  Solid = true
  Symmetric = false
FEATURE [Part::Cut] Cut084
  Base = -> Cut007
  Tool = -> Extrude104
FEATURE [App::DocumentObjectGroupPython] FPSimButton047  label="BtnSel[6]"  # scripted group (container) (typed FeaturePython)
  Group = -> [FPSimLED037,Cut084]
  PressureResolutionAng = (0,0,0)
  PressureResolutionLin = (0,0,0)
  RotationAngle = 0
  RotationAxis = (0,0,0)
  RotationCenter = (0,0,0)
  SwitchMode = false
  Translation = (0,0,-1)
FEATURE [App::Part] Part061  label="FrBtnSel[6]"
  Group = -> [Box075,FPSimButton047,Box077,Box078,Fusion012,Cut007,Box076,Fusion013,Box079,FPSimLED037,ShapeString093,Extrude103,ShapeString094,Extrude104,Cut084]
  License = CC BY 3.0
  LicenseURL = http://creativecommons.org/licenses/by/3.0/
  Origin = -> Origin061
  Placement = pos=(120,-119,0) rot=(0,0,1;0rad)
FEATURE [Part::Part2DObjectPython] ShapeString095  # Draft 2D object (typed FeaturePython)
  FontFile = <path>
  Placement = pos=(1,13,0) rot=(0,0,1;0rad)
  Size = 3
  String = 1/4
  Tracking = 0
FEATURE [Part::Extrusion] Extrude105  label="Txt068"
  Base = -> ShapeString095
  Dir = (0,0,1)
  DirMode = 2
  FaceMakerClass = Part::FaceMakerBullseye
  LengthFwd = 1
  LengthRev = 0
  Solid = true
  Symmetric = false
FEATURE [App::DocumentObjectGroupPython] FPSimLED038  label="LedSel[7]"  # scripted group (container) (typed FeaturePython)
  Group = -> [Fusion015,Extrude105]
FEATURE [Part::Part2DObjectPython] ShapeString096  # Draft 2D object (typed FeaturePython)
  FontFile = <path>
  Placement = pos=(1,13,0) rot=(0,0,1;0rad)
  Size = 3
  String = 1/4
  Tracking = 0
FEATURE [Part::Extrusion] Extrude106  label="Txt069"
  Base = -> ShapeString096
  Dir = (0,0,1)
  DirMode = 2
  FaceMakerClass = Part::FaceMakerBullseye
  LengthFwd = 2
  LengthRev = 1
  Solid = true
  Symmetric = false
FEATURE [Part::Cut] Cut085
  Base = -> Cut008
  Tool = -> Extrude106
FEATURE [App::DocumentObjectGroupPython] FPSimButton048  label="BtnSel[7]"  # scripted group (container) (typed FeaturePython)
  Group = -> [FPSimLED038,Cut085]
  PressureResolutionAng = (0,0,0)
  PressureResolutionLin = (0,0,0)
  RotationAngle = 0
  RotationAxis = (0,0,0)
  RotationCenter = (0,0,0)
  SwitchMode = false
  Translation = (0,0,-1)
FEATURE [App::Part] Part062  label="FrBtnSel[7]"
  Group = -> [Box080,FPSimButton048,Box082,Box083,Fusion014,Cut008,Box081,Fusion015,Box084,FPSimLED038,ShapeString095,Extrude105,ShapeString096,Extrude106,Cut085]
  License = CC BY 3.0
  LicenseURL = http://creativecommons.org/licenses/by/3.0/
  Origin = -> Origin062
  Placement = pos=(120,-141,0) rot=(0,0,1;0rad)
FEATURE [App::DocumentObjectGroup] Group007  label="Right"
  Group = -> [Part054,Part055,Part056,Part057,Part058,Part059,Part060,Part061,Part062,Part067,Part075,Part076,Part077,Part078,Part079,Part080,Part069,Part073,Part074]
FEATURE [App::DocumentObjectGroupPython] FPSimLED161  label="BtnSilLed[0][0]"  # scripted group (container) (typed FeaturePython)
  Group = -> [Fillet]
  Unenlightened_Blue = 120
  Unenlightened_Green = 120
  Unenlightened_Red = 120
FEATURE [App::DocumentObjectGroupPython] FPSimButton129  label="BtnSil[0][0]"  # scripted group (container) (typed FeaturePython)
  Group = -> [FPSimLED161]
  PressureResolutionAng = (0,0,0)
  PressureResolutionLin = (0,0,128)
  RotationAngle = 0
  RotationAxis = (0,0,0)
  RotationCenter = (0,0,0)
  SwitchMode = false
  Translation = (0,0,-1)
  VelocityResolution = 128
FEATURE [App::Part] Part081  label="FrBtnSil[0][0]"
  Group = -> [FPSimButton129,Fillet,Box178,FPSimLED161]
  License = CC BY 3.0
  LicenseURL = http://creativecommons.org/licenses/by/3.0/
  Origin = -> Origin081
  Placement = pos=(-119,13,0) rot=(0,0,1;0rad)
FEATURE [Part::Box] Box262  label="Cube230"
  AttacherType = Attacher::AttachEngine3D
  Height = 1
  Length = 25
  Width = 18.5
FEATURE [Part::Fillet] Fillet064
  Base = -> Box262
  Edges = 8 edges r=0.2: [Edge1,Edge2,Edge3,Edge5,Edge6,Edge7,Edge10,Edge12]
FEATURE [App::DocumentObjectGroupPython] FPSimLED162  label="BtnSilLed[1][0]"  # scripted group (container) (typed FeaturePython)
  Group = -> [Fillet064]
  Unenlightened_Blue = 120
  Unenlightened_Green = 120
  Unenlightened_Red = 120
FEATURE [App::DocumentObjectGroupPython] FPSimButton066  label="BtnSil[1][0]"  # scripted group (container) (typed FeaturePython)
  Group = -> [FPSimLED162]
  PressureResolutionAng = (0,0,0)
  PressureResolutionLin = (0,0,0)
  RotationAngle = 0
  RotationAxis = (0,0,0)
  RotationCenter = (0,0,0)
  SwitchMode = false
  Translation = (0,0,-1)
FEATURE [App::Part] Part082  label="FrBtnSil[1][0]"
  Group = -> [Box179,FPSimButton066,Box262,Fillet064,FPSimLED162]
  License = CC BY 3.0
  LicenseURL = http://creativecommons.org/licenses/by/3.0/
  Origin = -> Origin082
  Placement = pos=(-90,13,0) rot=(0,0,1;0rad)
FEATURE [Part::Box] Box263  label="Cube231"
  AttacherType = Attacher::AttachEngine3D
  Height = 1
  Length = 25
  Width = 18.5
FEATURE [Part::Fillet] Fillet065
  Base = -> Box263
  Edges = 8 edges r=0.2: [Edge1,Edge2,Edge3,Edge5,Edge6,Edge7,Edge10,Edge12]
FEATURE [App::DocumentObjectGroupPython] FPSimLED163  label="BtnSilLed[2][0]"  # scripted group (container) (typed FeaturePython)
  Group = -> [Fillet065]
  Unenlightened_Blue = 120
  Unenlightened_Green = 120
  Unenlightened_Red = 120
FEATURE [App::DocumentObjectGroupPython] FPSimButton067  label="BtnSil[2][0]"  # scripted group (container) (typed FeaturePython)
  Group = -> [FPSimLED163]
  PressureResolutionAng = (0,0,0)
  PressureResolutionLin = (0,0,0)
  RotationAngle = 0
  RotationAxis = (0,0,0)
  RotationCenter = (0,0,0)
  SwitchMode = false
  Translation = (0,0,-1)
FEATURE [App::Part] Part083  label="FrBtnSil[2][0]"
  Group = -> [Box180,FPSimButton067,Box263,Fillet065,FPSimLED163]
  License = CC BY 3.0
  LicenseURL = http://creativecommons.org/licenses/by/3.0/
  Origin = -> Origin083
  Placement = pos=(-61,13,0) rot=(0,0,1;0rad)
FEATURE [Part::Box] Box264  label="Cube232"
  AttacherType = Attacher::AttachEngine3D
  Height = 1
  Length = 25
  Width = 18.5
FEATURE [Part::Fillet] Fillet066
  Base = -> Box264
  Edges = 8 edges r=0.2: [Edge1,Edge2,Edge3,Edge5,Edge6,Edge7,Edge10,Edge12]
FEATURE [App::DocumentObjectGroupPython] FPSimLED164  label="BtnSilLed[3][0]"  # scripted group (container) (typed FeaturePython)
  Group = -> [Fillet066]
  Unenlightened_Blue = 120
  Unenlightened_Green = 120
  Unenlightened_Red = 120
FEATURE [App::DocumentObjectGroupPython] FPSimButton068  label="BtnSil[3][0]"  # scripted group (container) (typed FeaturePython)
  Group = -> [FPSimLED164]
  PressureResolutionAng = (0,0,0)
  PressureResolutionLin = (0,0,0)
  RotationAngle = 0
  RotationAxis = (0,0,0)
  RotationCenter = (0,0,0)
  SwitchMode = false
  Translation = (0,0,-1)
FEATURE [App::Part] Part084  label="FrBtnSil[3][0]"
  Group = -> [Box181,FPSimButton068,Box264,Fillet066,FPSimLED164]
  License = CC BY 3.0
  LicenseURL = http://creativecommons.org/licenses/by/3.0/
  Origin = -> Origin084
  Placement = pos=(-32,13,0) rot=(0,0,1;0rad)
FEATURE [Part::Box] Box265  label="Cube233"
  AttacherType = Attacher::AttachEngine3D
  Height = 1
  Length = 25
  Width = 18.5
FEATURE [Part::Fillet] Fillet067
  Base = -> Box265
  Edges = 8 edges r=0.2: [Edge1,Edge2,Edge3,Edge5,Edge6,Edge7,Edge10,Edge12]
FEATURE [App::DocumentObjectGroupPython] FPSimLED165  label="BtnSilLed[4][0]"  # scripted group (container) (typed FeaturePython)
  Group = -> [Fillet067]
  Unenlightened_Blue = 120
  Unenlightened_Green = 120
  Unenlightened_Red = 120
FEATURE [App::DocumentObjectGroupPython] FPSimButton069  label="BtnSil[4][0]"  # scripted group (container) (typed FeaturePython)
  Group = -> [FPSimLED165]
  PressureResolutionAng = (0,0,0)
  PressureResolutionLin = (0,0,0)
  RotationAngle = 0
  RotationAxis = (0,0,0)
  RotationCenter = (0,0,0)
  SwitchMode = false
  Translation = (0,0,-1)
FEATURE [App::Part] Part085  label="FrBtnSil[4][0]"
  Group = -> [Box182,FPSimButton069,Fillet067,Box265,FPSimLED165]
  License = CC BY 3.0
  LicenseURL = http://creativecommons.org/licenses/by/3.0/
  Origin = -> Origin085
  Placement = pos=(-3,13,0) rot=(0,0,1;0rad)
FEATURE [Part::Box] Box266  label="Cube234"
  AttacherType = Attacher::AttachEngine3D
  Height = 1
  Length = 25
  Width = 18.5
FEATURE [Part::Fillet] Fillet068
  Base = -> Box266
  Edges = 8 edges r=0.2: [Edge1,Edge2,Edge3,Edge5,Edge6,Edge7,Edge10,Edge12]
FEATURE [App::DocumentObjectGroupPython] FPSimLED166  label="BtnSilLed[5][0]"  # scripted group (container) (typed FeaturePython)
  Group = -> [Fillet068]
  Unenlightened_Blue = 120
  Unenlightened_Green = 120
  Unenlightened_Red = 120
FEATURE [App::DocumentObjectGroupPython] FPSimButton070  label="BtnSil[5][0]"  # scripted group (container) (typed FeaturePython)
  Group = -> [FPSimLED166]
  PressureResolutionAng = (0,0,0)
  PressureResolutionLin = (0,0,0)
  RotationAngle = 0
  RotationAxis = (0,0,0)
  RotationCenter = (0,0,0)
  SwitchMode = false
  Translation = (0,0,-1)
FEATURE [App::Part] Part086  label="FrBtnSil[5][0]"
  Group = -> [Box183,FPSimButton070,Box266,Fillet068,FPSimLED166]
  License = CC BY 3.0
  LicenseURL = http://creativecommons.org/licenses/by/3.0/
  Origin = -> Origin086
  Placement = pos=(26,13,0) rot=(0,0,1;0rad)
FEATURE [Part::Box] Box267  label="Cube235"
  AttacherType = Attacher::AttachEngine3D
  Height = 1
  Length = 25
  Width = 18.5
FEATURE [Part::Box] Box268  label="Cube236"
  AttacherType = Attacher::AttachEngine3D
  Height = 1
  Length = 25
  Width = 18.5
FEATURE [Part::Fillet] Fillet070
  Base = -> Box268
  Edges = 8 edges r=0.2: [Edge1,Edge2,Edge3,Edge5,Edge6,Edge7,Edge10,Edge12]
FEATURE [App::DocumentObjectGroupPython] FPSimLED168  label="BtnSilLed[7][0]"  # scripted group (container) (typed FeaturePython)
  Group = -> [Fillet070]
  Unenlightened_Blue = 120
  Unenlightened_Green = 120
  Unenlightened_Red = 120
FEATURE [App::DocumentObjectGroupPython] FPSimButton072  label="BtnSil[7][0]"  # scripted group (container) (typed FeaturePython)
  Group = -> [FPSimLED168]
  PressureResolutionAng = (0,0,0)
  PressureResolutionLin = (0,0,0)
  RotationAngle = 0
  RotationAxis = (0,0,0)
  RotationCenter = (0,0,0)
  SwitchMode = false
  Translation = (0,0,-1)
FEATURE [App::Part] Part088  label="FrBtnSil[7][0]"
  Group = -> [Box185,FPSimButton072,Box268,Fillet070,FPSimLED168]
  License = CC BY 3.0
  LicenseURL = http://creativecommons.org/licenses/by/3.0/
  Origin = -> Origin088
  Placement = pos=(84,13,0) rot=(0,0,1;0rad)
FEATURE [Part::Box] Box269  label="Cube237"
  AttacherType = Attacher::AttachEngine3D
  Height = 1
  Length = 25
  Width = 18.5
FEATURE [Part::Fillet] Fillet071
  Base = -> Box269
  Edges = 8 edges r=0.2: [Edge1,Edge2,Edge3,Edge5,Edge6,Edge7,Edge10,Edge12]
FEATURE [App::DocumentObjectGroupPython] FPSimLED169  label="BtnSilLed[6][0]"  # scripted group (container) (typed FeaturePython)
  Group = -> [Fillet071]
  Unenlightened_Blue = 120
  Unenlightened_Green = 120
  Unenlightened_Red = 120
FEATURE [App::DocumentObjectGroupPython] FPSimButton071  label="BtnSil[6][0]"  # scripted group (container) (typed FeaturePython)
  Group = -> [FPSimLED169]
  PressureResolutionAng = (0,0,0)
  PressureResolutionLin = (0,0,0)
  RotationAngle = 0
  RotationAxis = (0,0,0)
  RotationCenter = (0,0,0)
  SwitchMode = false
  Translation = (0,0,-1)
FEATURE [App::Part] Part087  label="FrBtnSil[6][0]"
  Group = -> [Box184,FPSimButton071,Box267,Fillet071,Box269,FPSimLED169]
  License = CC BY 3.0
  LicenseURL = http://creativecommons.org/licenses/by/3.0/
  Origin = -> Origin087
  Placement = pos=(55,13,0) rot=(0,0,1;0rad)
FEATURE [App::Part] Part089  label="FrBtnSilRow000"
  Group = -> [Part082,Part083,Part084,Part085,Part086,Part087,Part088,Part081]
  License = CC BY 3.0
  LicenseURL = http://creativecommons.org/licenses/by/3.0/
  Origin = -> Origin089
FEATURE [Part::Box] Box270  label="Cube238"
  AttacherType = Attacher::AttachEngine3D
  Height = 1
  Length = 25
  Width = 18.5
FEATURE [Part::Fillet] Fillet072
  Base = -> Box270
  Edges = 8 edges r=0.2: [Edge1,Edge2,Edge3,Edge5,Edge6,Edge7,Edge10,Edge12]
FEATURE [App::DocumentObjectGroupPython] FPSimLED170  label="BtnSilLed[0][1]"  # scripted group (container) (typed FeaturePython)
  Group = -> [Fillet072]
  Unenlightened_Blue = 120
  Unenlightened_Green = 120
  Unenlightened_Red = 120
FEATURE [App::DocumentObjectGroupPython] FPSimButton076  label="BtnSil[0][1]"  # scripted group (container) (typed FeaturePython)
  Group = -> [FPSimLED170]
  PressureResolutionAng = (0,0,0)
  PressureResolutionLin = (0,0,0)
  RotationAngle = 0
  RotationAxis = (0,0,0)
  RotationCenter = (0,0,0)
  SwitchMode = false
  Translation = (0,0,-1)
FEATURE [App::Part] Part097  label="FrBtnSil[0][1]"
  Group = -> [Box189,FPSimButton076,Fillet072,Box270,FPSimLED170]
  License = CC BY 3.0
  LicenseURL = http://creativecommons.org/licenses/by/3.0/
  Origin = -> Origin094
  Placement = pos=(-119,13,0) rot=(0,0,1;0rad)
FEATURE [Part::Box] Box271  label="Cube239"
  AttacherType = Attacher::AttachEngine3D
  Height = 1
  Length = 25
  Width = 18.5
FEATURE [Part::Fillet] Fillet073
  Base = -> Box271
  Edges = 8 edges r=0.2: [Edge1,Edge2,Edge3,Edge5,Edge6,Edge7,Edge10,Edge12]
FEATURE [App::DocumentObjectGroupPython] FPSimLED171  label="BtnSilLed[1][1]"  # scripted group (container) (typed FeaturePython)
  Group = -> [Fillet073]
  Unenlightened_Blue = 120
  Unenlightened_Green = 120
  Unenlightened_Red = 120
FEATURE [App::DocumentObjectGroupPython] FPSimButton075  label="BtnSil[1][1]"  # scripted group (container) (typed FeaturePython)
  Group = -> [FPSimLED171]
  PressureResolutionAng = (0,0,0)
  PressureResolutionLin = (0,0,0)
  RotationAngle = 0
  RotationAxis = (0,0,0)
  RotationCenter = (0,0,0)
  SwitchMode = false
  Translation = (0,0,-1)
FEATURE [App::Part] Part098  label="FrBtnSil[1][1]"
  Group = -> [Box186,FPSimButton075,Box271,Fillet073,FPSimLED171]
  License = CC BY 3.0
  LicenseURL = http://creativecommons.org/licenses/by/3.0/
  Origin = -> Origin090
  Placement = pos=(-90,13,0) rot=(0,0,1;0rad)
FEATURE [Part::Box] Box272  label="Cube240"
  AttacherType = Attacher::AttachEngine3D
  Height = 1
  Length = 25
  Width = 18.5
FEATURE [Part::Fillet] Fillet074
  Base = -> Box272
  Edges = 8 edges r=0.2: [Edge1,Edge2,Edge3,Edge5,Edge6,Edge7,Edge10,Edge12]
FEATURE [App::DocumentObjectGroupPython] FPSimLED172  label="BtnSilLed[2][1]"  # scripted group (container) (typed FeaturePython)
  Group = -> [Fillet074]
  Unenlightened_Blue = 120
  Unenlightened_Green = 120
  Unenlightened_Red = 120
FEATURE [App::DocumentObjectGroupPython] FPSimButton073  label="BtnSil[2][1]"  # scripted group (container) (typed FeaturePython)
  Group = -> [FPSimLED172]
  PressureResolutionAng = (0,0,0)
  PressureResolutionLin = (0,0,0)
  RotationAngle = 0
  RotationAxis = (0,0,0)
  RotationCenter = (0,0,0)
  SwitchMode = false
  Translation = (0,0,-1)
FEATURE [App::Part] Part090  label="FrBtnSil[2][1]"
  Group = -> [Box187,FPSimButton073,Box272,Fillet074,FPSimLED172]
  License = CC BY 3.0
  LicenseURL = http://creativecommons.org/licenses/by/3.0/
  Origin = -> Origin091
  Placement = pos=(-61,13,0) rot=(0,0,1;0rad)
FEATURE [Part::Box] Box273  label="Cube241"
  AttacherType = Attacher::AttachEngine3D
  Height = 1
  Length = 25
  Width = 18.5
FEATURE [Part::Fillet] Fillet075
  Base = -> Box273
  Edges = 8 edges r=0.2: [Edge1,Edge2,Edge3,Edge5,Edge6,Edge7,Edge10,Edge12]
FEATURE [App::DocumentObjectGroupPython] FPSimLED173  label="BtnSilLed[3][1]"  # scripted group (container) (typed FeaturePython)
  Group = -> [Fillet075]
  Unenlightened_Blue = 120
  Unenlightened_Green = 120
  Unenlightened_Red = 120
FEATURE [App::DocumentObjectGroupPython] FPSimButton074  label="BtnSil[3][1]"  # scripted group (container) (typed FeaturePython)
  Group = -> [FPSimLED173]
  PressureResolutionAng = (0,0,0)
  PressureResolutionLin = (0,0,0)
  RotationAngle = 0
  RotationAxis = (0,0,0)
  RotationCenter = (0,0,0)
  SwitchMode = false
  Translation = (0,0,-1)
FEATURE [App::Part] Part091  label="FrBtnSil[3][1]"
  Group = -> [Box190,FPSimButton074,Fillet075,Box273,FPSimLED173]
  License = CC BY 3.0
  LicenseURL = http://creativecommons.org/licenses/by/3.0/
  Origin = -> Origin095
  Placement = pos=(-32,13,0) rot=(0,0,1;0rad)
FEATURE [Part::Box] Box274  label="Cube242"
  AttacherType = Attacher::AttachEngine3D
  Height = 1
  Length = 25
  Width = 18.5
FEATURE [Part::Fillet] Fillet076
  Base = -> Box274
  Edges = 8 edges r=0.2: [Edge1,Edge2,Edge3,Edge5,Edge6,Edge7,Edge10,Edge12]
FEATURE [App::DocumentObjectGroupPython] FPSimLED174  label="BtnSilLed[4][1]"  # scripted group (container) (typed FeaturePython)
  Group = -> [Fillet076]
  Unenlightened_Blue = 120
  Unenlightened_Green = 120
  Unenlightened_Red = 120
FEATURE [App::DocumentObjectGroupPython] FPSimButton079  label="BtnSil[4][1]"  # scripted group (container) (typed FeaturePython)
  Group = -> [FPSimLED174]
  PressureResolutionAng = (0,0,0)
  PressureResolutionLin = (0,0,0)
  RotationAngle = 0
  RotationAxis = (0,0,0)
  RotationCenter = (0,0,0)
  SwitchMode = false
  Translation = (0,0,-1)
FEATURE [App::Part] Part092  label="FrBtnSil[4][1]"
  Group = -> [Box188,FPSimButton079,Fillet076,Box274,FPSimLED174]
  License = CC BY 3.0
  LicenseURL = http://creativecommons.org/licenses/by/3.0/
  Origin = -> Origin096
  Placement = pos=(-3,13,0) rot=(0,0,1;0rad)
FEATURE [Part::Box] Box275  label="Cube243"
  AttacherType = Attacher::AttachEngine3D
  Height = 1
  Length = 25
  Width = 18.5
FEATURE [Part::Fillet] Fillet077
  Base = -> Box275
  Edges = 8 edges r=0.2: [Edge1,Edge2,Edge3,Edge5,Edge6,Edge7,Edge10,Edge12]
FEATURE [App::DocumentObjectGroupPython] FPSimLED175  label="BtnSilLed[5][1]"  # scripted group (container) (typed FeaturePython)
  Group = -> [Fillet077]
  Unenlightened_Blue = 120
  Unenlightened_Green = 120
  Unenlightened_Red = 120
FEATURE [App::DocumentObjectGroupPython] FPSimButton078  label="BtnSil[5][1]"  # scripted group (container) (typed FeaturePython)
  Group = -> [FPSimLED175]
  PressureResolutionAng = (0,0,0)
  PressureResolutionLin = (0,0,0)
  RotationAngle = 0
  RotationAxis = (0,0,0)
  RotationCenter = (0,0,0)
  SwitchMode = false
  Translation = (0,0,-1)
FEATURE [App::Part] Part096  label="FrBtnSil[5][1]"
  Group = -> [Box192,FPSimButton078,Fillet077,Box275,FPSimLED175]
  License = CC BY 3.0
  LicenseURL = http://creativecommons.org/licenses/by/3.0/
  Origin = -> Origin092
  Placement = pos=(26,13,0) rot=(0,0,1;0rad)
FEATURE [Part::Box] Box276  label="Cube244"
  AttacherType = Attacher::AttachEngine3D
  Height = 1
  Length = 25
  Width = 18.5
FEATURE [Part::Fillet] Fillet078
  Base = -> Box276
  Edges = 8 edges r=0.2: [Edge1,Edge2,Edge3,Edge5,Edge6,Edge7,Edge10,Edge12]
FEATURE [App::DocumentObjectGroupPython] FPSimLED176  label="BtnSilLed[6][1]"  # scripted group (container) (typed FeaturePython)
  Group = -> [Fillet078]
  Unenlightened_Blue = 120
  Unenlightened_Green = 120
  Unenlightened_Red = 120
FEATURE [App::DocumentObjectGroupPython] FPSimButton077  label="BtnSil[6][1]"  # scripted group (container) (typed FeaturePython)
  Group = -> [FPSimLED176]
  PressureResolutionAng = (0,0,0)
  PressureResolutionLin = (0,0,0)
  RotationAngle = 0
  RotationAxis = (0,0,0)
  RotationCenter = (0,0,0)
  SwitchMode = false
  Translation = (0,0,-1)
FEATURE [App::Part] Part094  label="FrBtnSil[6][1]"
  Group = -> [Box193,FPSimButton077,Fillet078,Box276,FPSimLED176]
  License = CC BY 3.0
  LicenseURL = http://creativecommons.org/licenses/by/3.0/
  Origin = -> Origin093
  Placement = pos=(55,13,0) rot=(0,0,1;0rad)
FEATURE [Part::Box] Box277  label="Cube245"
  AttacherType = Attacher::AttachEngine3D
  Height = 1
  Length = 25
  Width = 18.5
FEATURE [Part::Fillet] Fillet079
  Base = -> Box277
  Edges = 8 edges r=0.2: [Edge1,Edge2,Edge3,Edge5,Edge6,Edge7,Edge10,Edge12]
FEATURE [App::DocumentObjectGroupPython] FPSimLED177  label="BtnSilLed[7][1]"  # scripted group (container) (typed FeaturePython)
  Group = -> [Fillet079]
  Unenlightened_Blue = 120
  Unenlightened_Green = 120
  Unenlightened_Red = 120
FEATURE [App::DocumentObjectGroupPython] FPSimButton080  label="BtnSil[7][1]"  # scripted group (container) (typed FeaturePython)
  Group = -> [FPSimLED177]
  PressureResolutionAng = (0,0,0)
  PressureResolutionLin = (0,0,0)
  RotationAngle = 0
  RotationAxis = (0,0,0)
  RotationCenter = (0,0,0)
  SwitchMode = false
  Translation = (0,0,-1)
FEATURE [App::Part] Part095  label="FrBtnSil[7][1]"
  Group = -> [Box191,FPSimButton080,Box277,Fillet079,FPSimLED177]
  License = CC BY 3.0
  LicenseURL = http://creativecommons.org/licenses/by/3.0/
  Origin = -> Origin097
  Placement = pos=(84,13,0) rot=(0,0,1;0rad)
FEATURE [App::Part] Part093  label="FrBtnSilRow001"
  Group = -> [Part097,Part098,Part090,Part091,Part092,Part096,Part094,Part095]
  License = CC BY 3.0
  LicenseURL = http://creativecommons.org/licenses/by/3.0/
  Origin = -> Origin098
  Placement = pos=(0,-22,0) rot=(0,0,1;0rad)
FEATURE [Part::Box] Box278  label="Cube246"
  AttacherType = Attacher::AttachEngine3D
  Height = 1
  Length = 25
  Width = 18.5
FEATURE [Part::Fillet] Fillet080
  Base = -> Box278
  Edges = 8 edges r=0.2: [Edge1,Edge2,Edge3,Edge5,Edge6,Edge7,Edge10,Edge12]
FEATURE [App::DocumentObjectGroupPython] FPSimLED178  label="BtnSilLed[0][2]"  # scripted group (container) (typed FeaturePython)
  Group = -> [Fillet080]
  Unenlightened_Blue = 120
  Unenlightened_Green = 120
  Unenlightened_Red = 120
FEATURE [App::DocumentObjectGroupPython] FPSimButton088  label="BtnSil[0][2]"  # scripted group (container) (typed FeaturePython)
  Group = -> [FPSimLED178]
  PressureResolutionAng = (0,0,0)
  PressureResolutionLin = (0,0,0)
  RotationAngle = 0
  RotationAxis = (0,0,0)
  RotationCenter = (0,0,0)
  SwitchMode = false
  Translation = (0,0,-1)
FEATURE [App::Part] Part106  label="FrBtnSil[0][2]"
  Group = -> [Box196,FPSimButton088,Box278,Fillet080,FPSimLED178]
  License = CC BY 3.0
  LicenseURL = http://creativecommons.org/licenses/by/3.0/
  Origin = -> Origin106
  Placement = pos=(-119,13,0) rot=(0,0,1;0rad)
FEATURE [Part::Box] Box279  label="Cube247"
  AttacherType = Attacher::AttachEngine3D
  Height = 1
  Length = 25
  Width = 18.5
FEATURE [Part::Fillet] Fillet081
  Base = -> Box279
  Edges = 8 edges r=0.2: [Edge1,Edge2,Edge3,Edge5,Edge6,Edge7,Edge10,Edge12]
FEATURE [App::DocumentObjectGroupPython] FPSimLED179  label="BtnSilLed[1][2]"  # scripted group (container) (typed FeaturePython)
  Group = -> [Fillet081]
  Unenlightened_Blue = 120
  Unenlightened_Green = 120
  Unenlightened_Red = 120
FEATURE [App::DocumentObjectGroupPython] FPSimButton081  label="BtnSil[1][2]"  # scripted group (container) (typed FeaturePython)
  Group = -> [FPSimLED179]
  PressureResolutionAng = (0,0,0)
  PressureResolutionLin = (0,0,0)
  RotationAngle = 0
  RotationAxis = (0,0,0)
  RotationCenter = (0,0,0)
  SwitchMode = false
  Translation = (0,0,-1)
FEATURE [App::Part] Part107  label="FrBtnSil[1][2]"
  Group = -> [Box200,FPSimButton081,Fillet081,Box279,FPSimLED179]
  License = CC BY 3.0
  LicenseURL = http://creativecommons.org/licenses/by/3.0/
  Origin = -> Origin103
  Placement = pos=(-90,13,0) rot=(0,0,1;0rad)
FEATURE [Part::Box] Box280  label="Cube248"
  AttacherType = Attacher::AttachEngine3D
  Height = 1
  Length = 25
  Width = 18.5
FEATURE [Part::Fillet] Fillet082
  Base = -> Box280
  Edges = 8 edges r=0.2: [Edge1,Edge2,Edge3,Edge5,Edge6,Edge7,Edge10,Edge12]
FEATURE [App::DocumentObjectGroupPython] FPSimLED180  label="BtnSilLed[2][2]"  # scripted group (container) (typed FeaturePython)
  Group = -> [Fillet082]
  Unenlightened_Blue = 120
  Unenlightened_Green = 120
  Unenlightened_Red = 120
FEATURE [App::DocumentObjectGroupPython] FPSimButton083  label="BtnSil[2][2]"  # scripted group (container) (typed FeaturePython)
  Group = -> [FPSimLED180]
  PressureResolutionAng = (0,0,0)
  PressureResolutionLin = (0,0,0)
  RotationAngle = 0
  RotationAxis = (0,0,0)
  RotationCenter = (0,0,0)
  SwitchMode = false
  Translation = (0,0,-1)
FEATURE [App::Part] Part099  label="FrBtnSil[2][2]"
  Group = -> [Box194,FPSimButton083,Fillet082,Box280,FPSimLED180]
  License = CC BY 3.0
  LicenseURL = http://creativecommons.org/licenses/by/3.0/
  Origin = -> Origin100
  Placement = pos=(-61,13,0) rot=(0,0,1;0rad)
FEATURE [Part::Box] Box281  label="Cube249"
  AttacherType = Attacher::AttachEngine3D
  Height = 1
  Length = 25
  Width = 18.5
FEATURE [Part::Fillet] Fillet083
  Base = -> Box281
  Edges = 8 edges r=0.2: [Edge1,Edge2,Edge3,Edge5,Edge6,Edge7,Edge10,Edge12]
FEATURE [App::DocumentObjectGroupPython] FPSimLED181  label="BtnSilLed[3][2]"  # scripted group (container) (typed FeaturePython)
  Group = -> [Fillet083]
  Unenlightened_Blue = 120
  Unenlightened_Green = 120
  Unenlightened_Red = 120
FEATURE [App::DocumentObjectGroupPython] FPSimButton085  label="BtnSil[3][2]"  # scripted group (container) (typed FeaturePython)
  Group = -> [FPSimLED181]
  PressureResolutionAng = (0,0,0)
  PressureResolutionLin = (0,0,0)
  RotationAngle = 0
  RotationAxis = (0,0,0)
  RotationCenter = (0,0,0)
  SwitchMode = false
  Translation = (0,0,-1)
FEATURE [App::Part] Part100  label="FrBtnSil[3][2]"
  Group = -> [Box198,FPSimButton085,Box281,Fillet083,FPSimLED181]
  License = CC BY 3.0
  LicenseURL = http://creativecommons.org/licenses/by/3.0/
  Origin = -> Origin104
  Placement = pos=(-32,13,0) rot=(0,0,1;0rad)
FEATURE [Part::Box] Box282  label="Cube250"
  AttacherType = Attacher::AttachEngine3D
  Height = 1
  Length = 25
  Width = 18.5
FEATURE [Part::Fillet] Fillet084
  Base = -> Box282
  Edges = 8 edges r=0.2: [Edge1,Edge2,Edge3,Edge5,Edge6,Edge7,Edge10,Edge12]
FEATURE [App::DocumentObjectGroupPython] FPSimLED182  label="BtnSilLed[4][2]"  # scripted group (container) (typed FeaturePython)
  Group = -> [Fillet084]
  Unenlightened_Blue = 120
  Unenlightened_Green = 120
  Unenlightened_Red = 120
FEATURE [App::DocumentObjectGroupPython] FPSimButton084  label="BtnSil[4][2]"  # scripted group (container) (typed FeaturePython)
  Group = -> [FPSimLED182]
  PressureResolutionAng = (0,0,0)
  PressureResolutionLin = (0,0,0)
  RotationAngle = 0
  RotationAxis = (0,0,0)
  RotationCenter = (0,0,0)
  SwitchMode = false
  Translation = (0,0,-1)
FEATURE [App::Part] Part101  label="FrBtnSil[4][2]"
  Group = -> [Box195,FPSimButton084,Fillet084,Box282,FPSimLED182]
  License = CC BY 3.0
  LicenseURL = http://creativecommons.org/licenses/by/3.0/
  Origin = -> Origin101
  Placement = pos=(-3,13,0) rot=(0,0,1;0rad)
FEATURE [Part::Box] Box283  label="Cube251"
  AttacherType = Attacher::AttachEngine3D
  Height = 1
  Length = 25
  Width = 18.5
FEATURE [Part::Fillet] Fillet085
  Base = -> Box283
  Edges = 8 edges r=0.2: [Edge1,Edge2,Edge3,Edge5,Edge6,Edge7,Edge10,Edge12]
FEATURE [App::DocumentObjectGroupPython] FPSimLED183  label="BtnSilLed[5][2]"  # scripted group (container) (typed FeaturePython)
  Group = -> [Fillet085]
  Unenlightened_Blue = 120
  Unenlightened_Green = 120
  Unenlightened_Red = 120
FEATURE [App::DocumentObjectGroupPython] FPSimButton082  label="BtnSil[5][2]"  # scripted group (container) (typed FeaturePython)
  Group = -> [FPSimLED183]
  PressureResolutionAng = (0,0,0)
  PressureResolutionLin = (0,0,0)
  RotationAngle = 0
  RotationAxis = (0,0,0)
  RotationCenter = (0,0,0)
  SwitchMode = false
  Translation = (0,0,-1)
FEATURE [App::Part] Part105  label="FrBtnSil[5][2]"
  Group = -> [Box199,FPSimButton082,Fillet085,Box283,FPSimLED183]
  License = CC BY 3.0
  LicenseURL = http://creativecommons.org/licenses/by/3.0/
  Origin = -> Origin099
  Placement = pos=(26,13,0) rot=(0,0,1;0rad)
FEATURE [Part::Box] Box284  label="Cube252"
  AttacherType = Attacher::AttachEngine3D
  Height = 1
  Length = 25
  Width = 18.5
FEATURE [Part::Fillet] Fillet086
  Base = -> Box284
  Edges = 8 edges r=0.2: [Edge1,Edge2,Edge3,Edge5,Edge6,Edge7,Edge10,Edge12]
FEATURE [App::DocumentObjectGroupPython] FPSimLED184  label="BtnSilLed[6][2]"  # scripted group (container) (typed FeaturePython)
  Group = -> [Fillet086]
  Unenlightened_Blue = 120
  Unenlightened_Green = 120
  Unenlightened_Red = 120
FEATURE [App::DocumentObjectGroupPython] FPSimButton087  label="BtnSil[6][2]"  # scripted group (container) (typed FeaturePython)
  Group = -> [FPSimLED184]
  PressureResolutionAng = (0,0,0)
  PressureResolutionLin = (0,0,0)
  RotationAngle = 0
  RotationAxis = (0,0,0)
  RotationCenter = (0,0,0)
  SwitchMode = false
  Translation = (0,0,-1)
FEATURE [App::Part] Part102  label="FrBtnSil[6][2]"
  Group = -> [Box201,FPSimButton087,Box284,Fillet086,FPSimLED184]
  License = CC BY 3.0
  LicenseURL = http://creativecommons.org/licenses/by/3.0/
  Origin = -> Origin105
  Placement = pos=(55,13,0) rot=(0,0,1;0rad)
FEATURE [Part::Box] Box285  label="Cube253"
  AttacherType = Attacher::AttachEngine3D
  Height = 1
  Length = 25
  Width = 18.5
FEATURE [Part::Fillet] Fillet087
  Base = -> Box285
  Edges = 8 edges r=0.2: [Edge1,Edge2,Edge3,Edge5,Edge6,Edge7,Edge10,Edge12]
FEATURE [App::DocumentObjectGroupPython] FPSimLED185  label="BtnSilLed[7][2]"  # scripted group (container) (typed FeaturePython)
  Group = -> [Fillet087]
  Unenlightened_Blue = 120
  Unenlightened_Green = 120
  Unenlightened_Red = 120
FEATURE [App::DocumentObjectGroupPython] FPSimButton086  label="BtnSil[7][2]"  # scripted group (container) (typed FeaturePython)
  Group = -> [FPSimLED185]
  PressureResolutionAng = (0,0,0)
  PressureResolutionLin = (0,0,0)
  RotationAngle = 0
  RotationAxis = (0,0,0)
  RotationCenter = (0,0,0)
  SwitchMode = false
  Translation = (0,0,-1)
FEATURE [App::Part] Part104  label="FrBtnSil[7][2]"
  Group = -> [Box197,FPSimButton086,Fillet087,Box285,FPSimLED185]
  License = CC BY 3.0
  LicenseURL = http://creativecommons.org/licenses/by/3.0/
  Origin = -> Origin102
  Placement = pos=(84,13,0) rot=(0,0,1;0rad)
FEATURE [App::Part] Part103  label="FrBtnSilRow002"
  Group = -> [Part106,Part107,Part099,Part100,Part101,Part105,Part102,Part104]
  License = CC BY 3.0
  LicenseURL = http://creativecommons.org/licenses/by/3.0/
  Origin = -> Origin107
  Placement = pos=(0,-44,0) rot=(0,0,1;0rad)
FEATURE [Part::Box] Box286  label="Cube254"
  AttacherType = Attacher::AttachEngine3D
  Height = 1
  Length = 25
  Width = 18.5
FEATURE [Part::Fillet] Fillet088
  Base = -> Box286
  Edges = 8 edges r=0.2: [Edge1,Edge2,Edge3,Edge5,Edge6,Edge7,Edge10,Edge12]
FEATURE [App::DocumentObjectGroupPython] FPSimLED186  label="BtnSilLed[0][3]"  # scripted group (container) (typed FeaturePython)
  Group = -> [Fillet088]
  Unenlightened_Blue = 120
  Unenlightened_Green = 120
  Unenlightened_Red = 120
FEATURE [App::DocumentObjectGroupPython] FPSimButton096  label="BtnSil[0][3]"  # scripted group (container) (typed FeaturePython)
  Group = -> [FPSimLED186]
  PressureResolutionAng = (0,0,0)
  PressureResolutionLin = (0,0,0)
  RotationAngle = 0
  RotationAxis = (0,0,0)
  RotationCenter = (0,0,0)
  SwitchMode = false
  Translation = (0,0,-1)
FEATURE [App::Part] Part115  label="FrBtnSil[0][3]"
  Group = -> [Box204,FPSimButton096,Fillet088,Box286,FPSimLED186]
  License = CC BY 3.0
  LicenseURL = http://creativecommons.org/licenses/by/3.0/
  Origin = -> Origin115
  Placement = pos=(-119,13,0) rot=(0,0,1;0rad)
FEATURE [Part::Box] Box287  label="Cube255"
  AttacherType = Attacher::AttachEngine3D
  Height = 1
  Length = 25
  Width = 18.5
FEATURE [Part::Fillet] Fillet089
  Base = -> Box287
  Edges = 8 edges r=0.2: [Edge1,Edge2,Edge3,Edge5,Edge6,Edge7,Edge10,Edge12]
FEATURE [App::DocumentObjectGroupPython] FPSimLED187  label="BtnSilLed[1][3]"  # scripted group (container) (typed FeaturePython)
  Group = -> [Fillet089]
  Unenlightened_Blue = 120
  Unenlightened_Green = 120
  Unenlightened_Red = 120
FEATURE [App::DocumentObjectGroupPython] FPSimButton089  label="BtnSil[1][3]"  # scripted group (container) (typed FeaturePython)
  Group = -> [FPSimLED187]
  PressureResolutionAng = (0,0,0)
  PressureResolutionLin = (0,0,0)
  RotationAngle = 0
  RotationAxis = (0,0,0)
  RotationCenter = (0,0,0)
  SwitchMode = false
  Translation = (0,0,-1)
FEATURE [App::Part] Part116  label="FrBtnSil[1][3]"
  Group = -> [Box208,FPSimButton089,Fillet089,Box287,FPSimLED187]
  License = CC BY 3.0
  LicenseURL = http://creativecommons.org/licenses/by/3.0/
  Origin = -> Origin112
  Placement = pos=(-90,13,0) rot=(0,0,1;0rad)
FEATURE [Part::Box] Box288  label="Cube256"
  AttacherType = Attacher::AttachEngine3D
  Height = 1
  Length = 25
  Width = 18.5
FEATURE [Part::Fillet] Fillet090
  Base = -> Box288
  Edges = 8 edges r=0.2: [Edge1,Edge2,Edge3,Edge5,Edge6,Edge7,Edge10,Edge12]
FEATURE [App::DocumentObjectGroupPython] FPSimLED188  label="BtnSilLed[2][3]"  # scripted group (container) (typed FeaturePython)
  Group = -> [Fillet090]
  Unenlightened_Blue = 120
  Unenlightened_Green = 120
  Unenlightened_Red = 120
FEATURE [App::DocumentObjectGroupPython] FPSimButton091  label="BtnSil[2][3]"  # scripted group (container) (typed FeaturePython)
  Group = -> [FPSimLED188]
  PressureResolutionAng = (0,0,0)
  PressureResolutionLin = (0,0,0)
  RotationAngle = 0
  RotationAxis = (0,0,0)
  RotationCenter = (0,0,0)
  SwitchMode = false
  Translation = (0,0,-1)
FEATURE [App::Part] Part108  label="FrBtnSil[2][3]"
  Group = -> [Box202,FPSimButton091,Box288,Fillet090,FPSimLED188]
  License = CC BY 3.0
  LicenseURL = http://creativecommons.org/licenses/by/3.0/
  Origin = -> Origin109
  Placement = pos=(-61,13,0) rot=(0,0,1;0rad)
FEATURE [Part::Box] Box289  label="Cube257"
  AttacherType = Attacher::AttachEngine3D
  Height = 1
  Length = 25
  Width = 18.5
FEATURE [Part::Fillet] Fillet091
  Base = -> Box289
  Edges = 8 edges r=0.2: [Edge1,Edge2,Edge3,Edge5,Edge6,Edge7,Edge10,Edge12]
FEATURE [App::DocumentObjectGroupPython] FPSimLED189  label="BtnSilLed[3][3]"  # scripted group (container) (typed FeaturePython)
  Group = -> [Fillet091]
  Unenlightened_Blue = 120
  Unenlightened_Green = 120
  Unenlightened_Red = 120
FEATURE [App::DocumentObjectGroupPython] FPSimButton093  label="BtnSil[3][3]"  # scripted group (container) (typed FeaturePython)
  Group = -> [FPSimLED189]
  PressureResolutionAng = (0,0,0)
  PressureResolutionLin = (0,0,0)
  RotationAngle = 0
  RotationAxis = (0,0,0)
  RotationCenter = (0,0,0)
  SwitchMode = false
  Translation = (0,0,-1)
FEATURE [App::Part] Part109  label="FrBtnSil[3][3]"
  Group = -> [Box206,FPSimButton093,Box289,Fillet091,FPSimLED189]
  License = CC BY 3.0
  LicenseURL = http://creativecommons.org/licenses/by/3.0/
  Origin = -> Origin113
  Placement = pos=(-32,13,0) rot=(0,0,1;0rad)
FEATURE [Part::Box] Box290  label="Cube258"
  AttacherType = Attacher::AttachEngine3D
  Height = 1
  Length = 25
  Width = 18.5
FEATURE [Part::Fillet] Fillet092
  Base = -> Box290
  Edges = 8 edges r=0.2: [Edge1,Edge2,Edge3,Edge5,Edge6,Edge7,Edge10,Edge12]
FEATURE [App::DocumentObjectGroupPython] FPSimLED190  label="BtnSilLed[4][3]"  # scripted group (container) (typed FeaturePython)
  Group = -> [Fillet092]
  Unenlightened_Blue = 120
  Unenlightened_Green = 120
  Unenlightened_Red = 120
FEATURE [App::DocumentObjectGroupPython] FPSimButton092  label="BtnSil[4][3]"  # scripted group (container) (typed FeaturePython)
  Group = -> [FPSimLED190]
  PressureResolutionAng = (0,0,0)
  PressureResolutionLin = (0,0,0)
  RotationAngle = 0
  RotationAxis = (0,0,0)
  RotationCenter = (0,0,0)
  SwitchMode = false
  Translation = (0,0,-1)
FEATURE [App::Part] Part110  label="FrBtnSil[4][3]"
  Group = -> [Box203,FPSimButton092,Box290,Fillet092,FPSimLED190]
  License = CC BY 3.0
  LicenseURL = http://creativecommons.org/licenses/by/3.0/
  Origin = -> Origin110
  Placement = pos=(-3,13,0) rot=(0,0,1;0rad)
FEATURE [Part::Box] Box291  label="Cube259"
  AttacherType = Attacher::AttachEngine3D
  Height = 1
  Length = 25
  Width = 18.5
FEATURE [Part::Fillet] Fillet093
  Base = -> Box291
  Edges = 8 edges r=0.2: [Edge1,Edge2,Edge3,Edge5,Edge6,Edge7,Edge10,Edge12]
FEATURE [App::DocumentObjectGroupPython] FPSimLED191  label="BtnSilLed[5][3]"  # scripted group (container) (typed FeaturePython)
  Group = -> [Fillet093]
  Unenlightened_Blue = 120
  Unenlightened_Green = 120
  Unenlightened_Red = 120
FEATURE [App::DocumentObjectGroupPython] FPSimButton090  label="BtnSil[5][3]"  # scripted group (container) (typed FeaturePython)
  Group = -> [FPSimLED191]
  PressureResolutionAng = (0,0,0)
  PressureResolutionLin = (0,0,0)
  RotationAngle = 0
  RotationAxis = (0,0,0)
  RotationCenter = (0,0,0)
  SwitchMode = false
  Translation = (0,0,-1)
FEATURE [App::Part] Part114  label="FrBtnSil[5][3]"
  Group = -> [Box207,FPSimButton090,Box291,Fillet093,FPSimLED191]
  License = CC BY 3.0
  LicenseURL = http://creativecommons.org/licenses/by/3.0/
  Origin = -> Origin108
  Placement = pos=(26,13,0) rot=(0,0,1;0rad)
FEATURE [Part::Box] Box292  label="Cube260"
  AttacherType = Attacher::AttachEngine3D
  Height = 1
  Length = 25
  Width = 18.5
FEATURE [Part::Fillet] Fillet094
  Base = -> Box292
  Edges = 8 edges r=0.2: [Edge1,Edge2,Edge3,Edge5,Edge6,Edge7,Edge10,Edge12]
FEATURE [App::DocumentObjectGroupPython] FPSimLED192  label="BtnSilLed[6][3]"  # scripted group (container) (typed FeaturePython)
  Group = -> [Fillet094]
  Unenlightened_Blue = 120
  Unenlightened_Green = 120
  Unenlightened_Red = 120
FEATURE [App::DocumentObjectGroupPython] FPSimButton095  label="BtnSil[6][3]"  # scripted group (container) (typed FeaturePython)
  Group = -> [FPSimLED192]
  PressureResolutionAng = (0,0,0)
  PressureResolutionLin = (0,0,0)
  RotationAngle = 0
  RotationAxis = (0,0,0)
  RotationCenter = (0,0,0)
  SwitchMode = false
  Translation = (0,0,-1)
FEATURE [App::Part] Part111  label="FrBtnSil[6][3]"
  Group = -> [Box209,FPSimButton095,Fillet094,Box292,FPSimLED192]
  License = CC BY 3.0
  LicenseURL = http://creativecommons.org/licenses/by/3.0/
  Origin = -> Origin114
  Placement = pos=(55,13,0) rot=(0,0,1;0rad)
FEATURE [Part::Box] Box293  label="Cube261"
  AttacherType = Attacher::AttachEngine3D
  Height = 1
  Length = 25
  Width = 18.5
FEATURE [Part::Fillet] Fillet095
  Base = -> Box293
  Edges = 8 edges r=0.2: [Edge1,Edge2,Edge3,Edge5,Edge6,Edge7,Edge10,Edge12]
FEATURE [App::DocumentObjectGroupPython] FPSimLED193  label="BtnSilLed[7][3]"  # scripted group (container) (typed FeaturePython)
  Group = -> [Fillet095]
  Unenlightened_Blue = 120
  Unenlightened_Green = 120
  Unenlightened_Red = 120
FEATURE [App::DocumentObjectGroupPython] FPSimButton094  label="BtnSil[7][3]"  # scripted group (container) (typed FeaturePython)
  Group = -> [FPSimLED193]
  PressureResolutionAng = (0,0,0)
  PressureResolutionLin = (0,0,0)
  RotationAngle = 0
  RotationAxis = (0,0,0)
  RotationCenter = (0,0,0)
  SwitchMode = false
  Translation = (0,0,-1)
FEATURE [App::Part] Part113  label="FrBtnSil[7][3]"
  Group = -> [Box205,FPSimButton094,Fillet095,Box293,FPSimLED193]
  License = CC BY 3.0
  LicenseURL = http://creativecommons.org/licenses/by/3.0/
  Origin = -> Origin111
  Placement = pos=(84,13,0) rot=(0,0,1;0rad)
FEATURE [App::Part] Part112  label="FrBtnSilRow003"
  Group = -> [Part115,Part116,Part108,Part109,Part110,Part114,Part111,Part113]
  License = CC BY 3.0
  LicenseURL = http://creativecommons.org/licenses/by/3.0/
  Origin = -> Origin116
  Placement = pos=(0,-66,0) rot=(0,0,1;0rad)
FEATURE [Part::Box] Box294  label="Cube262"
  AttacherType = Attacher::AttachEngine3D
  Height = 1
  Length = 25
  Width = 18.5
FEATURE [Part::Fillet] Fillet096
  Base = -> Box294
  Edges = 8 edges r=0.2: [Edge1,Edge2,Edge3,Edge5,Edge6,Edge7,Edge10,Edge12]
FEATURE [App::DocumentObjectGroupPython] FPSimLED194  label="BtnSilLed[0][4]"  # scripted group (container) (typed FeaturePython)
  Group = -> [Fillet096]
  Unenlightened_Blue = 120
  Unenlightened_Green = 120
  Unenlightened_Red = 120
FEATURE [App::DocumentObjectGroupPython] FPSimButton104  label="BtnSil[0][4]"  # scripted group (container) (typed FeaturePython)
  Group = -> [FPSimLED194]
  PressureResolutionAng = (0,0,0)
  PressureResolutionLin = (0,0,0)
  RotationAngle = 0
  RotationAxis = (0,0,0)
  RotationCenter = (0,0,0)
  SwitchMode = false
  Translation = (0,0,-1)
FEATURE [App::Part] Part124  label="FrBtnSil[0][4]"
  Group = -> [Box212,FPSimButton104,Fillet096,Box294,FPSimLED194]
  License = CC BY 3.0
  LicenseURL = http://creativecommons.org/licenses/by/3.0/
  Origin = -> Origin124
  Placement = pos=(-119,13,0) rot=(0,0,1;0rad)
FEATURE [Part::Box] Box295  label="Cube263"
  AttacherType = Attacher::AttachEngine3D
  Height = 1
  Length = 25
  Width = 18.5
FEATURE [Part::Fillet] Fillet097
  Base = -> Box295
  Edges = 8 edges r=0.2: [Edge1,Edge2,Edge3,Edge5,Edge6,Edge7,Edge10,Edge12]
FEATURE [App::DocumentObjectGroupPython] FPSimLED195  label="BtnSilLed[1][4]"  # scripted group (container) (typed FeaturePython)
  Group = -> [Fillet097]
  Unenlightened_Blue = 120
  Unenlightened_Green = 120
  Unenlightened_Red = 120
FEATURE [App::DocumentObjectGroupPython] FPSimButton097  label="BtnSil[1][4]"  # scripted group (container) (typed FeaturePython)
  Group = -> [FPSimLED195]
  PressureResolutionAng = (0,0,0)
  PressureResolutionLin = (0,0,0)
  RotationAngle = 0
  RotationAxis = (0,0,0)
  RotationCenter = (0,0,0)
  SwitchMode = false
  Translation = (0,0,-1)
FEATURE [App::Part] Part125  label="FrBtnSil[1][4]"
  Group = -> [Box216,FPSimButton097,Box295,Fillet097,FPSimLED195]
  License = CC BY 3.0
  LicenseURL = http://creativecommons.org/licenses/by/3.0/
  Origin = -> Origin121
  Placement = pos=(-90,13,0) rot=(0,0,1;0rad)
FEATURE [Part::Box] Box296  label="Cube264"
  AttacherType = Attacher::AttachEngine3D
  Height = 1
  Length = 25
  Width = 18.5
FEATURE [Part::Fillet] Fillet098
  Base = -> Box296
  Edges = 8 edges r=0.2: [Edge1,Edge2,Edge3,Edge5,Edge6,Edge7,Edge10,Edge12]
FEATURE [App::DocumentObjectGroupPython] FPSimLED196  label="BtnSilLed[2][4]"  # scripted group (container) (typed FeaturePython)
  Group = -> [Fillet098]
  Unenlightened_Blue = 120
  Unenlightened_Green = 120
  Unenlightened_Red = 120
FEATURE [App::DocumentObjectGroupPython] FPSimButton099  label="BtnSil[2][4]"  # scripted group (container) (typed FeaturePython)
  Group = -> [FPSimLED196]
  PressureResolutionAng = (0,0,0)
  PressureResolutionLin = (0,0,0)
  RotationAngle = 0
  RotationAxis = (0,0,0)
  RotationCenter = (0,0,0)
  SwitchMode = false
  Translation = (0,0,-1)
FEATURE [App::Part] Part117  label="FrBtnSil[2][4]"
  Group = -> [Box210,FPSimButton099,Fillet098,Box296,FPSimLED196]
  License = CC BY 3.0
  LicenseURL = http://creativecommons.org/licenses/by/3.0/
  Origin = -> Origin118
  Placement = pos=(-61,13,0) rot=(0,0,1;0rad)
FEATURE [Part::Box] Box297  label="Cube265"
  AttacherType = Attacher::AttachEngine3D
  Height = 1
  Length = 25
  Width = 18.5
FEATURE [Part::Fillet] Fillet099
  Base = -> Box297
  Edges = 8 edges r=0.2: [Edge1,Edge2,Edge3,Edge5,Edge6,Edge7,Edge10,Edge12]
FEATURE [App::DocumentObjectGroupPython] FPSimLED197  label="BtnSilLed[3][4]"  # scripted group (container) (typed FeaturePython)
  Group = -> [Fillet099]
  Unenlightened_Blue = 120
  Unenlightened_Green = 120
  Unenlightened_Red = 120
FEATURE [App::DocumentObjectGroupPython] FPSimButton101  label="BtnSil[3][4]"  # scripted group (container) (typed FeaturePython)
  Group = -> [FPSimLED197]
  PressureResolutionAng = (0,0,0)
  PressureResolutionLin = (0,0,0)
  RotationAngle = 0
  RotationAxis = (0,0,0)
  RotationCenter = (0,0,0)
  SwitchMode = false
  Translation = (0,0,-1)
FEATURE [App::Part] Part118  label="FrBtnSil[3][4]"
  Group = -> [Box214,FPSimButton101,Fillet099,Box297,FPSimLED197]
  License = CC BY 3.0
  LicenseURL = http://creativecommons.org/licenses/by/3.0/
  Origin = -> Origin122
  Placement = pos=(-32,13,0) rot=(0,0,1;0rad)
FEATURE [Part::Box] Box298  label="Cube266"
  AttacherType = Attacher::AttachEngine3D
  Height = 1
  Length = 25
  Width = 18.5
FEATURE [Part::Fillet] Fillet100
  Base = -> Box298
  Edges = 8 edges r=0.2: [Edge1,Edge2,Edge3,Edge5,Edge6,Edge7,Edge10,Edge12]
FEATURE [App::DocumentObjectGroupPython] FPSimLED198  label="BtnSilLed[4][4]"  # scripted group (container) (typed FeaturePython)
  Group = -> [Fillet100]
  Unenlightened_Blue = 120
  Unenlightened_Green = 120
  Unenlightened_Red = 120
FEATURE [App::DocumentObjectGroupPython] FPSimButton100  label="BtnSil[4][4]"  # scripted group (container) (typed FeaturePython)
  Group = -> [FPSimLED198]
  PressureResolutionAng = (0,0,0)
  PressureResolutionLin = (0,0,0)
  RotationAngle = 0
  RotationAxis = (0,0,0)
  RotationCenter = (0,0,0)
  SwitchMode = false
  Translation = (0,0,-1)
FEATURE [App::Part] Part119  label="FrBtnSil[4][4]"
  Group = -> [Box211,FPSimButton100,Box298,Fillet100,FPSimLED198]
  License = CC BY 3.0
  LicenseURL = http://creativecommons.org/licenses/by/3.0/
  Origin = -> Origin119
  Placement = pos=(-3,13,0) rot=(0,0,1;0rad)
FEATURE [Part::Box] Box299  label="Cube267"
  AttacherType = Attacher::AttachEngine3D
  Height = 1
  Length = 25
  Width = 18.5
FEATURE [Part::Fillet] Fillet101
  Base = -> Box299
  Edges = 8 edges r=0.2: [Edge1,Edge2,Edge3,Edge5,Edge6,Edge7,Edge10,Edge12]
FEATURE [App::DocumentObjectGroupPython] FPSimLED199  label="BtnSilLed[5][4]"  # scripted group (container) (typed FeaturePython)
  Group = -> [Fillet101]
  Unenlightened_Blue = 120
  Unenlightened_Green = 120
  Unenlightened_Red = 120
FEATURE [App::DocumentObjectGroupPython] FPSimButton098  label="BtnSil[5][4]"  # scripted group (container) (typed FeaturePython)
  Group = -> [FPSimLED199]
  PressureResolutionAng = (0,0,0)
  PressureResolutionLin = (0,0,0)
  RotationAngle = 0
  RotationAxis = (0,0,0)
  RotationCenter = (0,0,0)
  SwitchMode = false
  Translation = (0,0,-1)
FEATURE [App::Part] Part123  label="FrBtnSil[5][4]"
  Group = -> [Box215,FPSimButton098,Box299,Fillet101,FPSimLED199]
  License = CC BY 3.0
  LicenseURL = http://creativecommons.org/licenses/by/3.0/
  Origin = -> Origin117
  Placement = pos=(26,13,0) rot=(0,0,1;0rad)
FEATURE [Part::Box] Box300  label="Cube268"
  AttacherType = Attacher::AttachEngine3D
  Height = 1
  Length = 25
  Width = 18.5
FEATURE [Part::Fillet] Fillet102
  Base = -> Box300
  Edges = 8 edges r=0.2: [Edge1,Edge2,Edge3,Edge5,Edge6,Edge7,Edge10,Edge12]
FEATURE [App::DocumentObjectGroupPython] FPSimLED200  label="BtnSilLed[6][4]"  # scripted group (container) (typed FeaturePython)
  Group = -> [Fillet102]
  Unenlightened_Blue = 120
  Unenlightened_Green = 120
  Unenlightened_Red = 120
FEATURE [App::DocumentObjectGroupPython] FPSimButton103  label="BtnSil[6][4]"  # scripted group (container) (typed FeaturePython)
  Group = -> [FPSimLED200]
  PressureResolutionAng = (0,0,0)
  PressureResolutionLin = (0,0,0)
  RotationAngle = 0
  RotationAxis = (0,0,0)
  RotationCenter = (0,0,0)
  SwitchMode = false
  Translation = (0,0,-1)
FEATURE [App::Part] Part120  label="FrBtnSil[6][4]"
  Group = -> [Box217,FPSimButton103,Box300,Fillet102,FPSimLED200]
  License = CC BY 3.0
  LicenseURL = http://creativecommons.org/licenses/by/3.0/
  Origin = -> Origin123
  Placement = pos=(55,13,0) rot=(0,0,1;0rad)
FEATURE [Part::Box] Box301  label="Cube269"
  AttacherType = Attacher::AttachEngine3D
  Height = 1
  Length = 25
  Width = 18.5
FEATURE [Part::Fillet] Fillet103
  Base = -> Box301
  Edges = 8 edges r=0.2: [Edge1,Edge2,Edge3,Edge5,Edge6,Edge7,Edge10,Edge12]
FEATURE [App::DocumentObjectGroupPython] FPSimLED201  label="BtnSilLed[7][4]"  # scripted group (container) (typed FeaturePython)
  Group = -> [Fillet103]
  Unenlightened_Blue = 120
  Unenlightened_Green = 120
  Unenlightened_Red = 120
FEATURE [App::DocumentObjectGroupPython] FPSimButton102  label="BtnSil[7][4]"  # scripted group (container) (typed FeaturePython)
  Group = -> [FPSimLED201]
  PressureResolutionAng = (0,0,0)
  PressureResolutionLin = (0,0,0)
  RotationAngle = 0
  RotationAxis = (0,0,0)
  RotationCenter = (0,0,0)
  SwitchMode = false
  Translation = (0,0,-1)
FEATURE [App::Part] Part122  label="FrBtnSil[7][4]"
  Group = -> [Box213,FPSimButton102,Box301,Fillet103,FPSimLED201]
  License = CC BY 3.0
  LicenseURL = http://creativecommons.org/licenses/by/3.0/
  Origin = -> Origin120
  Placement = pos=(84,13,0) rot=(0,0,1;0rad)
FEATURE [App::Part] Part121  label="FrBtnSilRow004"
  Group = -> [Part124,Part125,Part117,Part118,Part119,Part123,Part120,Part122]
  License = CC BY 3.0
  LicenseURL = http://creativecommons.org/licenses/by/3.0/
  Origin = -> Origin125
  Placement = pos=(0,-88,0) rot=(0,0,1;0rad)
FEATURE [Part::Box] Box302  label="Cube270"
  AttacherType = Attacher::AttachEngine3D
  Height = 1
  Length = 25
  Width = 18.5
FEATURE [Part::Fillet] Fillet104
  Base = -> Box302
  Edges = 8 edges r=0.2: [Edge1,Edge2,Edge3,Edge5,Edge6,Edge7,Edge10,Edge12]
FEATURE [App::DocumentObjectGroupPython] FPSimLED202  label="BtnSilLed[0][5]"  # scripted group (container) (typed FeaturePython)
  Group = -> [Fillet104]
  Unenlightened_Blue = 120
  Unenlightened_Green = 120
  Unenlightened_Red = 120
FEATURE [App::DocumentObjectGroupPython] FPSimButton112  label="BtnSil[0][5]"  # scripted group (container) (typed FeaturePython)
  Group = -> [FPSimLED202]
  PressureResolutionAng = (0,0,0)
  PressureResolutionLin = (0,0,0)
  RotationAngle = 0
  RotationAxis = (0,0,0)
  RotationCenter = (0,0,0)
  SwitchMode = false
  Translation = (0,0,-1)
FEATURE [App::Part] Part133  label="FrBtnSil[0][5]"
  Group = -> [Box220,FPSimButton112,Box302,Fillet104,FPSimLED202]
  License = CC BY 3.0
  LicenseURL = http://creativecommons.org/licenses/by/3.0/
  Origin = -> Origin133
  Placement = pos=(-119,13,0) rot=(0,0,1;0rad)
FEATURE [Part::Box] Box303  label="Cube271"
  AttacherType = Attacher::AttachEngine3D
  Height = 1
  Length = 25
  Width = 18.5
FEATURE [Part::Fillet] Fillet105
  Base = -> Box303
  Edges = 8 edges r=0.2: [Edge1,Edge2,Edge3,Edge5,Edge6,Edge7,Edge10,Edge12]
FEATURE [App::DocumentObjectGroupPython] FPSimLED203  label="BtnSilLed[1][5]"  # scripted group (container) (typed FeaturePython)
  Group = -> [Fillet105]
  Unenlightened_Blue = 120
  Unenlightened_Green = 120
  Unenlightened_Red = 120
FEATURE [App::DocumentObjectGroupPython] FPSimButton105  label="BtnSil[1][5]"  # scripted group (container) (typed FeaturePython)
  Group = -> [FPSimLED203]
  PressureResolutionAng = (0,0,0)
  PressureResolutionLin = (0,0,0)
  RotationAngle = 0
  RotationAxis = (0,0,0)
  RotationCenter = (0,0,0)
  SwitchMode = false
  Translation = (0,0,-1)
FEATURE [App::Part] Part134  label="FrBtnSil[1][5]"
  Group = -> [Box224,FPSimButton105,Fillet105,Box303,FPSimLED203]
  License = CC BY 3.0
  LicenseURL = http://creativecommons.org/licenses/by/3.0/
  Origin = -> Origin130
  Placement = pos=(-90,13,0) rot=(0,0,1;0rad)
FEATURE [Part::Box] Box304  label="Cube272"
  AttacherType = Attacher::AttachEngine3D
  Height = 1
  Length = 25
  Width = 18.5
FEATURE [Part::Fillet] Fillet106
  Base = -> Box304
  Edges = 8 edges r=0.2: [Edge1,Edge2,Edge3,Edge5,Edge6,Edge7,Edge10,Edge12]
FEATURE [App::DocumentObjectGroupPython] FPSimLED204  label="BtnSilLed[2][5]"  # scripted group (container) (typed FeaturePython)
  Group = -> [Fillet106]
  Unenlightened_Blue = 120
  Unenlightened_Green = 120
  Unenlightened_Red = 120
FEATURE [App::DocumentObjectGroupPython] FPSimButton107  label="BtnSil[2][5]"  # scripted group (container) (typed FeaturePython)
  Group = -> [FPSimLED204]
  PressureResolutionAng = (0,0,0)
  PressureResolutionLin = (0,0,0)
  RotationAngle = 0
  RotationAxis = (0,0,0)
  RotationCenter = (0,0,0)
  SwitchMode = false
  Translation = (0,0,-1)
FEATURE [App::Part] Part126  label="FrBtnSil[2][5]"
  Group = -> [Box218,FPSimButton107,Box304,Fillet106,FPSimLED204]
  License = CC BY 3.0
  LicenseURL = http://creativecommons.org/licenses/by/3.0/
  Origin = -> Origin127
  Placement = pos=(-61,13,0) rot=(0,0,1;0rad)
FEATURE [Part::Box] Box305  label="Cube273"
  AttacherType = Attacher::AttachEngine3D
  Height = 1
  Length = 25
  Width = 18.5
FEATURE [Part::Fillet] Fillet107
  Base = -> Box305
  Edges = 8 edges r=0.2: [Edge1,Edge2,Edge3,Edge5,Edge6,Edge7,Edge10,Edge12]
FEATURE [App::DocumentObjectGroupPython] FPSimLED205  label="BtnSilLed[3][5]"  # scripted group (container) (typed FeaturePython)
  Group = -> [Fillet107]
  Unenlightened_Blue = 120
  Unenlightened_Green = 120
  Unenlightened_Red = 120
FEATURE [App::DocumentObjectGroupPython] FPSimButton109  label="BtnSil[3][5]"  # scripted group (container) (typed FeaturePython)
  Group = -> [FPSimLED205]
  PressureResolutionAng = (0,0,0)
  PressureResolutionLin = (0,0,0)
  RotationAngle = 0
  RotationAxis = (0,0,0)
  RotationCenter = (0,0,0)
  SwitchMode = false
  Translation = (0,0,-1)
FEATURE [App::Part] Part127  label="FrBtnSil[3][5]"
  Group = -> [Box222,FPSimButton109,Box305,Fillet107,FPSimLED205]
  License = CC BY 3.0
  LicenseURL = http://creativecommons.org/licenses/by/3.0/
  Origin = -> Origin131
  Placement = pos=(-32,13,0) rot=(0,0,1;0rad)
FEATURE [Part::Box] Box306  label="Cube274"
  AttacherType = Attacher::AttachEngine3D
  Height = 1
  Length = 25
  Width = 18.5
FEATURE [Part::Fillet] Fillet108
  Base = -> Box306
  Edges = 8 edges r=0.2: [Edge1,Edge2,Edge3,Edge5,Edge6,Edge7,Edge10,Edge12]
FEATURE [App::DocumentObjectGroupPython] FPSimLED206  label="BtnSilLed[4][5]"  # scripted group (container) (typed FeaturePython)
  Group = -> [Fillet108]
  Unenlightened_Blue = 120
  Unenlightened_Green = 120
  Unenlightened_Red = 120
FEATURE [App::DocumentObjectGroupPython] FPSimButton108  label="BtnSil[4][5]"  # scripted group (container) (typed FeaturePython)
  Group = -> [FPSimLED206]
  PressureResolutionAng = (0,0,0)
  PressureResolutionLin = (0,0,0)
  RotationAngle = 0
  RotationAxis = (0,0,0)
  RotationCenter = (0,0,0)
  SwitchMode = false
  Translation = (0,0,-1)
FEATURE [App::Part] Part128  label="FrBtnSil[4][5]"
  Group = -> [Box219,FPSimButton108,Fillet108,Box306,FPSimLED206]
  License = CC BY 3.0
  LicenseURL = http://creativecommons.org/licenses/by/3.0/
  Origin = -> Origin128
  Placement = pos=(-3,13,0) rot=(0,0,1;0rad)
FEATURE [Part::Box] Box307  label="Cube275"
  AttacherType = Attacher::AttachEngine3D
  Height = 1
  Length = 25
  Width = 18.5
FEATURE [Part::Fillet] Fillet109
  Base = -> Box307
  Edges = 8 edges r=0.2: [Edge1,Edge2,Edge3,Edge5,Edge6,Edge7,Edge10,Edge12]
FEATURE [App::DocumentObjectGroupPython] FPSimLED207  label="BtnSilLed[5][5]"  # scripted group (container) (typed FeaturePython)
  Group = -> [Fillet109]
  Unenlightened_Blue = 120
  Unenlightened_Green = 120
  Unenlightened_Red = 120
FEATURE [App::DocumentObjectGroupPython] FPSimButton106  label="BtnSil[5][5]"  # scripted group (container) (typed FeaturePython)
  Group = -> [FPSimLED207]
  PressureResolutionAng = (0,0,0)
  PressureResolutionLin = (0,0,0)
  RotationAngle = 0
  RotationAxis = (0,0,0)
  RotationCenter = (0,0,0)
  SwitchMode = false
  Translation = (0,0,-1)
FEATURE [App::Part] Part132  label="FrBtnSil[5][5]"
  Group = -> [Box223,FPSimButton106,Box307,Fillet109,FPSimLED207]
  License = CC BY 3.0
  LicenseURL = http://creativecommons.org/licenses/by/3.0/
  Origin = -> Origin126
  Placement = pos=(26,13,0) rot=(0,0,1;0rad)
FEATURE [Part::Box] Box308  label="Cube276"
  AttacherType = Attacher::AttachEngine3D
  Height = 1
  Length = 25
  Width = 18.5
FEATURE [Part::Fillet] Fillet110
  Base = -> Box308
  Edges = 8 edges r=0.2: [Edge1,Edge2,Edge3,Edge5,Edge6,Edge7,Edge10,Edge12]
FEATURE [App::DocumentObjectGroupPython] FPSimLED208  label="BtnSilLed[6][5]"  # scripted group (container) (typed FeaturePython)
  Group = -> [Fillet110]
  Unenlightened_Blue = 120
  Unenlightened_Green = 120
  Unenlightened_Red = 120
FEATURE [App::DocumentObjectGroupPython] FPSimButton111  label="BtnSil[6][5]"  # scripted group (container) (typed FeaturePython)
  Group = -> [FPSimLED208]
  PressureResolutionAng = (0,0,0)
  PressureResolutionLin = (0,0,0)
  RotationAngle = 0
  RotationAxis = (0,0,0)
  RotationCenter = (0,0,0)
  SwitchMode = false
  Translation = (0,0,-1)
FEATURE [App::Part] Part129  label="FrBtnSil[6][5]"
  Group = -> [Box225,FPSimButton111,Fillet110,Box308,FPSimLED208]
  License = CC BY 3.0
  LicenseURL = http://creativecommons.org/licenses/by/3.0/
  Origin = -> Origin132
  Placement = pos=(55,13,0) rot=(0,0,1;0rad)
FEATURE [Part::Box] Box309  label="Cube277"
  AttacherType = Attacher::AttachEngine3D
  Height = 1
  Length = 25
  Width = 18.5
FEATURE [Part::Fillet] Fillet111
  Base = -> Box309
  Edges = 8 edges r=0.2: [Edge1,Edge2,Edge3,Edge5,Edge6,Edge7,Edge10,Edge12]
FEATURE [App::DocumentObjectGroupPython] FPSimLED209  label="BtnSilLed[7][5]"  # scripted group (container) (typed FeaturePython)
  Group = -> [Fillet111]
  Unenlightened_Blue = 120
  Unenlightened_Green = 120
  Unenlightened_Red = 120
FEATURE [App::DocumentObjectGroupPython] FPSimButton110  label="BtnSil[7][5]"  # scripted group (container) (typed FeaturePython)
  Group = -> [FPSimLED209]
  PressureResolutionAng = (0,0,0)
  PressureResolutionLin = (0,0,0)
  RotationAngle = 0
  RotationAxis = (0,0,0)
  RotationCenter = (0,0,0)
  SwitchMode = false
  Translation = (0,0,-1)
FEATURE [App::Part] Part131  label="FrBtnSil[7][5]"
  Group = -> [Box221,FPSimButton110,Fillet111,Box309,FPSimLED209]
  License = CC BY 3.0
  LicenseURL = http://creativecommons.org/licenses/by/3.0/
  Origin = -> Origin129
  Placement = pos=(84,13,0) rot=(0,0,1;0rad)
FEATURE [App::Part] Part130  label="FrBtnSilRow005"
  Group = -> [Part133,Part134,Part126,Part127,Part128,Part132,Part129,Part131]
  License = CC BY 3.0
  LicenseURL = http://creativecommons.org/licenses/by/3.0/
  Origin = -> Origin134
  Placement = pos=(0,-110,0) rot=(0,0,1;0rad)
FEATURE [Part::Box] Box310  label="Cube278"
  AttacherType = Attacher::AttachEngine3D
  Height = 1
  Length = 25
  Width = 18.5
FEATURE [Part::Fillet] Fillet112
  Base = -> Box310
  Edges = 8 edges r=0.2: [Edge1,Edge2,Edge3,Edge5,Edge6,Edge7,Edge10,Edge12]
FEATURE [App::DocumentObjectGroupPython] FPSimLED210  label="BtnSilLed[0][6]"  # scripted group (container) (typed FeaturePython)
  Group = -> [Fillet112]
  Unenlightened_Blue = 120
  Unenlightened_Green = 120
  Unenlightened_Red = 120
FEATURE [App::DocumentObjectGroupPython] FPSimButton120  label="BtnSil[0][6]"  # scripted group (container) (typed FeaturePython)
  Group = -> [FPSimLED210]
  PressureResolutionAng = (0,0,0)
  PressureResolutionLin = (0,0,0)
  RotationAngle = 0
  RotationAxis = (0,0,0)
  RotationCenter = (0,0,0)
  SwitchMode = false
  Translation = (0,0,-1)
FEATURE [App::Part] Part142  label="FrBtnSil[0][6]"
  Group = -> [Box228,FPSimButton120,Box310,Fillet112,FPSimLED210]
  License = CC BY 3.0
  LicenseURL = http://creativecommons.org/licenses/by/3.0/
  Origin = -> Origin142
  Placement = pos=(-119,13,0) rot=(0,0,1;0rad)
FEATURE [Part::Box] Box311  label="Cube279"
  AttacherType = Attacher::AttachEngine3D
  Height = 1
  Length = 25
  Width = 18.5
FEATURE [Part::Fillet] Fillet113
  Base = -> Box311
  Edges = 8 edges r=0.2: [Edge1,Edge2,Edge3,Edge5,Edge6,Edge7,Edge10,Edge12]
FEATURE [App::DocumentObjectGroupPython] FPSimLED211  label="BtnSilLed[1][6]"  # scripted group (container) (typed FeaturePython)
  Group = -> [Fillet113]
  Unenlightened_Blue = 120
  Unenlightened_Green = 120
  Unenlightened_Red = 120
FEATURE [App::DocumentObjectGroupPython] FPSimButton113  label="BtnSil[1][6]"  # scripted group (container) (typed FeaturePython)
  Group = -> [FPSimLED211]
  PressureResolutionAng = (0,0,0)
  PressureResolutionLin = (0,0,0)
  RotationAngle = 0
  RotationAxis = (0,0,0)
  RotationCenter = (0,0,0)
  SwitchMode = false
  Translation = (0,0,-1)
FEATURE [App::Part] Part143  label="FrBtnSil[1][6]"
  Group = -> [Box232,FPSimButton113,Fillet113,Box311,FPSimLED211]
  License = CC BY 3.0
  LicenseURL = http://creativecommons.org/licenses/by/3.0/
  Origin = -> Origin139
  Placement = pos=(-90,13,0) rot=(0,0,1;0rad)
FEATURE [Part::Box] Box312  label="Cube280"
  AttacherType = Attacher::AttachEngine3D
  Height = 1
  Length = 25
  Width = 18.5
FEATURE [Part::Fillet] Fillet114
  Base = -> Box312
  Edges = 8 edges r=0.2: [Edge1,Edge2,Edge3,Edge5,Edge6,Edge7,Edge10,Edge12]
FEATURE [App::DocumentObjectGroupPython] FPSimLED212  label="BtnSilLed[2][6]"  # scripted group (container) (typed FeaturePython)
  Group = -> [Fillet114]
  Unenlightened_Blue = 120
  Unenlightened_Green = 120
  Unenlightened_Red = 120
FEATURE [App::DocumentObjectGroupPython] FPSimButton115  label="BtnSil[2][6]"  # scripted group (container) (typed FeaturePython)
  Group = -> [FPSimLED212]
  PressureResolutionAng = (0,0,0)
  PressureResolutionLin = (0,0,0)
  RotationAngle = 0
  RotationAxis = (0,0,0)
  RotationCenter = (0,0,0)
  SwitchMode = false
  Translation = (0,0,-1)
FEATURE [App::Part] Part135  label="FrBtnSil[2][6]"
  Group = -> [Box226,FPSimButton115,Fillet114,Box312,FPSimLED212]
  License = CC BY 3.0
  LicenseURL = http://creativecommons.org/licenses/by/3.0/
  Origin = -> Origin136
  Placement = pos=(-61,13,0) rot=(0,0,1;0rad)
FEATURE [Part::Box] Box313  label="Cube281"
  AttacherType = Attacher::AttachEngine3D
  Height = 1
  Length = 25
  Width = 18.5
FEATURE [Part::Fillet] Fillet115
  Base = -> Box313
  Edges = 8 edges r=0.2: [Edge1,Edge2,Edge3,Edge5,Edge6,Edge7,Edge10,Edge12]
FEATURE [App::DocumentObjectGroupPython] FPSimLED213  label="BtnSilLed[3][6]"  # scripted group (container) (typed FeaturePython)
  Group = -> [Fillet115]
  Unenlightened_Blue = 120
  Unenlightened_Green = 120
  Unenlightened_Red = 120
FEATURE [App::DocumentObjectGroupPython] FPSimButton117  label="BtnSil[3][6]"  # scripted group (container) (typed FeaturePython)
  Group = -> [FPSimLED213]
  PressureResolutionAng = (0,0,0)
  PressureResolutionLin = (0,0,0)
  RotationAngle = 0
  RotationAxis = (0,0,0)
  RotationCenter = (0,0,0)
  SwitchMode = false
  Translation = (0,0,-1)
FEATURE [App::Part] Part136  label="FrBtnSil[3][6]"
  Group = -> [Box230,FPSimButton117,Fillet115,Box313,FPSimLED213]
  License = CC BY 3.0
  LicenseURL = http://creativecommons.org/licenses/by/3.0/
  Origin = -> Origin140
  Placement = pos=(-32,13,0) rot=(0,0,1;0rad)
FEATURE [Part::Box] Box314  label="Cube282"
  AttacherType = Attacher::AttachEngine3D
  Height = 1
  Length = 25
  Width = 18.5
FEATURE [Part::Fillet] Fillet116
  Base = -> Box314
  Edges = 8 edges r=0.2: [Edge1,Edge2,Edge3,Edge5,Edge6,Edge7,Edge10,Edge12]
FEATURE [App::DocumentObjectGroupPython] FPSimLED214  label="BtnSilLed[4][6]"  # scripted group (container) (typed FeaturePython)
  Group = -> [Fillet116]
  Unenlightened_Blue = 120
  Unenlightened_Green = 120
  Unenlightened_Red = 120
FEATURE [App::DocumentObjectGroupPython] FPSimButton116  label="BtnSil[4][6]"  # scripted group (container) (typed FeaturePython)
  Group = -> [FPSimLED214]
  PressureResolutionAng = (0,0,0)
  PressureResolutionLin = (0,0,0)
  RotationAngle = 0
  RotationAxis = (0,0,0)
  RotationCenter = (0,0,0)
  SwitchMode = false
  Translation = (0,0,-1)
FEATURE [App::Part] Part137  label="FrBtnSil[4][6]"
  Group = -> [Box227,FPSimButton116,Box314,Fillet116,FPSimLED214]
  License = CC BY 3.0
  LicenseURL = http://creativecommons.org/licenses/by/3.0/
  Origin = -> Origin137
  Placement = pos=(-3,13,0) rot=(0,0,1;0rad)
FEATURE [Part::Box] Box315  label="Cube283"
  AttacherType = Attacher::AttachEngine3D
  Height = 1
  Length = 25
  Width = 18.5
FEATURE [Part::Fillet] Fillet117
  Base = -> Box315
  Edges = 8 edges r=0.2: [Edge1,Edge2,Edge3,Edge5,Edge6,Edge7,Edge10,Edge12]
FEATURE [App::DocumentObjectGroupPython] FPSimLED215  label="BtnSilLed[5][6]"  # scripted group (container) (typed FeaturePython)
  Group = -> [Fillet117]
  Unenlightened_Blue = 120
  Unenlightened_Green = 120
  Unenlightened_Red = 120
FEATURE [App::DocumentObjectGroupPython] FPSimButton114  label="BtnSil[5][6]"  # scripted group (container) (typed FeaturePython)
  Group = -> [FPSimLED215]
  PressureResolutionAng = (0,0,0)
  PressureResolutionLin = (0,0,0)
  RotationAngle = 0
  RotationAxis = (0,0,0)
  RotationCenter = (0,0,0)
  SwitchMode = false
  Translation = (0,0,-1)
FEATURE [App::Part] Part141  label="FrBtnSil[5][6]"
  Group = -> [Box231,FPSimButton114,Fillet117,Box315,FPSimLED215]
  License = CC BY 3.0
  LicenseURL = http://creativecommons.org/licenses/by/3.0/
  Origin = -> Origin135
  Placement = pos=(26,13,0) rot=(0,0,1;0rad)
FEATURE [Part::Box] Box316  label="Cube284"
  AttacherType = Attacher::AttachEngine3D
  Height = 1
  Length = 25
  Width = 18.5
FEATURE [Part::Fillet] Fillet118
  Base = -> Box316
  Edges = 8 edges r=0.2: [Edge1,Edge2,Edge3,Edge5,Edge6,Edge7,Edge10,Edge12]
FEATURE [App::DocumentObjectGroupPython] FPSimLED216  label="BtnSilLed[6][6]"  # scripted group (container) (typed FeaturePython)
  Group = -> [Fillet118]
  Unenlightened_Blue = 120
  Unenlightened_Green = 120
  Unenlightened_Red = 120
FEATURE [App::DocumentObjectGroupPython] FPSimButton119  label="BtnSil[6][6]"  # scripted group (container) (typed FeaturePython)
  Group = -> [FPSimLED216]
  PressureResolutionAng = (0,0,0)
  PressureResolutionLin = (0,0,0)
  RotationAngle = 0
  RotationAxis = (0,0,0)
  RotationCenter = (0,0,0)
  SwitchMode = false
  Translation = (0,0,-1)
FEATURE [App::Part] Part138  label="FrBtnSil[6][6]"
  Group = -> [Box233,FPSimButton119,Fillet118,Box316,FPSimLED216]
  License = CC BY 3.0
  LicenseURL = http://creativecommons.org/licenses/by/3.0/
  Origin = -> Origin141
  Placement = pos=(55,13,0) rot=(0,0,1;0rad)
FEATURE [Part::Box] Box317  label="Cube285"
  AttacherType = Attacher::AttachEngine3D
  Height = 1
  Length = 25
  Width = 18.5
FEATURE [Part::Fillet] Fillet119
  Base = -> Box317
  Edges = 8 edges r=0.2: [Edge1,Edge2,Edge3,Edge5,Edge6,Edge7,Edge10,Edge12]
FEATURE [App::DocumentObjectGroupPython] FPSimLED217  label="BtnSilLed[7][6]"  # scripted group (container) (typed FeaturePython)
  Group = -> [Fillet119]
  Unenlightened_Blue = 120
  Unenlightened_Green = 120
  Unenlightened_Red = 120
FEATURE [App::DocumentObjectGroupPython] FPSimButton118  label="BtnSil[7][6]"  # scripted group (container) (typed FeaturePython)
  Group = -> [FPSimLED217]
  PressureResolutionAng = (0,0,0)
  PressureResolutionLin = (0,0,0)
  RotationAngle = 0
  RotationAxis = (0,0,0)
  RotationCenter = (0,0,0)
  SwitchMode = false
  Translation = (0,0,-1)
FEATURE [App::Part] Part140  label="FrBtnSil[7][6]"
  Group = -> [Box229,FPSimButton118,Fillet119,Box317,FPSimLED217]
  License = CC BY 3.0
  LicenseURL = http://creativecommons.org/licenses/by/3.0/
  Origin = -> Origin138
  Placement = pos=(84,13,0) rot=(0,0,1;0rad)
FEATURE [App::Part] Part139  label="FrBtnSilRow006"
  Group = -> [Part142,Part143,Part135,Part136,Part137,Part141,Part138,Part140]
  License = CC BY 3.0
  LicenseURL = http://creativecommons.org/licenses/by/3.0/
  Origin = -> Origin143
  Placement = pos=(0,-132,0) rot=(0,0,1;0rad)
FEATURE [Part::Box] Box318  label="Cube286"
  AttacherType = Attacher::AttachEngine3D
  Height = 1
  Length = 25
  Width = 18.5
FEATURE [Part::Fillet] Fillet120
  Base = -> Box318
  Edges = 8 edges r=0.2: [Edge1,Edge2,Edge3,Edge5,Edge6,Edge7,Edge10,Edge12]
FEATURE [App::DocumentObjectGroupPython] FPSimLED218  label="BtnSilLed[0][7]"  # scripted group (container) (typed FeaturePython)
  Group = -> [Fillet120]
  Unenlightened_Blue = 120
  Unenlightened_Green = 120
  Unenlightened_Red = 120
FEATURE [App::DocumentObjectGroupPython] FPSimButton128  label="BtnSil[0][7]"  # scripted group (container) (typed FeaturePython)
  Group = -> [FPSimLED218]
  PressureResolutionAng = (0,0,0)
  PressureResolutionLin = (0,0,0)
  RotationAngle = 0
  RotationAxis = (0,0,0)
  RotationCenter = (0,0,0)
  SwitchMode = false
  Translation = (0,0,-1)
FEATURE [App::Part] Part151  label="FrBtnSil[0][7]"
  Group = -> [Box236,FPSimButton128,Box318,Fillet120,FPSimLED218]
  License = CC BY 3.0
  LicenseURL = http://creativecommons.org/licenses/by/3.0/
  Origin = -> Origin151
  Placement = pos=(-119,13,0) rot=(0,0,1;0rad)
FEATURE [Part::Box] Box319  label="Cube287"
  AttacherType = Attacher::AttachEngine3D
  Height = 1
  Length = 25
  Width = 18.5
FEATURE [Part::Fillet] Fillet121
  Base = -> Box319
  Edges = 8 edges r=0.2: [Edge1,Edge2,Edge3,Edge5,Edge6,Edge7,Edge10,Edge12]
FEATURE [App::DocumentObjectGroupPython] FPSimLED219  label="BtnSilLed[1][7]"  # scripted group (container) (typed FeaturePython)
  Group = -> [Fillet121]
  Unenlightened_Blue = 120
  Unenlightened_Green = 120
  Unenlightened_Red = 120
FEATURE [App::DocumentObjectGroupPython] FPSimButton121  label="BtnSil[1][7]"  # scripted group (container) (typed FeaturePython)
  Group = -> [FPSimLED219]
  PressureResolutionAng = (0,0,0)
  PressureResolutionLin = (0,0,0)
  RotationAngle = 0
  RotationAxis = (0,0,0)
  RotationCenter = (0,0,0)
  SwitchMode = false
  Translation = (0,0,-1)
FEATURE [App::Part] Part152  label="FrBtnSil[1][7]"
  Group = -> [Box240,FPSimButton121,Fillet121,Box319,FPSimLED219]
  License = CC BY 3.0
  LicenseURL = http://creativecommons.org/licenses/by/3.0/
  Origin = -> Origin148
  Placement = pos=(-90,13,0) rot=(0,0,1;0rad)
FEATURE [Part::Box] Box320  label="Cube288"
  AttacherType = Attacher::AttachEngine3D
  Height = 1
  Length = 25
  Width = 18.5
FEATURE [Part::Fillet] Fillet122
  Base = -> Box320
  Edges = 8 edges r=0.2: [Edge1,Edge2,Edge3,Edge5,Edge6,Edge7,Edge10,Edge12]
FEATURE [App::DocumentObjectGroupPython] FPSimLED220  label="BtnSilLed[2][7]"  # scripted group (container) (typed FeaturePython)
  Group = -> [Fillet122]
  Unenlightened_Blue = 120
  Unenlightened_Green = 120
  Unenlightened_Red = 120
FEATURE [App::DocumentObjectGroupPython] FPSimButton123  label="BtnSil[2][7]"  # scripted group (container) (typed FeaturePython)
  Group = -> [FPSimLED220]
  PressureResolutionAng = (0,0,0)
  PressureResolutionLin = (0,0,0)
  RotationAngle = 0
  RotationAxis = (0,0,0)
  RotationCenter = (0,0,0)
  SwitchMode = false
  Translation = (0,0,-1)
FEATURE [App::Part] Part144  label="FrBtnSil[2][7]"
  Group = -> [Box234,FPSimButton123,Fillet122,Box320,FPSimLED220]
  License = CC BY 3.0
  LicenseURL = http://creativecommons.org/licenses/by/3.0/
  Origin = -> Origin145
  Placement = pos=(-61,13,0) rot=(0,0,1;0rad)
FEATURE [Part::Box] Box321  label="Cube289"
  AttacherType = Attacher::AttachEngine3D
  Height = 1
  Length = 25
  Width = 18.5
FEATURE [Part::Fillet] Fillet123
  Base = -> Box321
  Edges = 8 edges r=0.2: [Edge1,Edge2,Edge3,Edge5,Edge6,Edge7,Edge10,Edge12]
FEATURE [App::DocumentObjectGroupPython] FPSimLED221  label="BtnSilLed[3][7]"  # scripted group (container) (typed FeaturePython)
  Group = -> [Fillet123]
  Unenlightened_Blue = 120
  Unenlightened_Green = 120
  Unenlightened_Red = 120
FEATURE [App::DocumentObjectGroupPython] FPSimButton125  label="BtnSil[3][7]"  # scripted group (container) (typed FeaturePython)
  Group = -> [FPSimLED221]
  PressureResolutionAng = (0,0,0)
  PressureResolutionLin = (0,0,0)
  RotationAngle = 0
  RotationAxis = (0,0,0)
  RotationCenter = (0,0,0)
  SwitchMode = false
  Translation = (0,0,-1)
FEATURE [App::Part] Part145  label="FrBtnSil[3][7]"
  Group = -> [Box238,FPSimButton125,Fillet123,Box321,FPSimLED221]
  License = CC BY 3.0
  LicenseURL = http://creativecommons.org/licenses/by/3.0/
  Origin = -> Origin149
  Placement = pos=(-32,13,0) rot=(0,0,1;0rad)
FEATURE [Part::Box] Box322  label="Cube290"
  AttacherType = Attacher::AttachEngine3D
  Height = 1
  Length = 25
  Width = 18.5
FEATURE [Part::Fillet] Fillet124
  Base = -> Box322
  Edges = 8 edges r=0.2: [Edge1,Edge2,Edge3,Edge5,Edge6,Edge7,Edge10,Edge12]
FEATURE [App::DocumentObjectGroupPython] FPSimLED222  label="BtnSilLed[4][7]"  # scripted group (container) (typed FeaturePython)
  Group = -> [Fillet124]
  Unenlightened_Blue = 120
  Unenlightened_Green = 120
  Unenlightened_Red = 120
FEATURE [App::DocumentObjectGroupPython] FPSimButton124  label="BtnSil[4][7]"  # scripted group (container) (typed FeaturePython)
  Group = -> [FPSimLED222]
  PressureResolutionAng = (0,0,0)
  PressureResolutionLin = (0,0,0)
  RotationAngle = 0
  RotationAxis = (0,0,0)
  RotationCenter = (0,0,0)
  SwitchMode = false
  Translation = (0,0,-1)
FEATURE [App::Part] Part146  label="FrBtnSil[4][7]"
  Group = -> [Box235,FPSimButton124,Box322,Fillet124,FPSimLED222]
  License = CC BY 3.0
  LicenseURL = http://creativecommons.org/licenses/by/3.0/
  Origin = -> Origin146
  Placement = pos=(-3,13,0) rot=(0,0,1;0rad)
FEATURE [Part::Box] Box323  label="Cube291"
  AttacherType = Attacher::AttachEngine3D
  Height = 1
  Length = 25
  Width = 18.5
FEATURE [Part::Fillet] Fillet125
  Base = -> Box323
  Edges = 8 edges r=0.2: [Edge1,Edge2,Edge3,Edge5,Edge6,Edge7,Edge10,Edge12]
FEATURE [App::DocumentObjectGroupPython] FPSimLED223  label="BtnSilLed[5][7]"  # scripted group (container) (typed FeaturePython)
  Group = -> [Fillet125]
  Unenlightened_Blue = 120
  Unenlightened_Green = 120
  Unenlightened_Red = 120
FEATURE [App::DocumentObjectGroupPython] FPSimButton122  label="BtnSil[5][7]"  # scripted group (container) (typed FeaturePython)
  Group = -> [FPSimLED223]
  PressureResolutionAng = (0,0,0)
  PressureResolutionLin = (0,0,0)
  RotationAngle = 0
  RotationAxis = (0,0,0)
  RotationCenter = (0,0,0)
  SwitchMode = false
  Translation = (0,0,-1)
FEATURE [App::Part] Part150  label="FrBtnSil[5][7]"
  Group = -> [Box239,FPSimButton122,Fillet125,Box323,FPSimLED223]
  License = CC BY 3.0
  LicenseURL = http://creativecommons.org/licenses/by/3.0/
  Origin = -> Origin144
  Placement = pos=(26,13,0) rot=(0,0,1;0rad)
FEATURE [Part::Box] Box324  label="Cube292"
  AttacherType = Attacher::AttachEngine3D
  Height = 1
  Length = 25
  Width = 18.5
FEATURE [Part::Fillet] Fillet126
  Base = -> Box324
  Edges = 8 edges r=0.2: [Edge1,Edge2,Edge3,Edge5,Edge6,Edge7,Edge10,Edge12]
FEATURE [App::DocumentObjectGroupPython] FPSimLED224  label="BtnSilLed[6][7]"  # scripted group (container) (typed FeaturePython)
  Group = -> [Fillet126]
  Unenlightened_Blue = 120
  Unenlightened_Green = 120
  Unenlightened_Red = 120
FEATURE [App::DocumentObjectGroupPython] FPSimButton127  label="BtnSil[6][7]"  # scripted group (container) (typed FeaturePython)
  Group = -> [FPSimLED224]
  PressureResolutionAng = (0,0,0)
  PressureResolutionLin = (0,0,0)
  RotationAngle = 0
  RotationAxis = (0,0,0)
  RotationCenter = (0,0,0)
  SwitchMode = false
  Translation = (0,0,-1)
FEATURE [App::Part] Part147  label="FrBtnSil[6][7]"
  Group = -> [Box241,FPSimButton127,Fillet126,Box324,FPSimLED224]
  License = CC BY 3.0
  LicenseURL = http://creativecommons.org/licenses/by/3.0/
  Origin = -> Origin150
  Placement = pos=(55,13,0) rot=(0,0,1;0rad)
FEATURE [Part::Box] Box325  label="Cube293"
  AttacherType = Attacher::AttachEngine3D
  Height = 1
  Length = 25
  Width = 18.5
FEATURE [Part::Fillet] Fillet127
  Base = -> Box325
  Edges = 8 edges r=0.2: [Edge1,Edge2,Edge3,Edge5,Edge6,Edge7,Edge10,Edge12]
FEATURE [App::DocumentObjectGroupPython] FPSimLED225  label="BtnSilLed[7][7]"  # scripted group (container) (typed FeaturePython)
  Group = -> [Fillet127]
  Unenlightened_Blue = 120
  Unenlightened_Green = 120
  Unenlightened_Red = 120
FEATURE [App::DocumentObjectGroupPython] FPSimButton126  label="BtnSil[7][7]"  # scripted group (container) (typed FeaturePython)
  Group = -> [FPSimLED225]
  PressureResolutionAng = (0,0,0)
  PressureResolutionLin = (0,0,0)
  RotationAngle = 0
  RotationAxis = (0,0,0)
  RotationCenter = (0,0,0)
  SwitchMode = false
  Translation = (0,0,-1)
FEATURE [App::Part] Part149  label="FrBtnSil[7][7]"
  Group = -> [Box237,FPSimButton126,Fillet127,Box325,FPSimLED225]
  License = CC BY 3.0
  LicenseURL = http://creativecommons.org/licenses/by/3.0/
  Origin = -> Origin147
  Placement = pos=(84,13,0) rot=(0,0,1;0rad)
FEATURE [App::Part] Part148  label="FrBtnSilRow007"
  Group = -> [Part151,Part152,Part144,Part145,Part146,Part150,Part147,Part149]
  License = CC BY 3.0
  LicenseURL = http://creativecommons.org/licenses/by/3.0/
  Origin = -> Origin152
  Placement = pos=(0,-154,0) rot=(0,0,1;0rad)
FEATURE [App::Part] Part153  label="FrBtnSilMatrix"
  Group = -> [Part089,Part093,Part103,Part112,Part121,Part130,Part139,Part148]
  License = CC BY 3.0
  LicenseURL = http://creativecommons.org/licenses/by/3.0/
  Origin = -> Origin153
FEATURE [App::DocumentObjectGroup] Group006  label="Middle"
  Group = -> [Part046,Part047,Part048,Part049,Part050,Part051,Part052,Part053,Part153]
FEATURE [App::DocumentObjectGroup] Group003  label="Bottom"
  Group = -> [Group005,Group006,Group007]
FEATURE [App::DocumentObjectGroup] Group004  label="Widgets"
  Group = -> [Group001,Group002,Group003]
FEATURE [App::Part] Part  label="FrMain"
  Group = -> [ImagePlane,Box,ImagePlane002,Group004,Part001,Part002,Part003,Part004,Part005,Part006,Part007,Part008,Part009,Part010,Part011,Part012,Part013,Part014,Part015,Part016,Part017,Part018,Part019,Part020,Part021,Group,Group001,Group002,Group003,Part022,Part023,Part024,Part025,Part026,Part027,Part028,Part029,Part030,Part031,Part032,Group005,Group006,Group007,Part033,Part034,Part035,Part036,Part037,+38 more]
  License = CC BY 3.0
  LicenseURL = http://creativecommons.org/licenses/by/3.0/
  Origin = -> Origin001
note: 97 file-system paths scrubbed to <path> (originals preserved in the JSON sidecar)
